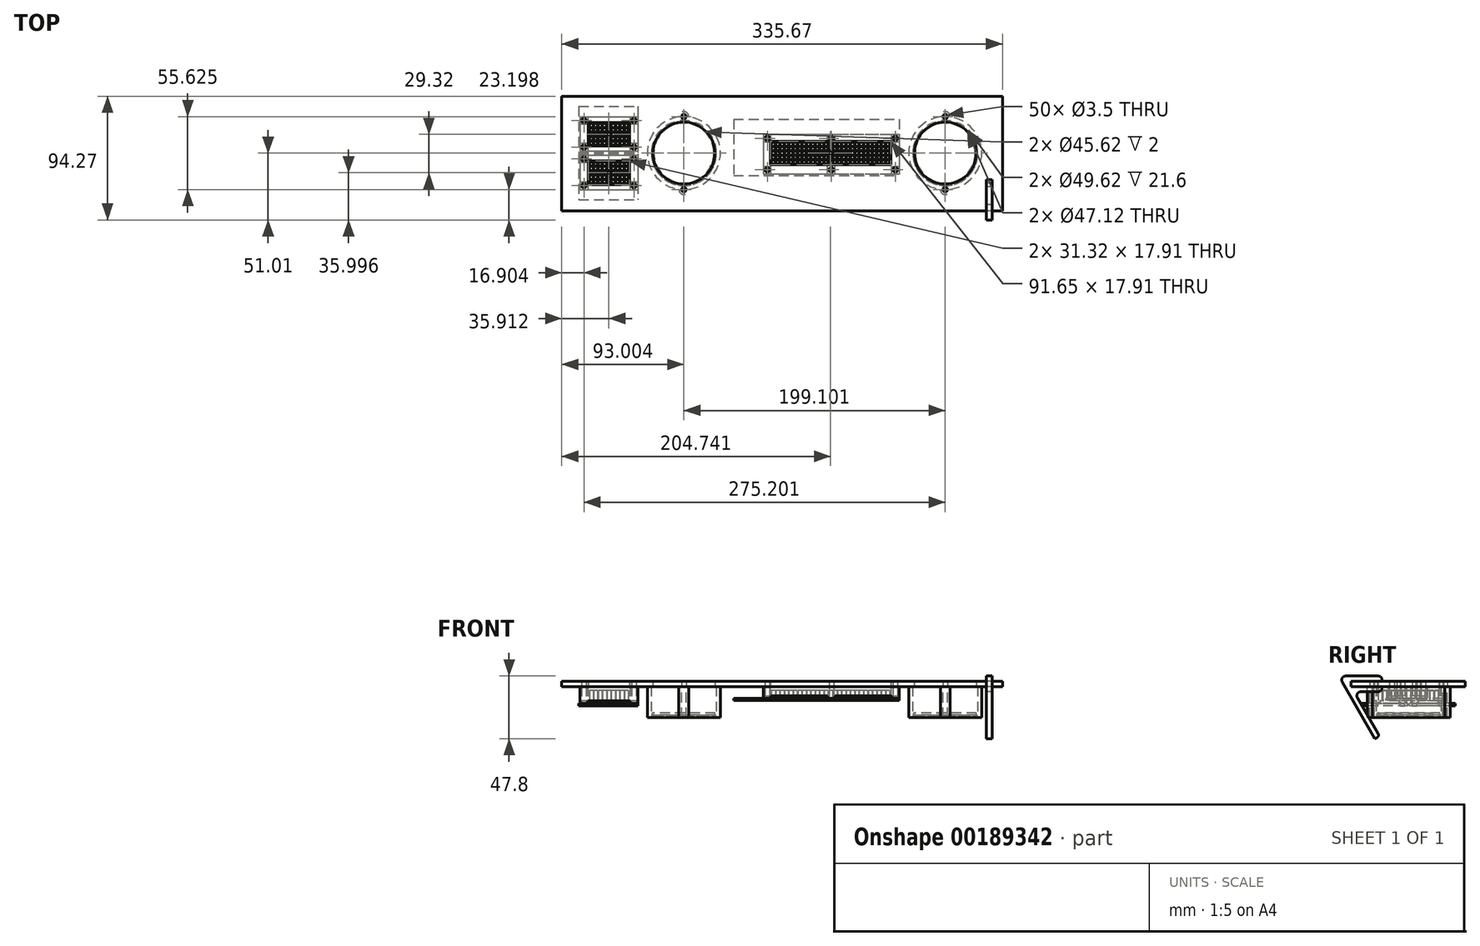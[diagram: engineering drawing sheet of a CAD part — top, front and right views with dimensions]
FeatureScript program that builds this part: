
annotation { "Feature Type Name" : "Feature", "Feature Type Description" : "" }
export const myFeature = defineFeature(function(context is Context, id is Id, definition is map)
    precondition{}
    {
        {
            var Q0;
            Q0=qCreatedBy(makeId("Top.planeOp"),FACE);
            var sketch = newSketch(context, id + "F0", { "sketchPlane" : qUnion([Q0])});
            skLineSegment(sketch, "E0.bottom", {"start": v(-19.95, 23.98) * mm, "end": v(106.25, 23.98) * mm});
            skLineSegment(sketch, "E0.top", {"start": v(-19.95, -19.02) * mm, "end": v(106.25, -19.02) * mm});
            skLineSegment(sketch, "E0.left", {"start": v(-19.95, 23.98) * mm, "end": v(-19.95, -19.02) * mm});
            skLineSegment(sketch, "E0.right", {"start": v(106.25, 23.98) * mm, "end": v(106.25, -19.02) * mm});
            skLineSegment(sketch, "E1.bottom", {"start": v(-137.86, 33.71) * mm, "end": v(-92.86, 33.71) * mm});
            skLineSegment(sketch, "E1.top", {"start": v(-137.86, -1.29) * mm, "end": v(-92.86, -1.29) * mm});
            skLineSegment(sketch, "E1.left", {"start": v(-137.86, 33.71) * mm, "end": v(-137.86, -1.29) * mm});
            skLineSegment(sketch, "E1.right", {"start": v(-92.86, 33.71) * mm, "end": v(-92.86, -1.29) * mm});
            skLineSegment(sketch, "E2.bottom", {"start": v(-137.86, -2.29) * mm, "end": v(-92.86, -2.29) * mm});
            skLineSegment(sketch, "E2.top", {"start": v(-137.86, -37.29) * mm, "end": v(-92.86, -37.29) * mm});
            skLineSegment(sketch, "E2.left", {"start": v(-137.86, -2.29) * mm, "end": v(-137.86, -37.29) * mm});
            skLineSegment(sketch, "E2.right", {"start": v(-92.86, -2.29) * mm, "end": v(-92.86, -37.29) * mm});
            skCircle(sketch, "E3", {"center": v(141.25, -1.79) * mm, "radius": 23.81 * mm});
            skCircle(sketch, "E4", {"center": v(-57.86, -1.79) * mm, "radius": 23.81 * mm});
            skLineSegment(sketch, "E5", {"start": v(-115.36, -1.29) * mm, "end": v(-115.36, -2.29) * mm, "construction": true});
            skLineSegment(sketch, "E6", {"start": v(-115.36, -1.79) * mm, "end": v(-90.24, -1.79) * mm, "construction": true});
            skLineSegment(sketch, "E7", {"start": v(43.15, -19.02) * mm, "end": v(43.15, -1.79) * mm});
            skSolve(sketch);
        }
        {
            var Q0;
            Q0=qCreatedBy(makeId("Top.planeOp"),FACE);
            cPlane(context, id + "F1", {"entities" : qUnion([Q0]), "cplaneType" : CPlaneType.OFFSET, "offset" : 9 * mm, "oppositeDirection" : true, "width" : 150 * mm, "height" : 150 * mm});
        }
        {
            var Q0;
            Q0=qCreatedBy(id+"F1.planeOp",FACE);
            var sketch = newSketch(context, id + "F2", { "sketchPlane" : qUnion([Q0])});
            skLineSegment(sketch, "E8.0", {"start": v(-19.95, 23.98) * mm, "end": v(-19.95, -19.02) * mm});
            skLineSegment(sketch, "E8.1", {"start": v(-19.95, 23.98) * mm, "end": v(106.25, 23.98) * mm});
            skLineSegment(sketch, "E8.2", {"start": v(-19.95, -19.02) * mm, "end": v(106.25, -19.02) * mm});
            skLineSegment(sketch, "E8.3", {"start": v(106.25, 23.98) * mm, "end": v(106.25, -19.02) * mm});
            skCircle(sketch, "E9", {"center": v(5.75, -14.52) * mm, "radius": 1.75 * mm});
            skCircle(sketch, "E10", {"center": v(54.5, -14.52) * mm, "radius": 1.75 * mm});
            skCircle(sketch, "E11", {"center": v(103.25, -14.52) * mm, "radius": 1.75 * mm});
            skCircle(sketch, "E12", {"center": v(5.75, 9.48) * mm, "radius": 1.75 * mm});
            skCircle(sketch, "E13", {"center": v(54.5, 9.48) * mm, "radius": 1.75 * mm});
            skCircle(sketch, "E14", {"center": v(103.25, 9.48) * mm, "radius": 1.75 * mm});
            skCircle(sketch, "E15", {"center": v(10.3, 4.91) * mm, "radius": 1.5 * mm});
            skCircle(sketch, "E16.0.1.0", {"center": v(10.3, 1.56) * mm, "radius": 1.5 * mm});
            skCircle(sketch, "E16.0.2.0", {"center": v(10.3, -1.79) * mm, "radius": 1.5 * mm});
            skCircle(sketch, "E16.0.3.0", {"center": v(10.3, -5.14) * mm, "radius": 1.5 * mm});
            skCircle(sketch, "E16.0.4.0", {"center": v(10.3, -8.5) * mm, "radius": 1.5 * mm});
            skCircle(sketch, "E16.1.0.0", {"center": v(13.66, 4.91) * mm, "radius": 1.5 * mm});
            skCircle(sketch, "E16.1.1.0", {"center": v(13.66, 1.56) * mm, "radius": 1.5 * mm});
            skCircle(sketch, "E16.1.2.0", {"center": v(13.66, -1.79) * mm, "radius": 1.5 * mm});
            skCircle(sketch, "E16.1.3.0", {"center": v(13.66, -5.14) * mm, "radius": 1.5 * mm});
            skCircle(sketch, "E16.1.4.0", {"center": v(13.66, -8.5) * mm, "radius": 1.5 * mm});
            skCircle(sketch, "E16.2.0.0", {"center": v(17, 4.91) * mm, "radius": 1.5 * mm});
            skCircle(sketch, "E16.2.1.0", {"center": v(17, 1.56) * mm, "radius": 1.5 * mm});
            skCircle(sketch, "E16.2.2.0", {"center": v(17, -1.79) * mm, "radius": 1.5 * mm});
            skCircle(sketch, "E16.2.3.0", {"center": v(17, -5.14) * mm, "radius": 1.5 * mm});
            skCircle(sketch, "E16.2.4.0", {"center": v(17, -8.5) * mm, "radius": 1.5 * mm});
            skCircle(sketch, "E16.3.0.0", {"center": v(20.36, 4.91) * mm, "radius": 1.5 * mm});
            skCircle(sketch, "E16.3.1.0", {"center": v(20.36, 1.56) * mm, "radius": 1.5 * mm});
            skCircle(sketch, "E16.3.2.0", {"center": v(20.36, -1.79) * mm, "radius": 1.5 * mm});
            skCircle(sketch, "E16.3.3.0", {"center": v(20.36, -5.14) * mm, "radius": 1.5 * mm});
            skCircle(sketch, "E16.3.4.0", {"center": v(20.36, -8.5) * mm, "radius": 1.5 * mm});
            skCircle(sketch, "E16.4.0.0", {"center": v(23.71, 4.91) * mm, "radius": 1.5 * mm});
            skCircle(sketch, "E16.4.1.0", {"center": v(23.71, 1.56) * mm, "radius": 1.5 * mm});
            skCircle(sketch, "E16.4.2.0", {"center": v(23.71, -1.79) * mm, "radius": 1.5 * mm});
            skCircle(sketch, "E16.4.3.0", {"center": v(23.71, -5.14) * mm, "radius": 1.5 * mm});
            skCircle(sketch, "E16.4.4.0", {"center": v(23.71, -8.5) * mm, "radius": 1.5 * mm});
            skCircle(sketch, "E16.5.0.0", {"center": v(27.07, 4.91) * mm, "radius": 1.5 * mm});
            skCircle(sketch, "E16.5.1.0", {"center": v(27.07, 1.56) * mm, "radius": 1.5 * mm});
            skCircle(sketch, "E16.5.2.0", {"center": v(27.07, -1.79) * mm, "radius": 1.5 * mm});
            skCircle(sketch, "E16.5.3.0", {"center": v(27.07, -5.14) * mm, "radius": 1.5 * mm});
            skCircle(sketch, "E16.5.4.0", {"center": v(27.07, -8.5) * mm, "radius": 1.5 * mm});
            skCircle(sketch, "E16.6.0.0", {"center": v(30.42, 4.91) * mm, "radius": 1.5 * mm});
            skCircle(sketch, "E16.6.1.0", {"center": v(30.42, 1.56) * mm, "radius": 1.5 * mm});
            skCircle(sketch, "E16.6.2.0", {"center": v(30.42, -1.79) * mm, "radius": 1.5 * mm});
            skCircle(sketch, "E16.6.3.0", {"center": v(30.42, -5.14) * mm, "radius": 1.5 * mm});
            skCircle(sketch, "E16.6.4.0", {"center": v(30.42, -8.5) * mm, "radius": 1.5 * mm});
            skCircle(sketch, "E16.7.0.0", {"center": v(33.77, 4.91) * mm, "radius": 1.5 * mm});
            skCircle(sketch, "E16.7.1.0", {"center": v(33.77, 1.56) * mm, "radius": 1.5 * mm});
            skCircle(sketch, "E16.7.2.0", {"center": v(33.77, -1.79) * mm, "radius": 1.5 * mm});
            skCircle(sketch, "E16.7.3.0", {"center": v(33.77, -5.14) * mm, "radius": 1.5 * mm});
            skCircle(sketch, "E16.7.4.0", {"center": v(33.77, -8.5) * mm, "radius": 1.5 * mm});
            skCircle(sketch, "E16.8.0.0", {"center": v(37.12, 4.91) * mm, "radius": 1.5 * mm});
            skCircle(sketch, "E16.8.1.0", {"center": v(37.12, 1.56) * mm, "radius": 1.5 * mm});
            skCircle(sketch, "E16.8.2.0", {"center": v(37.12, -1.79) * mm, "radius": 1.5 * mm});
            skCircle(sketch, "E16.8.3.0", {"center": v(37.12, -5.14) * mm, "radius": 1.5 * mm});
            skCircle(sketch, "E16.8.4.0", {"center": v(37.12, -8.5) * mm, "radius": 1.5 * mm});
            skCircle(sketch, "E16.9.0.0", {"center": v(40.47, 4.91) * mm, "radius": 1.5 * mm});
            skCircle(sketch, "E16.9.1.0", {"center": v(40.47, 1.56) * mm, "radius": 1.5 * mm});
            skCircle(sketch, "E16.9.2.0", {"center": v(40.47, -1.79) * mm, "radius": 1.5 * mm});
            skCircle(sketch, "E16.9.3.0", {"center": v(40.47, -5.14) * mm, "radius": 1.5 * mm});
            skCircle(sketch, "E16.9.4.0", {"center": v(40.47, -8.5) * mm, "radius": 1.5 * mm});
            skCircle(sketch, "E16.10.0.0", {"center": v(43.83, 4.91) * mm, "radius": 1.5 * mm});
            skCircle(sketch, "E16.10.1.0", {"center": v(43.83, 1.56) * mm, "radius": 1.5 * mm});
            skCircle(sketch, "E16.10.2.0", {"center": v(43.83, -1.79) * mm, "radius": 1.5 * mm});
            skCircle(sketch, "E16.10.3.0", {"center": v(43.83, -5.14) * mm, "radius": 1.5 * mm});
            skCircle(sketch, "E16.10.4.0", {"center": v(43.83, -8.5) * mm, "radius": 1.5 * mm});
            skCircle(sketch, "E16.11.0.0", {"center": v(47.18, 4.91) * mm, "radius": 1.5 * mm});
            skCircle(sketch, "E16.11.1.0", {"center": v(47.18, 1.56) * mm, "radius": 1.5 * mm});
            skCircle(sketch, "E16.11.2.0", {"center": v(47.18, -1.79) * mm, "radius": 1.5 * mm});
            skCircle(sketch, "E16.11.3.0", {"center": v(47.18, -5.14) * mm, "radius": 1.5 * mm});
            skCircle(sketch, "E16.11.4.0", {"center": v(47.18, -8.5) * mm, "radius": 1.5 * mm});
            skCircle(sketch, "E16.12.0.0", {"center": v(50.53, 4.91) * mm, "radius": 1.5 * mm});
            skCircle(sketch, "E16.12.1.0", {"center": v(50.53, 1.56) * mm, "radius": 1.5 * mm});
            skCircle(sketch, "E16.12.2.0", {"center": v(50.53, -1.79) * mm, "radius": 1.5 * mm});
            skCircle(sketch, "E16.12.3.0", {"center": v(50.53, -5.14) * mm, "radius": 1.5 * mm});
            skCircle(sketch, "E16.12.4.0", {"center": v(50.53, -8.5) * mm, "radius": 1.5 * mm});
            skCircle(sketch, "E16.13.0.0", {"center": v(53.88, 4.91) * mm, "radius": 1.5 * mm});
            skCircle(sketch, "E16.13.1.0", {"center": v(53.88, 1.56) * mm, "radius": 1.5 * mm});
            skCircle(sketch, "E16.13.2.0", {"center": v(53.88, -1.79) * mm, "radius": 1.5 * mm});
            skCircle(sketch, "E16.13.3.0", {"center": v(53.88, -5.14) * mm, "radius": 1.5 * mm});
            skCircle(sketch, "E16.13.4.0", {"center": v(53.88, -8.5) * mm, "radius": 1.5 * mm});
            skCircle(sketch, "E16.14.0.0", {"center": v(57.23, 4.91) * mm, "radius": 1.5 * mm});
            skCircle(sketch, "E16.14.1.0", {"center": v(57.23, 1.56) * mm, "radius": 1.5 * mm});
            skCircle(sketch, "E16.14.2.0", {"center": v(57.23, -1.79) * mm, "radius": 1.5 * mm});
            skCircle(sketch, "E16.14.3.0", {"center": v(57.23, -5.14) * mm, "radius": 1.5 * mm});
            skCircle(sketch, "E16.14.4.0", {"center": v(57.23, -8.5) * mm, "radius": 1.5 * mm});
            skCircle(sketch, "E16.15.0.0", {"center": v(60.59, 4.91) * mm, "radius": 1.5 * mm});
            skCircle(sketch, "E16.15.1.0", {"center": v(60.59, 1.56) * mm, "radius": 1.5 * mm});
            skCircle(sketch, "E16.15.2.0", {"center": v(60.59, -1.79) * mm, "radius": 1.5 * mm});
            skCircle(sketch, "E16.15.3.0", {"center": v(60.59, -5.14) * mm, "radius": 1.5 * mm});
            skCircle(sketch, "E16.15.4.0", {"center": v(60.59, -8.5) * mm, "radius": 1.5 * mm});
            skCircle(sketch, "E16.16.0.0", {"center": v(63.94, 4.91) * mm, "radius": 1.5 * mm});
            skCircle(sketch, "E16.16.1.0", {"center": v(63.94, 1.56) * mm, "radius": 1.5 * mm});
            skCircle(sketch, "E16.16.2.0", {"center": v(63.94, -1.79) * mm, "radius": 1.5 * mm});
            skCircle(sketch, "E16.16.3.0", {"center": v(63.94, -5.14) * mm, "radius": 1.5 * mm});
            skCircle(sketch, "E16.16.4.0", {"center": v(63.94, -8.5) * mm, "radius": 1.5 * mm});
            skCircle(sketch, "E16.17.0.0", {"center": v(67.29, 4.91) * mm, "radius": 1.5 * mm});
            skCircle(sketch, "E16.17.1.0", {"center": v(67.29, 1.56) * mm, "radius": 1.5 * mm});
            skCircle(sketch, "E16.17.2.0", {"center": v(67.29, -1.79) * mm, "radius": 1.5 * mm});
            skCircle(sketch, "E16.17.3.0", {"center": v(67.29, -5.14) * mm, "radius": 1.5 * mm});
            skCircle(sketch, "E16.17.4.0", {"center": v(67.29, -8.5) * mm, "radius": 1.5 * mm});
            skCircle(sketch, "E16.18.0.0", {"center": v(70.64, 4.91) * mm, "radius": 1.5 * mm});
            skCircle(sketch, "E16.18.1.0", {"center": v(70.64, 1.56) * mm, "radius": 1.5 * mm});
            skCircle(sketch, "E16.18.2.0", {"center": v(70.64, -1.79) * mm, "radius": 1.5 * mm});
            skCircle(sketch, "E16.18.3.0", {"center": v(70.64, -5.14) * mm, "radius": 1.5 * mm});
            skCircle(sketch, "E16.18.4.0", {"center": v(70.64, -8.5) * mm, "radius": 1.5 * mm});
            skCircle(sketch, "E16.19.0.0", {"center": v(74, 4.91) * mm, "radius": 1.5 * mm});
            skCircle(sketch, "E16.19.1.0", {"center": v(74, 1.56) * mm, "radius": 1.5 * mm});
            skCircle(sketch, "E16.19.2.0", {"center": v(74, -1.79) * mm, "radius": 1.5 * mm});
            skCircle(sketch, "E16.19.3.0", {"center": v(74, -5.14) * mm, "radius": 1.5 * mm});
            skCircle(sketch, "E16.19.4.0", {"center": v(74, -8.5) * mm, "radius": 1.5 * mm});
            skCircle(sketch, "E16.20.0.0", {"center": v(77.35, 4.91) * mm, "radius": 1.5 * mm});
            skCircle(sketch, "E16.20.1.0", {"center": v(77.35, 1.56) * mm, "radius": 1.5 * mm});
            skCircle(sketch, "E16.20.2.0", {"center": v(77.35, -1.79) * mm, "radius": 1.5 * mm});
            skCircle(sketch, "E16.20.3.0", {"center": v(77.35, -5.14) * mm, "radius": 1.5 * mm});
            skCircle(sketch, "E16.20.4.0", {"center": v(77.35, -8.5) * mm, "radius": 1.5 * mm});
            skCircle(sketch, "E16.21.0.0", {"center": v(80.7, 4.91) * mm, "radius": 1.5 * mm});
            skCircle(sketch, "E16.21.1.0", {"center": v(80.7, 1.56) * mm, "radius": 1.5 * mm});
            skCircle(sketch, "E16.21.2.0", {"center": v(80.7, -1.79) * mm, "radius": 1.5 * mm});
            skCircle(sketch, "E16.21.3.0", {"center": v(80.7, -5.14) * mm, "radius": 1.5 * mm});
            skCircle(sketch, "E16.21.4.0", {"center": v(80.7, -8.5) * mm, "radius": 1.5 * mm});
            skCircle(sketch, "E16.22.0.0", {"center": v(84.05, 4.91) * mm, "radius": 1.5 * mm});
            skCircle(sketch, "E16.22.1.0", {"center": v(84.05, 1.56) * mm, "radius": 1.5 * mm});
            skCircle(sketch, "E16.22.2.0", {"center": v(84.05, -1.79) * mm, "radius": 1.5 * mm});
            skCircle(sketch, "E16.22.3.0", {"center": v(84.05, -5.14) * mm, "radius": 1.5 * mm});
            skCircle(sketch, "E16.22.4.0", {"center": v(84.05, -8.5) * mm, "radius": 1.5 * mm});
            skCircle(sketch, "E16.23.0.0", {"center": v(87.4, 4.91) * mm, "radius": 1.5 * mm});
            skCircle(sketch, "E16.23.1.0", {"center": v(87.4, 1.56) * mm, "radius": 1.5 * mm});
            skCircle(sketch, "E16.23.2.0", {"center": v(87.4, -1.79) * mm, "radius": 1.5 * mm});
            skCircle(sketch, "E16.23.3.0", {"center": v(87.4, -5.14) * mm, "radius": 1.5 * mm});
            skCircle(sketch, "E16.23.4.0", {"center": v(87.4, -8.5) * mm, "radius": 1.5 * mm});
            skCircle(sketch, "E16.24.0.0", {"center": v(90.75, 4.91) * mm, "radius": 1.5 * mm});
            skCircle(sketch, "E16.24.1.0", {"center": v(90.75, 1.56) * mm, "radius": 1.5 * mm});
            skCircle(sketch, "E16.24.2.0", {"center": v(90.75, -1.79) * mm, "radius": 1.5 * mm});
            skCircle(sketch, "E16.24.3.0", {"center": v(90.75, -5.14) * mm, "radius": 1.5 * mm});
            skCircle(sketch, "E16.24.4.0", {"center": v(90.75, -8.5) * mm, "radius": 1.5 * mm});
            skCircle(sketch, "E16.25.0.0", {"center": v(94.1, 4.91) * mm, "radius": 1.5 * mm});
            skCircle(sketch, "E16.25.1.0", {"center": v(94.1, 1.56) * mm, "radius": 1.5 * mm});
            skCircle(sketch, "E16.25.2.0", {"center": v(94.1, -1.79) * mm, "radius": 1.5 * mm});
            skCircle(sketch, "E16.25.3.0", {"center": v(94.1, -5.14) * mm, "radius": 1.5 * mm});
            skCircle(sketch, "E16.25.4.0", {"center": v(94.1, -8.5) * mm, "radius": 1.5 * mm});
            skCircle(sketch, "E16.26.0.0", {"center": v(97.46, 4.91) * mm, "radius": 1.5 * mm});
            skCircle(sketch, "E16.26.1.0", {"center": v(97.46, 1.56) * mm, "radius": 1.5 * mm});
            skCircle(sketch, "E16.26.2.0", {"center": v(97.46, -1.79) * mm, "radius": 1.5 * mm});
            skCircle(sketch, "E16.26.3.0", {"center": v(97.46, -5.14) * mm, "radius": 1.5 * mm});
            skCircle(sketch, "E16.26.4.0", {"center": v(97.46, -8.5) * mm, "radius": 1.5 * mm});
            skLineSegment(sketch, "E16.direction1", {"start": v(10.3, 4.91) * mm, "end": v(13.66, 4.91) * mm, "construction": true});
            skLineSegment(sketch, "E16.direction2", {"start": v(10.3, 4.91) * mm, "end": v(10.3, 1.56) * mm, "construction": true});
            skSolve(sketch);
        }
        {
            var Q0;
            Q0=makeQuery(id+"F2.imprint","IMPRINT",FACE,{"disambiguationData":[TD([[makeQuery(id+"F2.imprint","IMPRINT",EDGE,{"derivedFrom":sQuery(id+"F2.wireOp",EDGE,"E8.0")}),1.0]])]});
            extrude(context, id + "F3", {"entities" : qUnion([Q0]), "oppositeDirection" : true, "depth" : 1.6 * mm});
        }
        {
            var Q0;
            Q0=makeQuery(id+"F2.imprint","IMPRINT",FACE,{"disambiguationData":[TD([[makeQuery(id+"F2.imprint","IMPRINT",EDGE,{"derivedFrom":sQuery(id+"F2.wireOp",EDGE,"E16.9.2.0")}),1.0]])]});
            var Q1;
            Q1=makeQuery(id+"F2.imprint","IMPRINT",FACE,{"disambiguationData":[TD([[makeQuery(id+"F2.imprint","IMPRINT",EDGE,{"derivedFrom":sQuery(id+"F2.wireOp",EDGE,"E16.12.3.0")}),1.0]])]});
            var Q2;
            Q2=makeQuery(id+"F2.imprint","IMPRINT",FACE,{"disambiguationData":[TD([[makeQuery(id+"F2.imprint","IMPRINT",EDGE,{"derivedFrom":sQuery(id+"F2.wireOp",EDGE,"E16.6.1.0")}),1.0]])]});
            var Q3;
            Q3=makeQuery(id+"F2.imprint","IMPRINT",FACE,{"disambiguationData":[TD([[makeQuery(id+"F2.imprint","IMPRINT",EDGE,{"derivedFrom":sQuery(id+"F2.wireOp",EDGE,"E16.25.2.0")}),1.0]])]});
            var Q4;
            Q4=makeQuery(id+"F2.imprint","IMPRINT",FACE,{"disambiguationData":[TD([[makeQuery(id+"F2.imprint","IMPRINT",EDGE,{"derivedFrom":sQuery(id+"F2.wireOp",EDGE,"E16.22.1.0")}),1.0]])]});
            var Q5;
            Q5=makeQuery(id+"F2.imprint","IMPRINT",FACE,{"disambiguationData":[TD([[makeQuery(id+"F2.imprint","IMPRINT",EDGE,{"derivedFrom":sQuery(id+"F2.wireOp",EDGE,"E16.9.3.0")}),1.0]])]});
            var Q6;
            Q6=makeQuery(id+"F2.imprint","IMPRINT",FACE,{"disambiguationData":[TD([[makeQuery(id+"F2.imprint","IMPRINT",EDGE,{"derivedFrom":sQuery(id+"F2.wireOp",EDGE,"E16.6.2.0")}),1.0]])]});
            var Q7;
            Q7=makeQuery(id+"F2.imprint","IMPRINT",FACE,{"disambiguationData":[TD([[makeQuery(id+"F2.imprint","IMPRINT",EDGE,{"derivedFrom":sQuery(id+"F2.wireOp",EDGE,"E16.3.1.0")}),1.0]])]});
            var Q8;
            Q8=makeQuery(id+"F2.imprint","IMPRINT",FACE,{"disambiguationData":[TD([[makeQuery(id+"F2.imprint","IMPRINT",EDGE,{"derivedFrom":sQuery(id+"F2.wireOp",EDGE,"E16.25.3.0")}),1.0]])]});
            var Q9;
            Q9=makeQuery(id+"F2.imprint","IMPRINT",FACE,{"disambiguationData":[TD([[makeQuery(id+"F2.imprint","IMPRINT",EDGE,{"derivedFrom":sQuery(id+"F2.wireOp",EDGE,"E16.19.1.0")}),1.0]])]});
            var Q10;
            Q10=makeQuery(id+"F2.imprint","IMPRINT",FACE,{"disambiguationData":[TD([[makeQuery(id+"F2.imprint","IMPRINT",EDGE,{"derivedFrom":sQuery(id+"F2.wireOp",EDGE,"E16.16.0.0")}),1.0]])]});
            var Q11;
            Q11=makeQuery(id+"F2.imprint","IMPRINT",FACE,{"disambiguationData":[TD([[makeQuery(id+"F2.imprint","IMPRINT",EDGE,{"derivedFrom":sQuery(id+"F2.wireOp",EDGE,"E16.25.4.0")}),1.0]])]});
            var Q12;
            Q12=makeQuery(id+"F2.imprint","IMPRINT",FACE,{"disambiguationData":[TD([[makeQuery(id+"F2.imprint","IMPRINT",EDGE,{"derivedFrom":sQuery(id+"F2.wireOp",EDGE,"E16.22.3.0")}),1.0]])]});
            var Q13;
            Q13=makeQuery(id+"F2.imprint","IMPRINT",FACE,{"disambiguationData":[TD([[makeQuery(id+"F2.imprint","IMPRINT",EDGE,{"derivedFrom":sQuery(id+"F2.wireOp",EDGE,"E16.16.1.0")}),1.0]])]});
            var Q14;
            Q14=makeQuery(id+"F2.imprint","IMPRINT",FACE,{"disambiguationData":[TD([[makeQuery(id+"F2.imprint","IMPRINT",EDGE,{"derivedFrom":sQuery(id+"F2.wireOp",EDGE,"E16.13.0.0")}),1.0]])]});
            var Q15;
            Q15=makeQuery(id+"F2.imprint","IMPRINT",FACE,{"disambiguationData":[TD([[makeQuery(id+"F2.imprint","IMPRINT",EDGE,{"derivedFrom":sQuery(id+"F2.wireOp",EDGE,"E16.9.4.0")}),1.0]])]});
            var Q16;
            Q16=makeQuery(id+"F2.imprint","IMPRINT",FACE,{"disambiguationData":[TD([[makeQuery(id+"F2.imprint","IMPRINT",EDGE,{"derivedFrom":sQuery(id+"F2.wireOp",EDGE,"E16.6.3.0")}),1.0]])]});
            var Q17;
            Q17=makeQuery(id+"F2.imprint","IMPRINT",FACE,{"disambiguationData":[TD([[makeQuery(id+"F2.imprint","IMPRINT",EDGE,{"derivedFrom":sQuery(id+"F2.wireOp",EDGE,"E16.13.1.0")}),1.0]])]});
            var Q18;
            Q18=makeQuery(id+"F2.imprint","IMPRINT",FACE,{"disambiguationData":[TD([[makeQuery(id+"F2.imprint","IMPRINT",EDGE,{"derivedFrom":sQuery(id+"F2.wireOp",EDGE,"E16.6.4.0")}),1.0]])]});
            var Q19;
            Q19=makeQuery(id+"F2.imprint","IMPRINT",FACE,{"disambiguationData":[TD([[makeQuery(id+"F2.imprint","IMPRINT",EDGE,{"derivedFrom":sQuery(id+"F2.wireOp",EDGE,"E16.3.3.0")}),1.0]])]});
            var Q20;
            Q20=makeQuery(id+"F2.imprint","IMPRINT",FACE,{"disambiguationData":[TD([[makeQuery(id+"F2.imprint","IMPRINT",EDGE,{"derivedFrom":sQuery(id+"F2.wireOp",EDGE,"E16.19.3.0")}),1.0]])]});
            var Q21;
            Q21=makeQuery(id+"F2.imprint","IMPRINT",FACE,{"disambiguationData":[TD([[makeQuery(id+"F2.imprint","IMPRINT",EDGE,{"derivedFrom":sQuery(id+"F2.wireOp",EDGE,"E16.16.2.0")}),1.0]])]});
            var Q22;
            Q22=makeQuery(id+"F2.imprint","IMPRINT",FACE,{"disambiguationData":[TD([[makeQuery(id+"F2.imprint","IMPRINT",EDGE,{"derivedFrom":sQuery(id+"F2.wireOp",EDGE,"E16.8.1.0")}),1.0]])]});
            var Q23;
            Q23=makeQuery(id+"F2.imprint","IMPRINT",FACE,{"disambiguationData":[TD([[makeQuery(id+"F2.imprint","IMPRINT",EDGE,{"derivedFrom":sQuery(id+"F2.wireOp",EDGE,"E16.13.2.0")}),1.0]])]});
            var Q24;
            Q24=makeQuery(id+"F2.imprint","IMPRINT",FACE,{"disambiguationData":[TD([[makeQuery(id+"F2.imprint","IMPRINT",EDGE,{"derivedFrom":sQuery(id+"F2.wireOp",EDGE,"E16.10.1.0")}),1.0]])]});
            var Q25;
            Q25=makeQuery(id+"F2.imprint","IMPRINT",FACE,{"disambiguationData":[TD([[makeQuery(id+"F2.imprint","IMPRINT",EDGE,{"derivedFrom":sQuery(id+"F2.wireOp",EDGE,"E16.7.0.0")}),1.0]])]});
            var Q26;
            Q26=makeQuery(id+"F2.imprint","IMPRINT",FACE,{"disambiguationData":[TD([[makeQuery(id+"F2.imprint","IMPRINT",EDGE,{"derivedFrom":sQuery(id+"F2.wireOp",EDGE,"E16.26.1.0")}),1.0]])]});
            var Q27;
            Q27=makeQuery(id+"F2.imprint","IMPRINT",FACE,{"disambiguationData":[TD([[makeQuery(id+"F2.imprint","IMPRINT",EDGE,{"derivedFrom":sQuery(id+"F2.wireOp",EDGE,"E16.21.0.0")}),1.0]])]});
            var Q28;
            Q28=makeQuery(id+"F2.imprint","IMPRINT",FACE,{"disambiguationData":[TD([[makeQuery(id+"F2.imprint","IMPRINT",EDGE,{"derivedFrom":sQuery(id+"F2.wireOp",EDGE,"E16.23.0.0")}),1.0]])]});
            var Q29;
            Q29=makeQuery(id+"F2.imprint","IMPRINT",FACE,{"disambiguationData":[TD([[makeQuery(id+"F2.imprint","IMPRINT",EDGE,{"derivedFrom":sQuery(id+"F2.wireOp",EDGE,"E16.14.3.0")}),1.0]])]});
            var Q30;
            Q30=makeQuery(id+"F2.imprint","IMPRINT",FACE,{"disambiguationData":[TD([[makeQuery(id+"F2.imprint","IMPRINT",EDGE,{"derivedFrom":sQuery(id+"F2.wireOp",EDGE,"E16.16.3.0")}),1.0]])]});
            var Q31;
            Q31=makeQuery(id+"F2.imprint","IMPRINT",FACE,{"disambiguationData":[TD([[makeQuery(id+"F2.imprint","IMPRINT",EDGE,{"derivedFrom":sQuery(id+"F2.wireOp",EDGE,"E16.11.2.0")}),1.0]])]});
            var Q32;
            Q32=makeQuery(id+"F2.imprint","IMPRINT",FACE,{"disambiguationData":[TD([[makeQuery(id+"F2.imprint","IMPRINT",EDGE,{"derivedFrom":sQuery(id+"F2.wireOp",EDGE,"E16.24.1.0")}),1.0]])]});
            var Q33;
            Q33=makeQuery(id+"F2.imprint","IMPRINT",FACE,{"disambiguationData":[TD([[makeQuery(id+"F2.imprint","IMPRINT",EDGE,{"derivedFrom":sQuery(id+"F2.wireOp",EDGE,"E16.13.3.0")}),1.0]])]});
            var Q34;
            Q34=makeQuery(id+"F2.imprint","IMPRINT",FACE,{"disambiguationData":[TD([[makeQuery(id+"F2.imprint","IMPRINT",EDGE,{"derivedFrom":sQuery(id+"F2.wireOp",EDGE,"E16.7.1.0")}),1.0]])]});
            var Q35;
            Q35=makeQuery(id+"F2.imprint","IMPRINT",FACE,{"disambiguationData":[TD([[makeQuery(id+"F2.imprint","IMPRINT",EDGE,{"derivedFrom":sQuery(id+"F2.wireOp",EDGE,"E16.4.0.0")}),1.0]])]});
            var Q36;
            Q36=makeQuery(id+"F2.imprint","IMPRINT",FACE,{"disambiguationData":[TD([[makeQuery(id+"F2.imprint","IMPRINT",EDGE,{"derivedFrom":sQuery(id+"F2.wireOp",EDGE,"E16.23.1.0")}),1.0]])]});
            var Q37;
            Q37=makeQuery(id+"F2.imprint","IMPRINT",FACE,{"disambiguationData":[TD([[makeQuery(id+"F2.imprint","IMPRINT",EDGE,{"derivedFrom":sQuery(id+"F2.wireOp",EDGE,"E16.20.0.0")}),1.0]])]});
            var Q38;
            Q38=makeQuery(id+"F2.imprint","IMPRINT",FACE,{"disambiguationData":[TD([[makeQuery(id+"F2.imprint","IMPRINT",EDGE,{"derivedFrom":sQuery(id+"F2.wireOp",EDGE,"E16.16.4.0")}),1.0]])]});
            var Q39;
            Q39=makeQuery(id+"F2.imprint","IMPRINT",FACE,{"disambiguationData":[TD([[makeQuery(id+"F2.imprint","IMPRINT",EDGE,{"derivedFrom":sQuery(id+"F2.wireOp",EDGE,"E16.4.3.0")}),1.0]])]});
            var Q40;
            Q40=makeQuery(id+"F2.imprint","IMPRINT",FACE,{"disambiguationData":[TD([[makeQuery(id+"F2.imprint","IMPRINT",EDGE,{"derivedFrom":sQuery(id+"F2.wireOp",EDGE,"E16.14.1.0")}),1.0]])]});
            var Q41;
            Q41=makeQuery(id+"F2.imprint","IMPRINT",FACE,{"disambiguationData":[TD([[makeQuery(id+"F2.imprint","IMPRINT",EDGE,{"derivedFrom":sQuery(id+"F2.wireOp",EDGE,"E16.11.0.0")}),1.0]])]});
            var Q42;
            Q42=makeQuery(id+"F2.imprint","IMPRINT",FACE,{"disambiguationData":[TD([[makeQuery(id+"F2.imprint","IMPRINT",EDGE,{"derivedFrom":sQuery(id+"F2.wireOp",EDGE,"E16.7.4.0")}),1.0]])]});
            var Q43;
            Q43=makeQuery(id+"F2.imprint","IMPRINT",FACE,{"disambiguationData":[TD([[makeQuery(id+"F2.imprint","IMPRINT",EDGE,{"derivedFrom":sQuery(id+"F2.wireOp",EDGE,"E16.23.4.0")}),1.0]])]});
            var Q44;
            Q44=makeQuery(id+"F2.imprint","IMPRINT",FACE,{"disambiguationData":[TD([[makeQuery(id+"F2.imprint","IMPRINT",EDGE,{"derivedFrom":sQuery(id+"F2.wireOp",EDGE,"E16.20.3.0")}),1.0]])]});
            var Q45;
            Q45=makeQuery(id+"F2.imprint","IMPRINT",FACE,{"disambiguationData":[TD([[makeQuery(id+"F2.imprint","IMPRINT",EDGE,{"derivedFrom":sQuery(id+"F2.wireOp",EDGE,"E16.13.4.0")}),1.0]])]});
            var Q46;
            Q46=makeQuery(id+"F2.imprint","IMPRINT",FACE,{"disambiguationData":[TD([[makeQuery(id+"F2.imprint","IMPRINT",EDGE,{"derivedFrom":sQuery(id+"F2.wireOp",EDGE,"E16.10.3.0")}),1.0]])]});
            var Q47;
            Q47=makeQuery(id+"F2.imprint","IMPRINT",FACE,{"disambiguationData":[TD([[makeQuery(id+"F2.imprint","IMPRINT",EDGE,{"derivedFrom":sQuery(id+"F2.wireOp",EDGE,"E16.7.2.0")}),1.0]])]});
            var Q48;
            Q48=makeQuery(id+"F2.imprint","IMPRINT",FACE,{"disambiguationData":[TD([[makeQuery(id+"F2.imprint","IMPRINT",EDGE,{"derivedFrom":sQuery(id+"F2.wireOp",EDGE,"E16.4.1.0")}),1.0]])]});
            var Q49;
            Q49=makeQuery(id+"F2.imprint","IMPRINT",FACE,{"disambiguationData":[TD([[makeQuery(id+"F2.imprint","IMPRINT",EDGE,{"derivedFrom":sQuery(id+"F2.wireOp",EDGE,"E16.26.3.0")}),1.0]])]});
            var Q50;
            Q50=makeQuery(id+"F2.imprint","IMPRINT",FACE,{"disambiguationData":[TD([[makeQuery(id+"F2.imprint","IMPRINT",EDGE,{"derivedFrom":sQuery(id+"F2.wireOp",EDGE,"E16.23.2.0")}),1.0]])]});
            var Q51;
            Q51=makeQuery(id+"F2.imprint","IMPRINT",FACE,{"disambiguationData":[TD([[makeQuery(id+"F2.imprint","IMPRINT",EDGE,{"derivedFrom":sQuery(id+"F2.wireOp",EDGE,"E16.20.1.0")}),1.0]])]});
            var Q52;
            Q52=makeQuery(id+"F2.imprint","IMPRINT",FACE,{"disambiguationData":[TD([[makeQuery(id+"F2.imprint","IMPRINT",EDGE,{"derivedFrom":sQuery(id+"F2.wireOp",EDGE,"E16.4.4.0")}),1.0]])]});
            var Q53;
            Q53=makeQuery(id+"F2.imprint","IMPRINT",FACE,{"disambiguationData":[TD([[makeQuery(id+"F2.imprint","IMPRINT",EDGE,{"derivedFrom":sQuery(id+"F2.wireOp",EDGE,"E16.17.3.0")}),1.0]])]});
            var Q54;
            Q54=makeQuery(id+"F2.imprint","IMPRINT",FACE,{"disambiguationData":[TD([[makeQuery(id+"F2.imprint","IMPRINT",EDGE,{"derivedFrom":sQuery(id+"F2.wireOp",EDGE,"E16.14.2.0")}),1.0]])]});
            var Q55;
            Q55=makeQuery(id+"F2.imprint","IMPRINT",FACE,{"disambiguationData":[TD([[makeQuery(id+"F2.imprint","IMPRINT",EDGE,{"derivedFrom":sQuery(id+"F2.wireOp",EDGE,"E16.11.1.0")}),1.0]])]});
            var Q56;
            Q56=makeQuery(id+"F2.imprint","IMPRINT",FACE,{"disambiguationData":[TD([[makeQuery(id+"F2.imprint","IMPRINT",EDGE,{"derivedFrom":sQuery(id+"F2.wireOp",EDGE,"E16.20.4.0")}),1.0]])]});
            var Q57;
            Q57=makeQuery(id+"F2.imprint","IMPRINT",FACE,{"disambiguationData":[TD([[makeQuery(id+"F2.imprint","IMPRINT",EDGE,{"derivedFrom":sQuery(id+"F2.wireOp",EDGE,"E16.14.0.0")}),1.0]])]});
            var Q58;
            Q58=makeQuery(id+"F2.imprint","IMPRINT",FACE,{"disambiguationData":[TD([[makeQuery(id+"F2.imprint","IMPRINT",EDGE,{"derivedFrom":sQuery(id+"F2.wireOp",EDGE,"E16.7.3.0")}),1.0]])]});
            var Q59;
            Q59=makeQuery(id+"F2.imprint","IMPRINT",FACE,{"disambiguationData":[TD([[makeQuery(id+"F2.imprint","IMPRINT",EDGE,{"derivedFrom":sQuery(id+"F2.wireOp",EDGE,"E16.4.2.0")}),1.0]])]});
            var Q60;
            Q60=makeQuery(id+"F2.imprint","IMPRINT",FACE,{"disambiguationData":[TD([[makeQuery(id+"F2.imprint","IMPRINT",EDGE,{"derivedFrom":sQuery(id+"F2.wireOp",EDGE,"E16.23.3.0")}),1.0]])]});
            var Q61;
            Q61=makeQuery(id+"F2.imprint","IMPRINT",FACE,{"disambiguationData":[TD([[makeQuery(id+"F2.imprint","IMPRINT",EDGE,{"derivedFrom":sQuery(id+"F2.wireOp",EDGE,"E16.20.2.0")}),1.0]])]});
            var Q62;
            Q62=makeQuery(id+"F2.imprint","IMPRINT",FACE,{"disambiguationData":[TD([[makeQuery(id+"F2.imprint","IMPRINT",EDGE,{"derivedFrom":sQuery(id+"F2.wireOp",EDGE,"E16.17.1.0")}),1.0]])]});
            var Q63;
            Q63=makeQuery(id+"F2.imprint","IMPRINT",FACE,{"disambiguationData":[TD([[makeQuery(id+"F2.imprint","IMPRINT",EDGE,{"derivedFrom":sQuery(id+"F2.wireOp",EDGE,"E16.5.1.0")}),1.0]])]});
            var Q64;
            Q64=makeQuery(id+"F2.imprint","IMPRINT",FACE,{"disambiguationData":[TD([[makeQuery(id+"F2.imprint","IMPRINT",EDGE,{"derivedFrom":sQuery(id+"F2.wireOp",EDGE,"E16.2.0.0")}),1.0]])]});
            var Q65;
            Q65=makeQuery(id+"F2.imprint","IMPRINT",FACE,{"disambiguationData":[TD([[makeQuery(id+"F2.imprint","IMPRINT",EDGE,{"derivedFrom":sQuery(id+"F2.wireOp",EDGE,"E16.18.0.0")}),1.0]])]});
            var Q66;
            Q66=makeQuery(id+"F2.imprint","IMPRINT",FACE,{"disambiguationData":[TD([[makeQuery(id+"F2.imprint","IMPRINT",EDGE,{"derivedFrom":sQuery(id+"F2.wireOp",EDGE,"E16.14.4.0")}),1.0]])]});
            var Q67;
            Q67=makeQuery(id+"F2.imprint","IMPRINT",FACE,{"disambiguationData":[TD([[makeQuery(id+"F2.imprint","IMPRINT",EDGE,{"derivedFrom":sQuery(id+"F2.wireOp",EDGE,"E16.11.3.0")}),1.0]])]});
            var Q68;
            Q68=makeQuery(id+"F2.imprint","IMPRINT",FACE,{"disambiguationData":[TD([[makeQuery(id+"F2.imprint","IMPRINT",EDGE,{"derivedFrom":sQuery(id+"F2.wireOp",EDGE,"E16.21.1.0")}),1.0]])]});
            var Q69;
            Q69=makeQuery(id+"F2.imprint","IMPRINT",FACE,{"disambiguationData":[TD([[makeQuery(id+"F2.imprint","IMPRINT",EDGE,{"derivedFrom":sQuery(id+"F2.wireOp",EDGE,"E16.2.1.0")}),1.0]])]});
            var Q70;
            Q70=makeQuery(id+"F2.imprint","IMPRINT",FACE,{"disambiguationData":[TD([[makeQuery(id+"F2.imprint","IMPRINT",EDGE,{"derivedFrom":sQuery(id+"F2.wireOp",EDGE,"E16.18.1.0")}),1.0]])]});
            var Q71;
            Q71=makeQuery(id+"F2.imprint","IMPRINT",FACE,{"disambiguationData":[TD([[makeQuery(id+"F2.imprint","IMPRINT",EDGE,{"derivedFrom":sQuery(id+"F2.wireOp",EDGE,"E16.11.4.0")}),1.0]])]});
            var Q72;
            Q72=makeQuery(id+"F2.imprint","IMPRINT",FACE,{"disambiguationData":[TD([[makeQuery(id+"F2.imprint","IMPRINT",EDGE,{"derivedFrom":sQuery(id+"F2.wireOp",EDGE,"E16.8.3.0")}),1.0]])]});
            var Q73;
            Q73=makeQuery(id+"F2.imprint","IMPRINT",FACE,{"disambiguationData":[TD([[makeQuery(id+"F2.imprint","IMPRINT",EDGE,{"derivedFrom":sQuery(id+"F2.wireOp",EDGE,"E16.24.3.0")}),1.0]])]});
            var Q74;
            Q74=makeQuery(id+"F2.imprint","IMPRINT",FACE,{"disambiguationData":[TD([[makeQuery(id+"F2.imprint","IMPRINT",EDGE,{"derivedFrom":sQuery(id+"F2.wireOp",EDGE,"E16.21.2.0")}),1.0]])]});
            var Q75;
            Q75=makeQuery(id+"F2.imprint","IMPRINT",FACE,{"disambiguationData":[TD([[makeQuery(id+"F2.imprint","IMPRINT",EDGE,{"derivedFrom":sQuery(id+"F2.wireOp",EDGE,"E16.5.3.0")}),1.0]])]});
            var Q76;
            Q76=makeQuery(id+"F2.imprint","IMPRINT",FACE,{"disambiguationData":[TD([[makeQuery(id+"F2.imprint","IMPRINT",EDGE,{"derivedFrom":sQuery(id+"F2.wireOp",EDGE,"E16.2.2.0")}),1.0]])]});
            var Q77;
            Q77=makeQuery(id+"F2.imprint","IMPRINT",FACE,{"disambiguationData":[TD([[makeQuery(id+"F2.imprint","IMPRINT",EDGE,{"derivedFrom":sQuery(id+"F2.wireOp",EDGE,"E16.18.2.0")}),1.0]])]});
            var Q78;
            Q78=makeQuery(id+"F2.imprint","IMPRINT",FACE,{"disambiguationData":[TD([[makeQuery(id+"F2.imprint","IMPRINT",EDGE,{"derivedFrom":sQuery(id+"F2.wireOp",EDGE,"E16.15.1.0")}),1.0]])]});
            var Q79;
            Q79=makeQuery(id+"F2.imprint","IMPRINT",FACE,{"disambiguationData":[TD([[makeQuery(id+"F2.imprint","IMPRINT",EDGE,{"derivedFrom":sQuery(id+"F2.wireOp",EDGE,"E16.21.3.0")}),1.0]])]});
            var Q80;
            Q80=makeQuery(id+"F2.imprint","IMPRINT",FACE,{"disambiguationData":[TD([[makeQuery(id+"F2.imprint","IMPRINT",EDGE,{"derivedFrom":sQuery(id+"F2.wireOp",EDGE,"E16.1.3.0")}),1.0]])]});
            var Q81;
            Q81=makeQuery(id+"F2.imprint","IMPRINT",FACE,{"disambiguationData":[TD([[makeQuery(id+"F2.imprint","IMPRINT",EDGE,{"derivedFrom":sQuery(id+"F2.wireOp",EDGE,"E15")}),1.0]])]});
            var Q82;
            Q82=makeQuery(id+"F2.imprint","IMPRINT",FACE,{"disambiguationData":[TD([[makeQuery(id+"F2.imprint","IMPRINT",EDGE,{"derivedFrom":sQuery(id+"F2.wireOp",EDGE,"E16.0.1.0")}),1.0]])]});
            var Q83;
            Q83=makeQuery(id+"F2.imprint","IMPRINT",FACE,{"disambiguationData":[TD([[makeQuery(id+"F2.imprint","IMPRINT",EDGE,{"derivedFrom":sQuery(id+"F2.wireOp",EDGE,"E16.0.2.0")}),1.0]])]});
            var Q84;
            Q84=makeQuery(id+"F2.imprint","IMPRINT",FACE,{"disambiguationData":[TD([[makeQuery(id+"F2.imprint","IMPRINT",EDGE,{"derivedFrom":sQuery(id+"F2.wireOp",EDGE,"E16.0.3.0")}),1.0]])]});
            var Q85;
            Q85=makeQuery(id+"F2.imprint","IMPRINT",FACE,{"disambiguationData":[TD([[makeQuery(id+"F2.imprint","IMPRINT",EDGE,{"derivedFrom":sQuery(id+"F2.wireOp",EDGE,"E16.0.4.0")}),1.0]])]});
            var Q86;
            Q86=makeQuery(id+"F2.imprint","IMPRINT",FACE,{"disambiguationData":[TD([[makeQuery(id+"F2.imprint","IMPRINT",EDGE,{"derivedFrom":sQuery(id+"F2.wireOp",EDGE,"E16.1.1.0")}),1.0]])]});
            var Q87;
            Q87=makeQuery(id+"F2.imprint","IMPRINT",FACE,{"disambiguationData":[TD([[makeQuery(id+"F2.imprint","IMPRINT",EDGE,{"derivedFrom":sQuery(id+"F2.wireOp",EDGE,"E16.2.3.0")}),1.0]])]});
            var Q88;
            Q88=makeQuery(id+"F2.imprint","IMPRINT",FACE,{"disambiguationData":[TD([[makeQuery(id+"F2.imprint","IMPRINT",EDGE,{"derivedFrom":sQuery(id+"F2.wireOp",EDGE,"E16.18.3.0")}),1.0]])]});
            var Q89;
            Q89=makeQuery(id+"F2.imprint","IMPRINT",FACE,{"disambiguationData":[TD([[makeQuery(id+"F2.imprint","IMPRINT",EDGE,{"derivedFrom":sQuery(id+"F2.wireOp",EDGE,"E16.12.1.0")}),1.0]])]});
            var Q90;
            Q90=makeQuery(id+"F2.imprint","IMPRINT",FACE,{"disambiguationData":[TD([[makeQuery(id+"F2.imprint","IMPRINT",EDGE,{"derivedFrom":sQuery(id+"F2.wireOp",EDGE,"E16.9.0.0")}),1.0]])]});
            var Q91;
            Q91=makeQuery(id+"F2.imprint","IMPRINT",FACE,{"disambiguationData":[TD([[makeQuery(id+"F2.imprint","IMPRINT",EDGE,{"derivedFrom":sQuery(id+"F2.wireOp",EDGE,"E16.25.0.0")}),1.0]])]});
            var Q92;
            Q92=makeQuery(id+"F2.imprint","IMPRINT",FACE,{"disambiguationData":[TD([[makeQuery(id+"F2.imprint","IMPRINT",EDGE,{"derivedFrom":sQuery(id+"F2.wireOp",EDGE,"E16.21.4.0")}),1.0]])]});
            var Q93;
            Q93=makeQuery(id+"F2.imprint","IMPRINT",FACE,{"disambiguationData":[TD([[makeQuery(id+"F2.imprint","IMPRINT",EDGE,{"derivedFrom":sQuery(id+"F2.wireOp",EDGE,"E16.6.0.0")}),1.0]])]});
            var Q94;
            Q94=makeQuery(id+"F2.imprint","IMPRINT",FACE,{"disambiguationData":[TD([[makeQuery(id+"F2.imprint","IMPRINT",EDGE,{"derivedFrom":sQuery(id+"F2.wireOp",EDGE,"E16.2.4.0")}),1.0]])]});
            var Q95;
            Q95=makeQuery(id+"F2.imprint","IMPRINT",FACE,{"disambiguationData":[TD([[makeQuery(id+"F2.imprint","IMPRINT",EDGE,{"derivedFrom":sQuery(id+"F2.wireOp",EDGE,"E16.18.4.0")}),1.0]])]});
            var Q96;
            Q96=makeQuery(id+"F2.imprint","IMPRINT",FACE,{"disambiguationData":[TD([[makeQuery(id+"F2.imprint","IMPRINT",EDGE,{"derivedFrom":sQuery(id+"F2.wireOp",EDGE,"E16.15.3.0")}),1.0]])]});
            var Q97;
            Q97=makeQuery(id+"F2.imprint","IMPRINT",FACE,{"disambiguationData":[TD([[makeQuery(id+"F2.imprint","IMPRINT",EDGE,{"derivedFrom":sQuery(id+"F2.wireOp",EDGE,"E16.9.1.0")}),1.0]])]});
            var Q98;
            Q98=makeQuery(id+"F2.imprint","IMPRINT",FACE,{"disambiguationData":[TD([[makeQuery(id+"F2.imprint","IMPRINT",EDGE,{"derivedFrom":sQuery(id+"F2.wireOp",EDGE,"E16.25.1.0")}),1.0]])]});
            var Q99;
            Q99=makeQuery(id+"F2.imprint","IMPRINT",FACE,{"disambiguationData":[TD([[makeQuery(id+"F2.imprint","IMPRINT",EDGE,{"derivedFrom":sQuery(id+"F2.wireOp",EDGE,"E16.15.4.0")}),1.0]])]});
            var Q100;
            Q100=makeQuery(id+"F2.imprint","IMPRINT",FACE,{"disambiguationData":[TD([[makeQuery(id+"F2.imprint","IMPRINT",EDGE,{"derivedFrom":sQuery(id+"F2.wireOp",EDGE,"E16.19.0.0")}),1.0]])]});
            var Q101;
            Q101=makeQuery(id+"F2.imprint","IMPRINT",FACE,{"disambiguationData":[TD([[makeQuery(id+"F2.imprint","IMPRINT",EDGE,{"derivedFrom":sQuery(id+"F2.wireOp",EDGE,"E16.3.0.0")}),1.0]])]});
            var Q102;
            Q102=makeQuery(id+"F2.imprint","IMPRINT",FACE,{"disambiguationData":[TD([[makeQuery(id+"F2.imprint","IMPRINT",EDGE,{"derivedFrom":sQuery(id+"F2.wireOp",EDGE,"E16.12.4.0")}),1.0]])]});
            var Q103;
            Q103=makeQuery(id+"F2.imprint","IMPRINT",FACE,{"disambiguationData":[TD([[makeQuery(id+"F2.imprint","IMPRINT",EDGE,{"derivedFrom":sQuery(id+"F2.wireOp",EDGE,"E16.22.2.0")}),1.0]])]});
            var Q104;
            Q104=makeQuery(id+"F2.imprint","IMPRINT",FACE,{"disambiguationData":[TD([[makeQuery(id+"F2.imprint","IMPRINT",EDGE,{"derivedFrom":sQuery(id+"F2.wireOp",EDGE,"E16.19.2.0")}),1.0]])]});
            var Q105;
            Q105=makeQuery(id+"F2.imprint","IMPRINT",FACE,{"disambiguationData":[TD([[makeQuery(id+"F2.imprint","IMPRINT",EDGE,{"derivedFrom":sQuery(id+"F2.wireOp",EDGE,"E16.3.2.0")}),1.0]])]});
            var Q106;
            Q106=makeQuery(id+"F2.imprint","IMPRINT",FACE,{"disambiguationData":[TD([[makeQuery(id+"F2.imprint","IMPRINT",EDGE,{"derivedFrom":sQuery(id+"F2.wireOp",EDGE,"E16.10.0.0")}),1.0]])]});
            var Q107;
            Q107=makeQuery(id+"F2.imprint","IMPRINT",FACE,{"disambiguationData":[TD([[makeQuery(id+"F2.imprint","IMPRINT",EDGE,{"derivedFrom":sQuery(id+"F2.wireOp",EDGE,"E16.26.0.0")}),1.0]])]});
            var Q108;
            Q108=makeQuery(id+"F2.imprint","IMPRINT",FACE,{"disambiguationData":[TD([[makeQuery(id+"F2.imprint","IMPRINT",EDGE,{"derivedFrom":sQuery(id+"F2.wireOp",EDGE,"E16.22.4.0")}),1.0]])]});
            var Q109;
            Q109=makeQuery(id+"F2.imprint","IMPRINT",FACE,{"disambiguationData":[TD([[makeQuery(id+"F2.imprint","IMPRINT",EDGE,{"derivedFrom":sQuery(id+"F2.wireOp",EDGE,"E16.5.0.0")}),1.0]])]});
            var Q110;
            Q110=makeQuery(id+"F2.imprint","IMPRINT",FACE,{"disambiguationData":[TD([[makeQuery(id+"F2.imprint","IMPRINT",EDGE,{"derivedFrom":sQuery(id+"F2.wireOp",EDGE,"E16.3.4.0")}),1.0]])]});
            var Q111;
            Q111=makeQuery(id+"F2.imprint","IMPRINT",FACE,{"disambiguationData":[TD([[makeQuery(id+"F2.imprint","IMPRINT",EDGE,{"derivedFrom":sQuery(id+"F2.wireOp",EDGE,"E16.17.4.0")}),1.0]])]});
            var Q112;
            Q112=makeQuery(id+"F2.imprint","IMPRINT",FACE,{"disambiguationData":[TD([[makeQuery(id+"F2.imprint","IMPRINT",EDGE,{"derivedFrom":sQuery(id+"F2.wireOp",EDGE,"E16.19.4.0")}),1.0]])]});
            var Q113;
            Q113=makeQuery(id+"F2.imprint","IMPRINT",FACE,{"disambiguationData":[TD([[makeQuery(id+"F2.imprint","IMPRINT",EDGE,{"derivedFrom":sQuery(id+"F2.wireOp",EDGE,"E16.10.2.0")}),1.0]])]});
            var Q114;
            Q114=makeQuery(id+"F2.imprint","IMPRINT",FACE,{"disambiguationData":[TD([[makeQuery(id+"F2.imprint","IMPRINT",EDGE,{"derivedFrom":sQuery(id+"F2.wireOp",EDGE,"E16.26.2.0")}),1.0]])]});
            var Q115;
            Q115=makeQuery(id+"F2.imprint","IMPRINT",FACE,{"disambiguationData":[TD([[makeQuery(id+"F2.imprint","IMPRINT",EDGE,{"derivedFrom":sQuery(id+"F2.wireOp",EDGE,"E16.17.2.0")}),1.0]])]});
            var Q116;
            Q116=makeQuery(id+"F2.imprint","IMPRINT",FACE,{"disambiguationData":[TD([[makeQuery(id+"F2.imprint","IMPRINT",EDGE,{"derivedFrom":sQuery(id+"F2.wireOp",EDGE,"E16.17.0.0")}),1.0]])]});
            var Q117;
            Q117=makeQuery(id+"F2.imprint","IMPRINT",FACE,{"disambiguationData":[TD([[makeQuery(id+"F2.imprint","IMPRINT",EDGE,{"derivedFrom":sQuery(id+"F2.wireOp",EDGE,"E16.8.0.0")}),1.0]])]});
            var Q118;
            Q118=makeQuery(id+"F2.imprint","IMPRINT",FACE,{"disambiguationData":[TD([[makeQuery(id+"F2.imprint","IMPRINT",EDGE,{"derivedFrom":sQuery(id+"F2.wireOp",EDGE,"E16.24.0.0")}),1.0]])]});
            var Q119;
            Q119=makeQuery(id+"F2.imprint","IMPRINT",FACE,{"disambiguationData":[TD([[makeQuery(id+"F2.imprint","IMPRINT",EDGE,{"derivedFrom":sQuery(id+"F2.wireOp",EDGE,"E16.10.4.0")}),1.0]])]});
            var Q120;
            Q120=makeQuery(id+"F2.imprint","IMPRINT",FACE,{"disambiguationData":[TD([[makeQuery(id+"F2.imprint","IMPRINT",EDGE,{"derivedFrom":sQuery(id+"F2.wireOp",EDGE,"E16.26.4.0")}),1.0]])]});
            var Q121;
            Q121=makeQuery(id+"F2.imprint","IMPRINT",FACE,{"disambiguationData":[TD([[makeQuery(id+"F2.imprint","IMPRINT",EDGE,{"derivedFrom":sQuery(id+"F2.wireOp",EDGE,"E16.8.2.0")}),1.0]])]});
            var Q122;
            Q122=makeQuery(id+"F2.imprint","IMPRINT",FACE,{"disambiguationData":[TD([[makeQuery(id+"F2.imprint","IMPRINT",EDGE,{"derivedFrom":sQuery(id+"F2.wireOp",EDGE,"E16.24.2.0")}),1.0]])]});
            var Q123;
            Q123=makeQuery(id+"F2.imprint","IMPRINT",FACE,{"disambiguationData":[TD([[makeQuery(id+"F2.imprint","IMPRINT",EDGE,{"derivedFrom":sQuery(id+"F2.wireOp",EDGE,"E16.5.2.0")}),1.0]])]});
            var Q124;
            Q124=makeQuery(id+"F2.imprint","IMPRINT",FACE,{"disambiguationData":[TD([[makeQuery(id+"F2.imprint","IMPRINT",EDGE,{"derivedFrom":sQuery(id+"F2.wireOp",EDGE,"E16.15.0.0")}),1.0]])]});
            var Q125;
            Q125=makeQuery(id+"F2.imprint","IMPRINT",FACE,{"disambiguationData":[TD([[makeQuery(id+"F2.imprint","IMPRINT",EDGE,{"derivedFrom":sQuery(id+"F2.wireOp",EDGE,"E16.12.0.0")}),1.0]])]});
            var Q126;
            Q126=makeQuery(id+"F2.imprint","IMPRINT",FACE,{"disambiguationData":[TD([[makeQuery(id+"F2.imprint","IMPRINT",EDGE,{"derivedFrom":sQuery(id+"F2.wireOp",EDGE,"E16.8.4.0")}),1.0]])]});
            var Q127;
            Q127=makeQuery(id+"F2.imprint","IMPRINT",FACE,{"disambiguationData":[TD([[makeQuery(id+"F2.imprint","IMPRINT",EDGE,{"derivedFrom":sQuery(id+"F2.wireOp",EDGE,"E16.24.4.0")}),1.0]])]});
            var Q128;
            Q128=makeQuery(id+"F2.imprint","IMPRINT",FACE,{"disambiguationData":[TD([[makeQuery(id+"F2.imprint","IMPRINT",EDGE,{"derivedFrom":sQuery(id+"F2.wireOp",EDGE,"E16.1.4.0")}),1.0]])]});
            var Q129;
            Q129=makeQuery(id+"F2.imprint","IMPRINT",FACE,{"disambiguationData":[TD([[makeQuery(id+"F2.imprint","IMPRINT",EDGE,{"derivedFrom":sQuery(id+"F2.wireOp",EDGE,"E16.1.2.0")}),1.0]])]});
            var Q130;
            Q130=makeQuery(id+"F2.imprint","IMPRINT",FACE,{"disambiguationData":[TD([[makeQuery(id+"F2.imprint","IMPRINT",EDGE,{"derivedFrom":sQuery(id+"F2.wireOp",EDGE,"E16.5.4.0")}),1.0]])]});
            var Q131;
            Q131=makeQuery(id+"F2.imprint","IMPRINT",FACE,{"disambiguationData":[TD([[makeQuery(id+"F2.imprint","IMPRINT",EDGE,{"derivedFrom":sQuery(id+"F2.wireOp",EDGE,"E16.15.2.0")}),1.0]])]});
            var Q132;
            Q132=makeQuery(id+"F2.imprint","IMPRINT",FACE,{"disambiguationData":[TD([[makeQuery(id+"F2.imprint","IMPRINT",EDGE,{"derivedFrom":sQuery(id+"F2.wireOp",EDGE,"E16.12.2.0")}),1.0]])]});
            var Q133;
            Q133=makeQuery(id+"F2.imprint","IMPRINT",FACE,{"disambiguationData":[TD([[makeQuery(id+"F2.imprint","IMPRINT",EDGE,{"derivedFrom":sQuery(id+"F2.wireOp",EDGE,"E16.22.0.0")}),1.0]])]});
            var Q134;
            Q134=makeQuery(id+"F2.imprint","IMPRINT",FACE,{"disambiguationData":[TD([[makeQuery(id+"F2.imprint","IMPRINT",EDGE,{"derivedFrom":sQuery(id+"F2.wireOp",EDGE,"E16.1.0.0")}),1.0]])]});
            var Q135;
            Q135=makeQuery(id+"F2.imprint","IMPRINT",FACE,{"disambiguationData":[TD([[makeQuery(id+"F2.imprint","IMPRINT",EDGE,{"derivedFrom":sQuery(id+"F2.wireOp",EDGE,"E8.0")}),1.0]])]});
            extrude(context, id + "F4", {"entities" : qUnion([Q0, Q1, Q2, Q3, Q4, Q5, Q6, Q7, Q8, Q9, Q10, Q11, Q12, Q13, Q14, Q15, Q16, Q17, Q18, Q19, Q20, Q21, Q22, Q23, Q24, Q25, Q26, Q27, Q28, Q29, Q30, Q31, Q32, Q33, Q34, Q35, Q36, Q37, Q38, Q39, Q40, Q41, Q42, Q43, Q44, Q45, Q46, Q47, Q48, Q49, Q50, Q51, Q52, Q53, Q54, Q55, Q56, Q57, Q58, Q59, Q60, Q61, Q62, Q63, Q64, Q65, Q66, Q67, Q68, Q69, Q70, Q71, Q72, Q73, Q74, Q75, Q76, Q77, Q78, Q79, Q80, Q81, Q82, Q83, Q84, Q85, Q86, Q87, Q88, Q89, Q90, Q91, Q92, Q93, Q94, Q95, Q96, Q97, Q98, Q99, Q100, Q101, Q102, Q103, Q104, Q105, Q106, Q107, Q108, Q109, Q110, Q111, Q112, Q113, Q114, Q115, Q116, Q117, Q118, Q119, Q120, Q121, Q122, Q123, Q124, Q125, Q126, Q127, Q128, Q129, Q130, Q131, Q132, Q133, Q134, Q135]), "operationType" : NewBodyOperationType.ADD, "oppositeDirection" : true, "depth" : 1.6 * mm});
        }
        {
            var Q0;
            Q0=makeQuery(id+"F2.imprint","IMPRINT",FACE,{"disambiguationData":[TD([[makeQuery(id+"F2.imprint","IMPRINT",EDGE,{"derivedFrom":sQuery(id+"F2.wireOp",EDGE,"E16.9.2.0")}),1.0]])]});
            var Q1;
            Q1=makeQuery(id+"F2.imprint","IMPRINT",FACE,{"disambiguationData":[TD([[makeQuery(id+"F2.imprint","IMPRINT",EDGE,{"derivedFrom":sQuery(id+"F2.wireOp",EDGE,"E16.12.3.0")}),1.0]])]});
            var Q2;
            Q2=makeQuery(id+"F2.imprint","IMPRINT",FACE,{"disambiguationData":[TD([[makeQuery(id+"F2.imprint","IMPRINT",EDGE,{"derivedFrom":sQuery(id+"F2.wireOp",EDGE,"E16.19.0.0")}),1.0]])]});
            var Q3;
            Q3=makeQuery(id+"F2.imprint","IMPRINT",FACE,{"disambiguationData":[TD([[makeQuery(id+"F2.imprint","IMPRINT",EDGE,{"derivedFrom":sQuery(id+"F2.wireOp",EDGE,"E16.3.0.0")}),1.0]])]});
            var Q4;
            Q4=makeQuery(id+"F2.imprint","IMPRINT",FACE,{"disambiguationData":[TD([[makeQuery(id+"F2.imprint","IMPRINT",EDGE,{"derivedFrom":sQuery(id+"F2.wireOp",EDGE,"E16.6.1.0")}),1.0]])]});
            var Q5;
            Q5=makeQuery(id+"F2.imprint","IMPRINT",FACE,{"disambiguationData":[TD([[makeQuery(id+"F2.imprint","IMPRINT",EDGE,{"derivedFrom":sQuery(id+"F2.wireOp",EDGE,"E16.25.2.0")}),1.0]])]});
            var Q6;
            Q6=makeQuery(id+"F2.imprint","IMPRINT",FACE,{"disambiguationData":[TD([[makeQuery(id+"F2.imprint","IMPRINT",EDGE,{"derivedFrom":sQuery(id+"F2.wireOp",EDGE,"E16.22.1.0")}),1.0]])]});
            var Q7;
            Q7=makeQuery(id+"F2.imprint","IMPRINT",FACE,{"disambiguationData":[TD([[makeQuery(id+"F2.imprint","IMPRINT",EDGE,{"derivedFrom":sQuery(id+"F2.wireOp",EDGE,"E16.3.2.0")}),1.0]])]});
            var Q8;
            Q8=makeQuery(id+"F2.imprint","IMPRINT",FACE,{"disambiguationData":[TD([[makeQuery(id+"F2.imprint","IMPRINT",EDGE,{"derivedFrom":sQuery(id+"F2.wireOp",EDGE,"E16.6.4.0")}),1.0]])]});
            var Q9;
            Q9=makeQuery(id+"F2.imprint","IMPRINT",FACE,{"disambiguationData":[TD([[makeQuery(id+"F2.imprint","IMPRINT",EDGE,{"derivedFrom":sQuery(id+"F2.wireOp",EDGE,"E16.3.3.0")}),1.0]])]});
            var Q10;
            Q10=makeQuery(id+"F2.imprint","IMPRINT",FACE,{"disambiguationData":[TD([[makeQuery(id+"F2.imprint","IMPRINT",EDGE,{"derivedFrom":sQuery(id+"F2.wireOp",EDGE,"E16.26.0.0")}),1.0]])]});
            var Q11;
            Q11=makeQuery(id+"F2.imprint","IMPRINT",FACE,{"disambiguationData":[TD([[makeQuery(id+"F2.imprint","IMPRINT",EDGE,{"derivedFrom":sQuery(id+"F2.wireOp",EDGE,"E16.22.4.0")}),1.0]])]});
            var Q12;
            Q12=makeQuery(id+"F2.imprint","IMPRINT",FACE,{"disambiguationData":[TD([[makeQuery(id+"F2.imprint","IMPRINT",EDGE,{"derivedFrom":sQuery(id+"F2.wireOp",EDGE,"E16.8.1.0")}),1.0]])]});
            var Q13;
            Q13=makeQuery(id+"F2.imprint","IMPRINT",FACE,{"disambiguationData":[TD([[makeQuery(id+"F2.imprint","IMPRINT",EDGE,{"derivedFrom":sQuery(id+"F2.wireOp",EDGE,"E16.13.2.0")}),1.0]])]});
            var Q14;
            Q14=makeQuery(id+"F2.imprint","IMPRINT",FACE,{"disambiguationData":[TD([[makeQuery(id+"F2.imprint","IMPRINT",EDGE,{"derivedFrom":sQuery(id+"F2.wireOp",EDGE,"E16.5.0.0")}),1.0]])]});
            var Q15;
            Q15=makeQuery(id+"F2.imprint","IMPRINT",FACE,{"disambiguationData":[TD([[makeQuery(id+"F2.imprint","IMPRINT",EDGE,{"derivedFrom":sQuery(id+"F2.wireOp",EDGE,"E16.10.1.0")}),1.0]])]});
            var Q16;
            Q16=makeQuery(id+"F2.imprint","IMPRINT",FACE,{"disambiguationData":[TD([[makeQuery(id+"F2.imprint","IMPRINT",EDGE,{"derivedFrom":sQuery(id+"F2.wireOp",EDGE,"E16.7.0.0")}),1.0]])]});
            var Q17;
            Q17=makeQuery(id+"F2.imprint","IMPRINT",FACE,{"disambiguationData":[TD([[makeQuery(id+"F2.imprint","IMPRINT",EDGE,{"derivedFrom":sQuery(id+"F2.wireOp",EDGE,"E16.3.4.0")}),1.0]])]});
            var Q18;
            Q18=makeQuery(id+"F2.imprint","IMPRINT",FACE,{"disambiguationData":[TD([[makeQuery(id+"F2.imprint","IMPRINT",EDGE,{"derivedFrom":sQuery(id+"F2.wireOp",EDGE,"E16.26.1.0")}),1.0]])]});
            var Q19;
            Q19=makeQuery(id+"F2.imprint","IMPRINT",FACE,{"disambiguationData":[TD([[makeQuery(id+"F2.imprint","IMPRINT",EDGE,{"derivedFrom":sQuery(id+"F2.wireOp",EDGE,"E16.21.0.0")}),1.0]])]});
            var Q20;
            Q20=makeQuery(id+"F2.imprint","IMPRINT",FACE,{"disambiguationData":[TD([[makeQuery(id+"F2.imprint","IMPRINT",EDGE,{"derivedFrom":sQuery(id+"F2.wireOp",EDGE,"E16.23.0.0")}),1.0]])]});
            var Q21;
            Q21=makeQuery(id+"F2.imprint","IMPRINT",FACE,{"disambiguationData":[TD([[makeQuery(id+"F2.imprint","IMPRINT",EDGE,{"derivedFrom":sQuery(id+"F2.wireOp",EDGE,"E16.17.4.0")}),1.0]])]});
            var Q22;
            Q22=makeQuery(id+"F2.imprint","IMPRINT",FACE,{"disambiguationData":[TD([[makeQuery(id+"F2.imprint","IMPRINT",EDGE,{"derivedFrom":sQuery(id+"F2.wireOp",EDGE,"E16.19.4.0")}),1.0]])]});
            var Q23;
            Q23=makeQuery(id+"F2.imprint","IMPRINT",FACE,{"disambiguationData":[TD([[makeQuery(id+"F2.imprint","IMPRINT",EDGE,{"derivedFrom":sQuery(id+"F2.wireOp",EDGE,"E16.14.3.0")}),1.0]])]});
            var Q24;
            Q24=makeQuery(id+"F2.imprint","IMPRINT",FACE,{"disambiguationData":[TD([[makeQuery(id+"F2.imprint","IMPRINT",EDGE,{"derivedFrom":sQuery(id+"F2.wireOp",EDGE,"E16.16.3.0")}),1.0]])]});
            var Q25;
            Q25=makeQuery(id+"F2.imprint","IMPRINT",FACE,{"disambiguationData":[TD([[makeQuery(id+"F2.imprint","IMPRINT",EDGE,{"derivedFrom":sQuery(id+"F2.wireOp",EDGE,"E16.11.2.0")}),1.0]])]});
            var Q26;
            Q26=makeQuery(id+"F2.imprint","IMPRINT",FACE,{"disambiguationData":[TD([[makeQuery(id+"F2.imprint","IMPRINT",EDGE,{"derivedFrom":sQuery(id+"F2.wireOp",EDGE,"E16.24.1.0")}),1.0]])]});
            var Q27;
            Q27=makeQuery(id+"F2.imprint","IMPRINT",FACE,{"disambiguationData":[TD([[makeQuery(id+"F2.imprint","IMPRINT",EDGE,{"derivedFrom":sQuery(id+"F2.wireOp",EDGE,"E16.13.3.0")}),1.0]])]});
            var Q28;
            Q28=makeQuery(id+"F2.imprint","IMPRINT",FACE,{"disambiguationData":[TD([[makeQuery(id+"F2.imprint","IMPRINT",EDGE,{"derivedFrom":sQuery(id+"F2.wireOp",EDGE,"E16.10.2.0")}),1.0]])]});
            var Q29;
            Q29=makeQuery(id+"F2.imprint","IMPRINT",FACE,{"disambiguationData":[TD([[makeQuery(id+"F2.imprint","IMPRINT",EDGE,{"derivedFrom":sQuery(id+"F2.wireOp",EDGE,"E16.7.1.0")}),1.0]])]});
            var Q30;
            Q30=makeQuery(id+"F2.imprint","IMPRINT",FACE,{"disambiguationData":[TD([[makeQuery(id+"F2.imprint","IMPRINT",EDGE,{"derivedFrom":sQuery(id+"F2.wireOp",EDGE,"E16.4.0.0")}),1.0]])]});
            var Q31;
            Q31=makeQuery(id+"F2.imprint","IMPRINT",FACE,{"disambiguationData":[TD([[makeQuery(id+"F2.imprint","IMPRINT",EDGE,{"derivedFrom":sQuery(id+"F2.wireOp",EDGE,"E16.20.0.0")}),1.0]])]});
            var Q32;
            Q32=makeQuery(id+"F2.imprint","IMPRINT",FACE,{"disambiguationData":[TD([[makeQuery(id+"F2.imprint","IMPRINT",EDGE,{"derivedFrom":sQuery(id+"F2.wireOp",EDGE,"E16.16.4.0")}),1.0]])]});
            var Q33;
            Q33=makeQuery(id+"F2.imprint","IMPRINT",FACE,{"disambiguationData":[TD([[makeQuery(id+"F2.imprint","IMPRINT",EDGE,{"derivedFrom":sQuery(id+"F2.wireOp",EDGE,"E16.23.4.0")}),1.0]])]});
            var Q34;
            Q34=makeQuery(id+"F2.imprint","IMPRINT",FACE,{"disambiguationData":[TD([[makeQuery(id+"F2.imprint","IMPRINT",EDGE,{"derivedFrom":sQuery(id+"F2.wireOp",EDGE,"E16.20.3.0")}),1.0]])]});
            var Q35;
            Q35=makeQuery(id+"F2.imprint","IMPRINT",FACE,{"disambiguationData":[TD([[makeQuery(id+"F2.imprint","IMPRINT",EDGE,{"derivedFrom":sQuery(id+"F2.wireOp",EDGE,"E16.13.4.0")}),1.0]])]});
            var Q36;
            Q36=makeQuery(id+"F2.imprint","IMPRINT",FACE,{"disambiguationData":[TD([[makeQuery(id+"F2.imprint","IMPRINT",EDGE,{"derivedFrom":sQuery(id+"F2.wireOp",EDGE,"E16.10.3.0")}),1.0]])]});
            var Q37;
            Q37=makeQuery(id+"F2.imprint","IMPRINT",FACE,{"disambiguationData":[TD([[makeQuery(id+"F2.imprint","IMPRINT",EDGE,{"derivedFrom":sQuery(id+"F2.wireOp",EDGE,"E16.7.2.0")}),1.0]])]});
            var Q38;
            Q38=makeQuery(id+"F2.imprint","IMPRINT",FACE,{"disambiguationData":[TD([[makeQuery(id+"F2.imprint","IMPRINT",EDGE,{"derivedFrom":sQuery(id+"F2.wireOp",EDGE,"E16.4.1.0")}),1.0]])]});
            var Q39;
            Q39=makeQuery(id+"F2.imprint","IMPRINT",FACE,{"disambiguationData":[TD([[makeQuery(id+"F2.imprint","IMPRINT",EDGE,{"derivedFrom":sQuery(id+"F2.wireOp",EDGE,"E16.26.3.0")}),1.0]])]});
            var Q40;
            Q40=makeQuery(id+"F2.imprint","IMPRINT",FACE,{"disambiguationData":[TD([[makeQuery(id+"F2.imprint","IMPRINT",EDGE,{"derivedFrom":sQuery(id+"F2.wireOp",EDGE,"E16.23.2.0")}),1.0]])]});
            var Q41;
            Q41=makeQuery(id+"F2.imprint","IMPRINT",FACE,{"disambiguationData":[TD([[makeQuery(id+"F2.imprint","IMPRINT",EDGE,{"derivedFrom":sQuery(id+"F2.wireOp",EDGE,"E16.20.1.0")}),1.0]])]});
            var Q42;
            Q42=makeQuery(id+"F2.imprint","IMPRINT",FACE,{"disambiguationData":[TD([[makeQuery(id+"F2.imprint","IMPRINT",EDGE,{"derivedFrom":sQuery(id+"F2.wireOp",EDGE,"E16.17.0.0")}),1.0]])]});
            var Q43;
            Q43=makeQuery(id+"F2.imprint","IMPRINT",FACE,{"disambiguationData":[TD([[makeQuery(id+"F2.imprint","IMPRINT",EDGE,{"derivedFrom":sQuery(id+"F2.wireOp",EDGE,"E16.17.3.0")}),1.0]])]});
            var Q44;
            Q44=makeQuery(id+"F2.imprint","IMPRINT",FACE,{"disambiguationData":[TD([[makeQuery(id+"F2.imprint","IMPRINT",EDGE,{"derivedFrom":sQuery(id+"F2.wireOp",EDGE,"E16.24.0.0")}),1.0]])]});
            var Q45;
            Q45=makeQuery(id+"F2.imprint","IMPRINT",FACE,{"disambiguationData":[TD([[makeQuery(id+"F2.imprint","IMPRINT",EDGE,{"derivedFrom":sQuery(id+"F2.wireOp",EDGE,"E16.20.4.0")}),1.0]])]});
            var Q46;
            Q46=makeQuery(id+"F2.imprint","IMPRINT",FACE,{"disambiguationData":[TD([[makeQuery(id+"F2.imprint","IMPRINT",EDGE,{"derivedFrom":sQuery(id+"F2.wireOp",EDGE,"E16.14.0.0")}),1.0]])]});
            var Q47;
            Q47=makeQuery(id+"F2.imprint","IMPRINT",FACE,{"disambiguationData":[TD([[makeQuery(id+"F2.imprint","IMPRINT",EDGE,{"derivedFrom":sQuery(id+"F2.wireOp",EDGE,"E16.26.4.0")}),1.0]])]});
            var Q48;
            Q48=makeQuery(id+"F2.imprint","IMPRINT",FACE,{"disambiguationData":[TD([[makeQuery(id+"F2.imprint","IMPRINT",EDGE,{"derivedFrom":sQuery(id+"F2.wireOp",EDGE,"E16.23.3.0")}),1.0]])]});
            var Q49;
            Q49=makeQuery(id+"F2.imprint","IMPRINT",FACE,{"disambiguationData":[TD([[makeQuery(id+"F2.imprint","IMPRINT",EDGE,{"derivedFrom":sQuery(id+"F2.wireOp",EDGE,"E16.20.2.0")}),1.0]])]});
            var Q50;
            Q50=makeQuery(id+"F2.imprint","IMPRINT",FACE,{"disambiguationData":[TD([[makeQuery(id+"F2.imprint","IMPRINT",EDGE,{"derivedFrom":sQuery(id+"F2.wireOp",EDGE,"E16.17.1.0")}),1.0]])]});
            var Q51;
            Q51=makeQuery(id+"F2.imprint","IMPRINT",FACE,{"disambiguationData":[TD([[makeQuery(id+"F2.imprint","IMPRINT",EDGE,{"derivedFrom":sQuery(id+"F2.wireOp",EDGE,"E16.5.1.0")}),1.0]])]});
            var Q52;
            Q52=makeQuery(id+"F2.imprint","IMPRINT",FACE,{"disambiguationData":[TD([[makeQuery(id+"F2.imprint","IMPRINT",EDGE,{"derivedFrom":sQuery(id+"F2.wireOp",EDGE,"E16.2.0.0")}),1.0]])]});
            var Q53;
            Q53=makeQuery(id+"F2.imprint","IMPRINT",FACE,{"disambiguationData":[TD([[makeQuery(id+"F2.imprint","IMPRINT",EDGE,{"derivedFrom":sQuery(id+"F2.wireOp",EDGE,"E16.14.4.0")}),1.0]])]});
            var Q54;
            Q54=makeQuery(id+"F2.imprint","IMPRINT",FACE,{"disambiguationData":[TD([[makeQuery(id+"F2.imprint","IMPRINT",EDGE,{"derivedFrom":sQuery(id+"F2.wireOp",EDGE,"E16.11.3.0")}),1.0]])]});
            var Q55;
            Q55=makeQuery(id+"F2.imprint","IMPRINT",FACE,{"disambiguationData":[TD([[makeQuery(id+"F2.imprint","IMPRINT",EDGE,{"derivedFrom":sQuery(id+"F2.wireOp",EDGE,"E16.8.2.0")}),1.0]])]});
            var Q56;
            Q56=makeQuery(id+"F2.imprint","IMPRINT",FACE,{"disambiguationData":[TD([[makeQuery(id+"F2.imprint","IMPRINT",EDGE,{"derivedFrom":sQuery(id+"F2.wireOp",EDGE,"E16.5.2.0")}),1.0]])]});
            var Q57;
            Q57=makeQuery(id+"F2.imprint","IMPRINT",FACE,{"disambiguationData":[TD([[makeQuery(id+"F2.imprint","IMPRINT",EDGE,{"derivedFrom":sQuery(id+"F2.wireOp",EDGE,"E16.2.1.0")}),1.0]])]});
            var Q58;
            Q58=makeQuery(id+"F2.imprint","IMPRINT",FACE,{"disambiguationData":[TD([[makeQuery(id+"F2.imprint","IMPRINT",EDGE,{"derivedFrom":sQuery(id+"F2.wireOp",EDGE,"E16.11.4.0")}),1.0]])]});
            var Q59;
            Q59=makeQuery(id+"F2.imprint","IMPRINT",FACE,{"disambiguationData":[TD([[makeQuery(id+"F2.imprint","IMPRINT",EDGE,{"derivedFrom":sQuery(id+"F2.wireOp",EDGE,"E16.8.3.0")}),1.0]])]});
            var Q60;
            Q60=makeQuery(id+"F2.imprint","IMPRINT",FACE,{"disambiguationData":[TD([[makeQuery(id+"F2.imprint","IMPRINT",EDGE,{"derivedFrom":sQuery(id+"F2.wireOp",EDGE,"E16.5.3.0")}),1.0]])]});
            var Q61;
            Q61=makeQuery(id+"F2.imprint","IMPRINT",FACE,{"disambiguationData":[TD([[makeQuery(id+"F2.imprint","IMPRINT",EDGE,{"derivedFrom":sQuery(id+"F2.wireOp",EDGE,"E16.2.2.0")}),1.0]])]});
            var Q62;
            Q62=makeQuery(id+"F2.imprint","IMPRINT",FACE,{"disambiguationData":[TD([[makeQuery(id+"F2.imprint","IMPRINT",EDGE,{"derivedFrom":sQuery(id+"F2.wireOp",EDGE,"E16.18.2.0")}),1.0]])]});
            var Q63;
            Q63=makeQuery(id+"F2.imprint","IMPRINT",FACE,{"disambiguationData":[TD([[makeQuery(id+"F2.imprint","IMPRINT",EDGE,{"derivedFrom":sQuery(id+"F2.wireOp",EDGE,"E16.15.1.0")}),1.0]])]});
            var Q64;
            Q64=makeQuery(id+"F2.imprint","IMPRINT",FACE,{"disambiguationData":[TD([[makeQuery(id+"F2.imprint","IMPRINT",EDGE,{"derivedFrom":sQuery(id+"F2.wireOp",EDGE,"E16.12.0.0")}),1.0]])]});
            var Q65;
            Q65=makeQuery(id+"F2.imprint","IMPRINT",FACE,{"disambiguationData":[TD([[makeQuery(id+"F2.imprint","IMPRINT",EDGE,{"derivedFrom":sQuery(id+"F2.wireOp",EDGE,"E16.8.4.0")}),1.0]])]});
            var Q66;
            Q66=makeQuery(id+"F2.imprint","IMPRINT",FACE,{"disambiguationData":[TD([[makeQuery(id+"F2.imprint","IMPRINT",EDGE,{"derivedFrom":sQuery(id+"F2.wireOp",EDGE,"E16.24.4.0")}),1.0]])]});
            var Q67;
            Q67=makeQuery(id+"F2.imprint","IMPRINT",FACE,{"disambiguationData":[TD([[makeQuery(id+"F2.imprint","IMPRINT",EDGE,{"derivedFrom":sQuery(id+"F2.wireOp",EDGE,"E16.21.3.0")}),1.0]])]});
            var Q68;
            Q68=makeQuery(id+"F2.imprint","IMPRINT",FACE,{"disambiguationData":[TD([[makeQuery(id+"F2.imprint","IMPRINT",EDGE,{"derivedFrom":sQuery(id+"F2.wireOp",EDGE,"E16.1.4.0")}),1.0]])]});
            var Q69;
            Q69=makeQuery(id+"F2.imprint","IMPRINT",FACE,{"disambiguationData":[TD([[makeQuery(id+"F2.imprint","IMPRINT",EDGE,{"derivedFrom":sQuery(id+"F2.wireOp",EDGE,"E15")}),1.0]])]});
            var Q70;
            Q70=makeQuery(id+"F2.imprint","IMPRINT",FACE,{"disambiguationData":[TD([[makeQuery(id+"F2.imprint","IMPRINT",EDGE,{"derivedFrom":sQuery(id+"F2.wireOp",EDGE,"E16.0.1.0")}),1.0]])]});
            var Q71;
            Q71=makeQuery(id+"F2.imprint","IMPRINT",FACE,{"disambiguationData":[TD([[makeQuery(id+"F2.imprint","IMPRINT",EDGE,{"derivedFrom":sQuery(id+"F2.wireOp",EDGE,"E16.0.2.0")}),1.0]])]});
            var Q72;
            Q72=makeQuery(id+"F2.imprint","IMPRINT",FACE,{"disambiguationData":[TD([[makeQuery(id+"F2.imprint","IMPRINT",EDGE,{"derivedFrom":sQuery(id+"F2.wireOp",EDGE,"E16.0.3.0")}),1.0]])]});
            var Q73;
            Q73=makeQuery(id+"F2.imprint","IMPRINT",FACE,{"disambiguationData":[TD([[makeQuery(id+"F2.imprint","IMPRINT",EDGE,{"derivedFrom":sQuery(id+"F2.wireOp",EDGE,"E16.0.4.0")}),1.0]])]});
            var Q74;
            Q74=makeQuery(id+"F2.imprint","IMPRINT",FACE,{"disambiguationData":[TD([[makeQuery(id+"F2.imprint","IMPRINT",EDGE,{"derivedFrom":sQuery(id+"F2.wireOp",EDGE,"E16.1.0.0")}),1.0]])]});
            var Q75;
            Q75=makeQuery(id+"F2.imprint","IMPRINT",FACE,{"disambiguationData":[TD([[makeQuery(id+"F2.imprint","IMPRINT",EDGE,{"derivedFrom":sQuery(id+"F2.wireOp",EDGE,"E16.18.3.0")}),1.0]])]});
            var Q76;
            Q76=makeQuery(id+"F2.imprint","IMPRINT",FACE,{"disambiguationData":[TD([[makeQuery(id+"F2.imprint","IMPRINT",EDGE,{"derivedFrom":sQuery(id+"F2.wireOp",EDGE,"E16.15.2.0")}),1.0]])]});
            var Q77;
            Q77=makeQuery(id+"F2.imprint","IMPRINT",FACE,{"disambiguationData":[TD([[makeQuery(id+"F2.imprint","IMPRINT",EDGE,{"derivedFrom":sQuery(id+"F2.wireOp",EDGE,"E16.12.1.0")}),1.0]])]});
            var Q78;
            Q78=makeQuery(id+"F2.imprint","IMPRINT",FACE,{"disambiguationData":[TD([[makeQuery(id+"F2.imprint","IMPRINT",EDGE,{"derivedFrom":sQuery(id+"F2.wireOp",EDGE,"E16.9.0.0")}),1.0]])]});
            var Q79;
            Q79=makeQuery(id+"F2.imprint","IMPRINT",FACE,{"disambiguationData":[TD([[makeQuery(id+"F2.imprint","IMPRINT",EDGE,{"derivedFrom":sQuery(id+"F2.wireOp",EDGE,"E16.25.0.0")}),1.0]])]});
            var Q80;
            Q80=makeQuery(id+"F2.imprint","IMPRINT",FACE,{"disambiguationData":[TD([[makeQuery(id+"F2.imprint","IMPRINT",EDGE,{"derivedFrom":sQuery(id+"F2.wireOp",EDGE,"E16.21.4.0")}),1.0]])]});
            var Q81;
            Q81=makeQuery(id+"F2.imprint","IMPRINT",FACE,{"disambiguationData":[TD([[makeQuery(id+"F2.imprint","IMPRINT",EDGE,{"derivedFrom":sQuery(id+"F2.wireOp",EDGE,"E16.6.0.0")}),1.0]])]});
            var Q82;
            Q82=makeQuery(id+"F2.imprint","IMPRINT",FACE,{"disambiguationData":[TD([[makeQuery(id+"F2.imprint","IMPRINT",EDGE,{"derivedFrom":sQuery(id+"F2.wireOp",EDGE,"E16.2.4.0")}),1.0]])]});
            var Q83;
            Q83=makeQuery(id+"F2.imprint","IMPRINT",FACE,{"disambiguationData":[TD([[makeQuery(id+"F2.imprint","IMPRINT",EDGE,{"derivedFrom":sQuery(id+"F2.wireOp",EDGE,"E16.18.4.0")}),1.0]])]});
            var Q84;
            Q84=makeQuery(id+"F2.imprint","IMPRINT",FACE,{"disambiguationData":[TD([[makeQuery(id+"F2.imprint","IMPRINT",EDGE,{"derivedFrom":sQuery(id+"F2.wireOp",EDGE,"E16.15.3.0")}),1.0]])]});
            var Q85;
            Q85=makeQuery(id+"F2.imprint","IMPRINT",FACE,{"disambiguationData":[TD([[makeQuery(id+"F2.imprint","IMPRINT",EDGE,{"derivedFrom":sQuery(id+"F2.wireOp",EDGE,"E16.12.2.0")}),1.0]])]});
            var Q86;
            Q86=makeQuery(id+"F2.imprint","IMPRINT",FACE,{"disambiguationData":[TD([[makeQuery(id+"F2.imprint","IMPRINT",EDGE,{"derivedFrom":sQuery(id+"F2.wireOp",EDGE,"E16.9.1.0")}),1.0]])]});
            var Q87;
            Q87=makeQuery(id+"F2.imprint","IMPRINT",FACE,{"disambiguationData":[TD([[makeQuery(id+"F2.imprint","IMPRINT",EDGE,{"derivedFrom":sQuery(id+"F2.wireOp",EDGE,"E16.25.1.0")}),1.0]])]});
            var Q88;
            Q88=makeQuery(id+"F2.imprint","IMPRINT",FACE,{"disambiguationData":[TD([[makeQuery(id+"F2.imprint","IMPRINT",EDGE,{"derivedFrom":sQuery(id+"F2.wireOp",EDGE,"E16.22.0.0")}),1.0]])]});
            var Q89;
            Q89=makeQuery(id+"F2.imprint","IMPRINT",FACE,{"disambiguationData":[TD([[makeQuery(id+"F2.imprint","IMPRINT",EDGE,{"derivedFrom":sQuery(id+"F2.wireOp",EDGE,"E16.15.4.0")}),1.0]])]});
            var Q90;
            Q90=makeQuery(id+"F2.imprint","IMPRINT",FACE,{"disambiguationData":[TD([[makeQuery(id+"F2.imprint","IMPRINT",EDGE,{"derivedFrom":sQuery(id+"F2.wireOp",EDGE,"E16.12.4.0")}),1.0]])]});
            var Q91;
            Q91=makeQuery(id+"F2.imprint","IMPRINT",FACE,{"disambiguationData":[TD([[makeQuery(id+"F2.imprint","IMPRINT",EDGE,{"derivedFrom":sQuery(id+"F2.wireOp",EDGE,"E16.9.3.0")}),1.0]])]});
            var Q92;
            Q92=makeQuery(id+"F2.imprint","IMPRINT",FACE,{"disambiguationData":[TD([[makeQuery(id+"F2.imprint","IMPRINT",EDGE,{"derivedFrom":sQuery(id+"F2.wireOp",EDGE,"E16.6.2.0")}),1.0]])]});
            var Q93;
            Q93=makeQuery(id+"F2.imprint","IMPRINT",FACE,{"disambiguationData":[TD([[makeQuery(id+"F2.imprint","IMPRINT",EDGE,{"derivedFrom":sQuery(id+"F2.wireOp",EDGE,"E16.3.1.0")}),1.0]])]});
            var Q94;
            Q94=makeQuery(id+"F2.imprint","IMPRINT",FACE,{"disambiguationData":[TD([[makeQuery(id+"F2.imprint","IMPRINT",EDGE,{"derivedFrom":sQuery(id+"F2.wireOp",EDGE,"E16.25.3.0")}),1.0]])]});
            var Q95;
            Q95=makeQuery(id+"F2.imprint","IMPRINT",FACE,{"disambiguationData":[TD([[makeQuery(id+"F2.imprint","IMPRINT",EDGE,{"derivedFrom":sQuery(id+"F2.wireOp",EDGE,"E16.22.2.0")}),1.0]])]});
            var Q96;
            Q96=makeQuery(id+"F2.imprint","IMPRINT",FACE,{"disambiguationData":[TD([[makeQuery(id+"F2.imprint","IMPRINT",EDGE,{"derivedFrom":sQuery(id+"F2.wireOp",EDGE,"E16.19.1.0")}),1.0]])]});
            var Q97;
            Q97=makeQuery(id+"F2.imprint","IMPRINT",FACE,{"disambiguationData":[TD([[makeQuery(id+"F2.imprint","IMPRINT",EDGE,{"derivedFrom":sQuery(id+"F2.wireOp",EDGE,"E16.16.0.0")}),1.0]])]});
            var Q98;
            Q98=makeQuery(id+"F2.imprint","IMPRINT",FACE,{"disambiguationData":[TD([[makeQuery(id+"F2.imprint","IMPRINT",EDGE,{"derivedFrom":sQuery(id+"F2.wireOp",EDGE,"E16.25.4.0")}),1.0]])]});
            var Q99;
            Q99=makeQuery(id+"F2.imprint","IMPRINT",FACE,{"disambiguationData":[TD([[makeQuery(id+"F2.imprint","IMPRINT",EDGE,{"derivedFrom":sQuery(id+"F2.wireOp",EDGE,"E16.22.3.0")}),1.0]])]});
            var Q100;
            Q100=makeQuery(id+"F2.imprint","IMPRINT",FACE,{"disambiguationData":[TD([[makeQuery(id+"F2.imprint","IMPRINT",EDGE,{"derivedFrom":sQuery(id+"F2.wireOp",EDGE,"E16.19.2.0")}),1.0]])]});
            var Q101;
            Q101=makeQuery(id+"F2.imprint","IMPRINT",FACE,{"disambiguationData":[TD([[makeQuery(id+"F2.imprint","IMPRINT",EDGE,{"derivedFrom":sQuery(id+"F2.wireOp",EDGE,"E16.16.1.0")}),1.0]])]});
            var Q102;
            Q102=makeQuery(id+"F2.imprint","IMPRINT",FACE,{"disambiguationData":[TD([[makeQuery(id+"F2.imprint","IMPRINT",EDGE,{"derivedFrom":sQuery(id+"F2.wireOp",EDGE,"E16.13.0.0")}),1.0]])]});
            var Q103;
            Q103=makeQuery(id+"F2.imprint","IMPRINT",FACE,{"disambiguationData":[TD([[makeQuery(id+"F2.imprint","IMPRINT",EDGE,{"derivedFrom":sQuery(id+"F2.wireOp",EDGE,"E16.9.4.0")}),1.0]])]});
            var Q104;
            Q104=makeQuery(id+"F2.imprint","IMPRINT",FACE,{"disambiguationData":[TD([[makeQuery(id+"F2.imprint","IMPRINT",EDGE,{"derivedFrom":sQuery(id+"F2.wireOp",EDGE,"E16.6.3.0")}),1.0]])]});
            var Q105;
            Q105=makeQuery(id+"F2.imprint","IMPRINT",FACE,{"disambiguationData":[TD([[makeQuery(id+"F2.imprint","IMPRINT",EDGE,{"derivedFrom":sQuery(id+"F2.wireOp",EDGE,"E16.13.1.0")}),1.0]])]});
            var Q106;
            Q106=makeQuery(id+"F2.imprint","IMPRINT",FACE,{"disambiguationData":[TD([[makeQuery(id+"F2.imprint","IMPRINT",EDGE,{"derivedFrom":sQuery(id+"F2.wireOp",EDGE,"E16.10.0.0")}),1.0]])]});
            var Q107;
            Q107=makeQuery(id+"F2.imprint","IMPRINT",FACE,{"disambiguationData":[TD([[makeQuery(id+"F2.imprint","IMPRINT",EDGE,{"derivedFrom":sQuery(id+"F2.wireOp",EDGE,"E16.19.3.0")}),1.0]])]});
            var Q108;
            Q108=makeQuery(id+"F2.imprint","IMPRINT",FACE,{"disambiguationData":[TD([[makeQuery(id+"F2.imprint","IMPRINT",EDGE,{"derivedFrom":sQuery(id+"F2.wireOp",EDGE,"E16.16.2.0")}),1.0]])]});
            var Q109;
            Q109=makeQuery(id+"F2.imprint","IMPRINT",FACE,{"disambiguationData":[TD([[makeQuery(id+"F2.imprint","IMPRINT",EDGE,{"derivedFrom":sQuery(id+"F2.wireOp",EDGE,"E16.26.2.0")}),1.0]])]});
            var Q110;
            Q110=makeQuery(id+"F2.imprint","IMPRINT",FACE,{"disambiguationData":[TD([[makeQuery(id+"F2.imprint","IMPRINT",EDGE,{"derivedFrom":sQuery(id+"F2.wireOp",EDGE,"E16.23.1.0")}),1.0]])]});
            var Q111;
            Q111=makeQuery(id+"F2.imprint","IMPRINT",FACE,{"disambiguationData":[TD([[makeQuery(id+"F2.imprint","IMPRINT",EDGE,{"derivedFrom":sQuery(id+"F2.wireOp",EDGE,"E16.4.3.0")}),1.0]])]});
            var Q112;
            Q112=makeQuery(id+"F2.imprint","IMPRINT",FACE,{"disambiguationData":[TD([[makeQuery(id+"F2.imprint","IMPRINT",EDGE,{"derivedFrom":sQuery(id+"F2.wireOp",EDGE,"E16.17.2.0")}),1.0]])]});
            var Q113;
            Q113=makeQuery(id+"F2.imprint","IMPRINT",FACE,{"disambiguationData":[TD([[makeQuery(id+"F2.imprint","IMPRINT",EDGE,{"derivedFrom":sQuery(id+"F2.wireOp",EDGE,"E16.14.1.0")}),1.0]])]});
            var Q114;
            Q114=makeQuery(id+"F2.imprint","IMPRINT",FACE,{"disambiguationData":[TD([[makeQuery(id+"F2.imprint","IMPRINT",EDGE,{"derivedFrom":sQuery(id+"F2.wireOp",EDGE,"E16.11.0.0")}),1.0]])]});
            var Q115;
            Q115=makeQuery(id+"F2.imprint","IMPRINT",FACE,{"disambiguationData":[TD([[makeQuery(id+"F2.imprint","IMPRINT",EDGE,{"derivedFrom":sQuery(id+"F2.wireOp",EDGE,"E16.7.4.0")}),1.0]])]});
            var Q116;
            Q116=makeQuery(id+"F2.imprint","IMPRINT",FACE,{"disambiguationData":[TD([[makeQuery(id+"F2.imprint","IMPRINT",EDGE,{"derivedFrom":sQuery(id+"F2.wireOp",EDGE,"E16.4.4.0")}),1.0]])]});
            var Q117;
            Q117=makeQuery(id+"F2.imprint","IMPRINT",FACE,{"disambiguationData":[TD([[makeQuery(id+"F2.imprint","IMPRINT",EDGE,{"derivedFrom":sQuery(id+"F2.wireOp",EDGE,"E16.14.2.0")}),1.0]])]});
            var Q118;
            Q118=makeQuery(id+"F2.imprint","IMPRINT",FACE,{"disambiguationData":[TD([[makeQuery(id+"F2.imprint","IMPRINT",EDGE,{"derivedFrom":sQuery(id+"F2.wireOp",EDGE,"E16.11.1.0")}),1.0]])]});
            var Q119;
            Q119=makeQuery(id+"F2.imprint","IMPRINT",FACE,{"disambiguationData":[TD([[makeQuery(id+"F2.imprint","IMPRINT",EDGE,{"derivedFrom":sQuery(id+"F2.wireOp",EDGE,"E16.8.0.0")}),1.0]])]});
            var Q120;
            Q120=makeQuery(id+"F2.imprint","IMPRINT",FACE,{"disambiguationData":[TD([[makeQuery(id+"F2.imprint","IMPRINT",EDGE,{"derivedFrom":sQuery(id+"F2.wireOp",EDGE,"E16.10.4.0")}),1.0]])]});
            var Q121;
            Q121=makeQuery(id+"F2.imprint","IMPRINT",FACE,{"disambiguationData":[TD([[makeQuery(id+"F2.imprint","IMPRINT",EDGE,{"derivedFrom":sQuery(id+"F2.wireOp",EDGE,"E16.7.3.0")}),1.0]])]});
            var Q122;
            Q122=makeQuery(id+"F2.imprint","IMPRINT",FACE,{"disambiguationData":[TD([[makeQuery(id+"F2.imprint","IMPRINT",EDGE,{"derivedFrom":sQuery(id+"F2.wireOp",EDGE,"E16.4.2.0")}),1.0]])]});
            var Q123;
            Q123=makeQuery(id+"F2.imprint","IMPRINT",FACE,{"disambiguationData":[TD([[makeQuery(id+"F2.imprint","IMPRINT",EDGE,{"derivedFrom":sQuery(id+"F2.wireOp",EDGE,"E16.18.0.0")}),1.0]])]});
            var Q124;
            Q124=makeQuery(id+"F2.imprint","IMPRINT",FACE,{"disambiguationData":[TD([[makeQuery(id+"F2.imprint","IMPRINT",EDGE,{"derivedFrom":sQuery(id+"F2.wireOp",EDGE,"E16.24.2.0")}),1.0]])]});
            var Q125;
            Q125=makeQuery(id+"F2.imprint","IMPRINT",FACE,{"disambiguationData":[TD([[makeQuery(id+"F2.imprint","IMPRINT",EDGE,{"derivedFrom":sQuery(id+"F2.wireOp",EDGE,"E16.21.1.0")}),1.0]])]});
            var Q126;
            Q126=makeQuery(id+"F2.imprint","IMPRINT",FACE,{"disambiguationData":[TD([[makeQuery(id+"F2.imprint","IMPRINT",EDGE,{"derivedFrom":sQuery(id+"F2.wireOp",EDGE,"E16.18.1.0")}),1.0]])]});
            var Q127;
            Q127=makeQuery(id+"F2.imprint","IMPRINT",FACE,{"disambiguationData":[TD([[makeQuery(id+"F2.imprint","IMPRINT",EDGE,{"derivedFrom":sQuery(id+"F2.wireOp",EDGE,"E16.15.0.0")}),1.0]])]});
            var Q128;
            Q128=makeQuery(id+"F2.imprint","IMPRINT",FACE,{"disambiguationData":[TD([[makeQuery(id+"F2.imprint","IMPRINT",EDGE,{"derivedFrom":sQuery(id+"F2.wireOp",EDGE,"E16.24.3.0")}),1.0]])]});
            var Q129;
            Q129=makeQuery(id+"F2.imprint","IMPRINT",FACE,{"disambiguationData":[TD([[makeQuery(id+"F2.imprint","IMPRINT",EDGE,{"derivedFrom":sQuery(id+"F2.wireOp",EDGE,"E16.21.2.0")}),1.0]])]});
            var Q130;
            Q130=makeQuery(id+"F2.imprint","IMPRINT",FACE,{"disambiguationData":[TD([[makeQuery(id+"F2.imprint","IMPRINT",EDGE,{"derivedFrom":sQuery(id+"F2.wireOp",EDGE,"E16.1.2.0")}),1.0]])]});
            var Q131;
            Q131=makeQuery(id+"F2.imprint","IMPRINT",FACE,{"disambiguationData":[TD([[makeQuery(id+"F2.imprint","IMPRINT",EDGE,{"derivedFrom":sQuery(id+"F2.wireOp",EDGE,"E16.1.3.0")}),1.0]])]});
            var Q132;
            Q132=makeQuery(id+"F2.imprint","IMPRINT",FACE,{"disambiguationData":[TD([[makeQuery(id+"F2.imprint","IMPRINT",EDGE,{"derivedFrom":sQuery(id+"F2.wireOp",EDGE,"E16.1.1.0")}),1.0]])]});
            var Q133;
            Q133=makeQuery(id+"F2.imprint","IMPRINT",FACE,{"disambiguationData":[TD([[makeQuery(id+"F2.imprint","IMPRINT",EDGE,{"derivedFrom":sQuery(id+"F2.wireOp",EDGE,"E16.5.4.0")}),1.0]])]});
            var Q134;
            Q134=makeQuery(id+"F2.imprint","IMPRINT",FACE,{"disambiguationData":[TD([[makeQuery(id+"F2.imprint","IMPRINT",EDGE,{"derivedFrom":sQuery(id+"F2.wireOp",EDGE,"E16.2.3.0")}),1.0]])]});
            extrude(context, id + "F5", {"entities" : qUnion([Q0, Q1, Q2, Q3, Q4, Q5, Q6, Q7, Q8, Q9, Q10, Q11, Q12, Q13, Q14, Q15, Q16, Q17, Q18, Q19, Q20, Q21, Q22, Q23, Q24, Q25, Q26, Q27, Q28, Q29, Q30, Q31, Q32, Q33, Q34, Q35, Q36, Q37, Q38, Q39, Q40, Q41, Q42, Q43, Q44, Q45, Q46, Q47, Q48, Q49, Q50, Q51, Q52, Q53, Q54, Q55, Q56, Q57, Q58, Q59, Q60, Q61, Q62, Q63, Q64, Q65, Q66, Q67, Q68, Q69, Q70, Q71, Q72, Q73, Q74, Q75, Q76, Q77, Q78, Q79, Q80, Q81, Q82, Q83, Q84, Q85, Q86, Q87, Q88, Q89, Q90, Q91, Q92, Q93, Q94, Q95, Q96, Q97, Q98, Q99, Q100, Q101, Q102, Q103, Q104, Q105, Q106, Q107, Q108, Q109, Q110, Q111, Q112, Q113, Q114, Q115, Q116, Q117, Q118, Q119, Q120, Q121, Q122, Q123, Q124, Q125, Q126, Q127, Q128, Q129, Q130, Q131, Q132, Q133, Q134]), "operationType" : NewBodyOperationType.ADD, "depth" : 6 * mm});
        }
        {
            var Q0;
            Q0=qCreatedBy(makeId("Top.planeOp"),FACE);
            cPlane(context, id + "F6", {"entities" : qUnion([Q0]), "cplaneType" : CPlaneType.OFFSET, "offset" : 13 * mm, "oppositeDirection" : true, "width" : 150 * mm, "height" : 150 * mm});
        }
        {
            var Q0;
            Q0=qCreatedBy(id+"F6.planeOp",FACE);
            var sketch = newSketch(context, id + "F7", { "sketchPlane" : qUnion([Q0])});
            skLineSegment(sketch, "E17.0", {"start": v(-137.86, -2.29) * mm, "end": v(-92.86, -2.29) * mm});
            skLineSegment(sketch, "E18.0", {"start": v(-137.86, -2.29) * mm, "end": v(-137.86, -37.29) * mm});
            skLineSegment(sketch, "E19.0", {"start": v(-137.86, -37.29) * mm, "end": v(-92.86, -37.29) * mm});
            skLineSegment(sketch, "E20.0", {"start": v(-92.86, -2.29) * mm, "end": v(-92.86, -37.29) * mm});
            skLineSegment(sketch, "E21.0", {"start": v(-137.86, 33.71) * mm, "end": v(-137.86, -1.29) * mm});
            skLineSegment(sketch, "E22.0", {"start": v(-92.86, 33.71) * mm, "end": v(-92.86, -1.29) * mm});
            skLineSegment(sketch, "E23.0", {"start": v(-137.86, -1.29) * mm, "end": v(-92.86, -1.29) * mm});
            skLineSegment(sketch, "E24.0", {"start": v(-137.86, 33.71) * mm, "end": v(-92.86, 33.71) * mm});
            skCircle(sketch, "E25", {"center": v(-133.96, -6.29) * mm, "radius": 1.75 * mm});
            skCircle(sketch, "E26", {"center": v(-95.86, -6.29) * mm, "radius": 1.75 * mm});
            skCircle(sketch, "E27", {"center": v(-133.96, -26.6) * mm, "radius": 1.75 * mm});
            skCircle(sketch, "E28", {"center": v(-95.86, -26.6) * mm, "radius": 1.75 * mm});
            skCircle(sketch, "E29", {"center": v(-133.96, 2.71) * mm, "radius": 1.75 * mm});
            skCircle(sketch, "E30", {"center": v(-133.96, 23.03) * mm, "radius": 1.75 * mm});
            skCircle(sketch, "E31", {"center": v(-95.86, 2.71) * mm, "radius": 1.75 * mm});
            skCircle(sketch, "E32", {"center": v(-95.86, 23.03) * mm, "radius": 1.75 * mm});
            skCircle(sketch, "E33", {"center": v(-128.36, -10.1) * mm, "radius": 1.5 * mm});
            skCircle(sketch, "E34", {"center": v(-128.36, 19.22) * mm, "radius": 1.5 * mm});
            skCircle(sketch, "E35.0.1.0", {"center": v(-128.36, 15.87) * mm, "radius": 1.5 * mm});
            skCircle(sketch, "E35.0.2.0", {"center": v(-128.36, 12.52) * mm, "radius": 1.5 * mm});
            skCircle(sketch, "E35.0.3.0", {"center": v(-128.36, 9.16) * mm, "radius": 1.5 * mm});
            skCircle(sketch, "E35.0.4.0", {"center": v(-128.36, 5.81) * mm, "radius": 1.5 * mm});
            skCircle(sketch, "E35.1.0.0", {"center": v(-125, 19.22) * mm, "radius": 1.5 * mm});
            skCircle(sketch, "E35.1.1.0", {"center": v(-125, 15.87) * mm, "radius": 1.5 * mm});
            skCircle(sketch, "E35.1.2.0", {"center": v(-125, 12.52) * mm, "radius": 1.5 * mm});
            skCircle(sketch, "E35.1.3.0", {"center": v(-125, 9.16) * mm, "radius": 1.5 * mm});
            skCircle(sketch, "E35.1.4.0", {"center": v(-125, 5.81) * mm, "radius": 1.5 * mm});
            skCircle(sketch, "E35.2.0.0", {"center": v(-121.65, 19.22) * mm, "radius": 1.5 * mm});
            skCircle(sketch, "E35.2.1.0", {"center": v(-121.65, 15.87) * mm, "radius": 1.5 * mm});
            skCircle(sketch, "E35.2.2.0", {"center": v(-121.65, 12.52) * mm, "radius": 1.5 * mm});
            skCircle(sketch, "E35.2.3.0", {"center": v(-121.65, 9.16) * mm, "radius": 1.5 * mm});
            skCircle(sketch, "E35.2.4.0", {"center": v(-121.65, 5.81) * mm, "radius": 1.5 * mm});
            skCircle(sketch, "E35.3.0.0", {"center": v(-118.3, 19.22) * mm, "radius": 1.5 * mm});
            skCircle(sketch, "E35.3.1.0", {"center": v(-118.3, 15.87) * mm, "radius": 1.5 * mm});
            skCircle(sketch, "E35.3.2.0", {"center": v(-118.3, 12.52) * mm, "radius": 1.5 * mm});
            skCircle(sketch, "E35.3.3.0", {"center": v(-118.3, 9.16) * mm, "radius": 1.5 * mm});
            skCircle(sketch, "E35.3.4.0", {"center": v(-118.3, 5.81) * mm, "radius": 1.5 * mm});
            skCircle(sketch, "E35.4.0.0", {"center": v(-114.95, 19.22) * mm, "radius": 1.5 * mm});
            skCircle(sketch, "E35.4.1.0", {"center": v(-114.95, 15.87) * mm, "radius": 1.5 * mm});
            skCircle(sketch, "E35.4.2.0", {"center": v(-114.95, 12.52) * mm, "radius": 1.5 * mm});
            skCircle(sketch, "E35.4.3.0", {"center": v(-114.95, 9.16) * mm, "radius": 1.5 * mm});
            skCircle(sketch, "E35.4.4.0", {"center": v(-114.95, 5.81) * mm, "radius": 1.5 * mm});
            skCircle(sketch, "E35.5.0.0", {"center": v(-111.6, 19.22) * mm, "radius": 1.5 * mm});
            skCircle(sketch, "E35.5.1.0", {"center": v(-111.6, 15.87) * mm, "radius": 1.5 * mm});
            skCircle(sketch, "E35.5.2.0", {"center": v(-111.6, 12.52) * mm, "radius": 1.5 * mm});
            skCircle(sketch, "E35.5.3.0", {"center": v(-111.6, 9.16) * mm, "radius": 1.5 * mm});
            skCircle(sketch, "E35.5.4.0", {"center": v(-111.6, 5.81) * mm, "radius": 1.5 * mm});
            skCircle(sketch, "E35.6.0.0", {"center": v(-108.24, 19.22) * mm, "radius": 1.5 * mm});
            skCircle(sketch, "E35.6.1.0", {"center": v(-108.24, 15.87) * mm, "radius": 1.5 * mm});
            skCircle(sketch, "E35.6.2.0", {"center": v(-108.24, 12.52) * mm, "radius": 1.5 * mm});
            skCircle(sketch, "E35.6.3.0", {"center": v(-108.24, 9.16) * mm, "radius": 1.5 * mm});
            skCircle(sketch, "E35.6.4.0", {"center": v(-108.24, 5.81) * mm, "radius": 1.5 * mm});
            skCircle(sketch, "E35.7.0.0", {"center": v(-104.9, 19.22) * mm, "radius": 1.5 * mm});
            skCircle(sketch, "E35.7.1.0", {"center": v(-104.9, 15.87) * mm, "radius": 1.5 * mm});
            skCircle(sketch, "E35.7.2.0", {"center": v(-104.9, 12.52) * mm, "radius": 1.5 * mm});
            skCircle(sketch, "E35.7.3.0", {"center": v(-104.9, 9.16) * mm, "radius": 1.5 * mm});
            skCircle(sketch, "E35.7.4.0", {"center": v(-104.9, 5.81) * mm, "radius": 1.5 * mm});
            skCircle(sketch, "E35.8.0.0", {"center": v(-101.54, 19.22) * mm, "radius": 1.5 * mm});
            skCircle(sketch, "E35.8.1.0", {"center": v(-101.54, 15.87) * mm, "radius": 1.5 * mm});
            skCircle(sketch, "E35.8.2.0", {"center": v(-101.54, 12.52) * mm, "radius": 1.5 * mm});
            skCircle(sketch, "E35.8.3.0", {"center": v(-101.54, 9.16) * mm, "radius": 1.5 * mm});
            skCircle(sketch, "E35.8.4.0", {"center": v(-101.54, 5.81) * mm, "radius": 1.5 * mm});
            skLineSegment(sketch, "E35.direction1", {"start": v(-128.36, 19.22) * mm, "end": v(-125, 19.22) * mm, "construction": true});
            skLineSegment(sketch, "E35.direction2", {"start": v(-128.36, 19.22) * mm, "end": v(-128.36, 15.87) * mm, "construction": true});
            skCircle(sketch, "E36.0.1.0", {"center": v(-128.36, -13.45) * mm, "radius": 1.5 * mm});
            skCircle(sketch, "E36.0.2.0", {"center": v(-128.36, -16.8) * mm, "radius": 1.5 * mm});
            skCircle(sketch, "E36.0.3.0", {"center": v(-128.36, -20.16) * mm, "radius": 1.5 * mm});
            skCircle(sketch, "E36.0.4.0", {"center": v(-128.36, -23.5) * mm, "radius": 1.5 * mm});
            skCircle(sketch, "E36.1.0.0", {"center": v(-125, -10.1) * mm, "radius": 1.5 * mm});
            skCircle(sketch, "E36.1.1.0", {"center": v(-125, -13.45) * mm, "radius": 1.5 * mm});
            skCircle(sketch, "E36.1.2.0", {"center": v(-125, -16.8) * mm, "radius": 1.5 * mm});
            skCircle(sketch, "E36.1.3.0", {"center": v(-125, -20.16) * mm, "radius": 1.5 * mm});
            skCircle(sketch, "E36.1.4.0", {"center": v(-125, -23.5) * mm, "radius": 1.5 * mm});
            skCircle(sketch, "E36.2.0.0", {"center": v(-121.65, -10.1) * mm, "radius": 1.5 * mm});
            skCircle(sketch, "E36.2.1.0", {"center": v(-121.65, -13.45) * mm, "radius": 1.5 * mm});
            skCircle(sketch, "E36.2.2.0", {"center": v(-121.65, -16.8) * mm, "radius": 1.5 * mm});
            skCircle(sketch, "E36.2.3.0", {"center": v(-121.65, -20.16) * mm, "radius": 1.5 * mm});
            skCircle(sketch, "E36.2.4.0", {"center": v(-121.65, -23.5) * mm, "radius": 1.5 * mm});
            skCircle(sketch, "E36.3.0.0", {"center": v(-118.3, -10.1) * mm, "radius": 1.5 * mm});
            skCircle(sketch, "E36.3.1.0", {"center": v(-118.3, -13.45) * mm, "radius": 1.5 * mm});
            skCircle(sketch, "E36.3.2.0", {"center": v(-118.3, -16.8) * mm, "radius": 1.5 * mm});
            skCircle(sketch, "E36.3.3.0", {"center": v(-118.3, -20.16) * mm, "radius": 1.5 * mm});
            skCircle(sketch, "E36.3.4.0", {"center": v(-118.3, -23.5) * mm, "radius": 1.5 * mm});
            skCircle(sketch, "E36.4.0.0", {"center": v(-114.95, -10.1) * mm, "radius": 1.5 * mm});
            skCircle(sketch, "E36.4.1.0", {"center": v(-114.95, -13.45) * mm, "radius": 1.5 * mm});
            skCircle(sketch, "E36.4.2.0", {"center": v(-114.95, -16.8) * mm, "radius": 1.5 * mm});
            skCircle(sketch, "E36.4.3.0", {"center": v(-114.95, -20.16) * mm, "radius": 1.5 * mm});
            skCircle(sketch, "E36.4.4.0", {"center": v(-114.95, -23.5) * mm, "radius": 1.5 * mm});
            skCircle(sketch, "E36.5.0.0", {"center": v(-111.6, -10.1) * mm, "radius": 1.5 * mm});
            skCircle(sketch, "E36.5.1.0", {"center": v(-111.6, -13.45) * mm, "radius": 1.5 * mm});
            skCircle(sketch, "E36.5.2.0", {"center": v(-111.6, -16.8) * mm, "radius": 1.5 * mm});
            skCircle(sketch, "E36.5.3.0", {"center": v(-111.6, -20.16) * mm, "radius": 1.5 * mm});
            skCircle(sketch, "E36.5.4.0", {"center": v(-111.6, -23.5) * mm, "radius": 1.5 * mm});
            skCircle(sketch, "E36.6.0.0", {"center": v(-108.24, -10.1) * mm, "radius": 1.5 * mm});
            skCircle(sketch, "E36.6.1.0", {"center": v(-108.24, -13.45) * mm, "radius": 1.5 * mm});
            skCircle(sketch, "E36.6.2.0", {"center": v(-108.24, -16.8) * mm, "radius": 1.5 * mm});
            skCircle(sketch, "E36.6.3.0", {"center": v(-108.24, -20.16) * mm, "radius": 1.5 * mm});
            skCircle(sketch, "E36.6.4.0", {"center": v(-108.24, -23.5) * mm, "radius": 1.5 * mm});
            skCircle(sketch, "E36.7.0.0", {"center": v(-104.9, -10.1) * mm, "radius": 1.5 * mm});
            skCircle(sketch, "E36.7.1.0", {"center": v(-104.9, -13.45) * mm, "radius": 1.5 * mm});
            skCircle(sketch, "E36.7.2.0", {"center": v(-104.9, -16.8) * mm, "radius": 1.5 * mm});
            skCircle(sketch, "E36.7.3.0", {"center": v(-104.9, -20.16) * mm, "radius": 1.5 * mm});
            skCircle(sketch, "E36.7.4.0", {"center": v(-104.9, -23.5) * mm, "radius": 1.5 * mm});
            skCircle(sketch, "E36.8.0.0", {"center": v(-101.54, -10.1) * mm, "radius": 1.5 * mm});
            skCircle(sketch, "E36.8.1.0", {"center": v(-101.54, -13.45) * mm, "radius": 1.5 * mm});
            skCircle(sketch, "E36.8.2.0", {"center": v(-101.54, -16.8) * mm, "radius": 1.5 * mm});
            skCircle(sketch, "E36.8.3.0", {"center": v(-101.54, -20.16) * mm, "radius": 1.5 * mm});
            skCircle(sketch, "E36.8.4.0", {"center": v(-101.54, -23.5) * mm, "radius": 1.5 * mm});
            skLineSegment(sketch, "E36.direction1", {"start": v(-128.36, -10.1) * mm, "end": v(-125, -10.1) * mm, "construction": true});
            skLineSegment(sketch, "E36.direction2", {"start": v(-128.36, -10.1) * mm, "end": v(-128.36, -13.45) * mm, "construction": true});
            skSolve(sketch);
        }
        {
            var Q0;
            Q0=makeQuery(id+"F7.imprint","IMPRINT",FACE,{"disambiguationData":[TD([[makeQuery(id+"F7.imprint","IMPRINT",EDGE,{"derivedFrom":sQuery(id+"F7.wireOp",EDGE,"E36.6.4.0")}),1.0]])]});
            var Q1;
            Q1=makeQuery(id+"F7.imprint","IMPRINT",FACE,{"disambiguationData":[TD([[makeQuery(id+"F7.imprint","IMPRINT",EDGE,{"derivedFrom":sQuery(id+"F7.wireOp",EDGE,"E36.2.2.0")}),1.0]])]});
            var Q2;
            Q2=makeQuery(id+"F7.imprint","IMPRINT",FACE,{"disambiguationData":[TD([[makeQuery(id+"F7.imprint","IMPRINT",EDGE,{"derivedFrom":sQuery(id+"F7.wireOp",EDGE,"E35.8.0.0")}),1.0]])]});
            var Q3;
            Q3=makeQuery(id+"F7.imprint","IMPRINT",FACE,{"disambiguationData":[TD([[makeQuery(id+"F7.imprint","IMPRINT",EDGE,{"derivedFrom":sQuery(id+"F7.wireOp",EDGE,"E36.5.3.0")}),1.0]])]});
            var Q4;
            Q4=makeQuery(id+"F7.imprint","IMPRINT",FACE,{"disambiguationData":[TD([[makeQuery(id+"F7.imprint","IMPRINT",EDGE,{"derivedFrom":sQuery(id+"F7.wireOp",EDGE,"E36.8.2.0")}),1.0]])]});
            var Q5;
            Q5=makeQuery(id+"F7.imprint","IMPRINT",FACE,{"disambiguationData":[TD([[makeQuery(id+"F7.imprint","IMPRINT",EDGE,{"derivedFrom":sQuery(id+"F7.wireOp",EDGE,"E35.1.4.0")}),1.0]])]});
            var Q6;
            Q6=makeQuery(id+"F7.imprint","IMPRINT",FACE,{"disambiguationData":[TD([[makeQuery(id+"F7.imprint","IMPRINT",EDGE,{"derivedFrom":sQuery(id+"F7.wireOp",EDGE,"E35.5.0.0")}),1.0]])]});
            var Q7;
            Q7=makeQuery(id+"F7.imprint","IMPRINT",FACE,{"disambiguationData":[TD([[makeQuery(id+"F7.imprint","IMPRINT",EDGE,{"derivedFrom":sQuery(id+"F7.wireOp",EDGE,"E35.2.4.0")}),1.0]])]});
            var Q8;
            Q8=makeQuery(id+"F7.imprint","IMPRINT",FACE,{"disambiguationData":[TD([[makeQuery(id+"F7.imprint","IMPRINT",EDGE,{"derivedFrom":sQuery(id+"F7.wireOp",EDGE,"E35.6.0.0")}),1.0]])]});
            var Q9;
            Q9=makeQuery(id+"F7.imprint","IMPRINT",FACE,{"disambiguationData":[TD([[makeQuery(id+"F7.imprint","IMPRINT",EDGE,{"derivedFrom":sQuery(id+"F7.wireOp",EDGE,"E36.0.2.0")}),1.0]])]});
            var Q10;
            Q10=makeQuery(id+"F7.imprint","IMPRINT",FACE,{"disambiguationData":[TD([[makeQuery(id+"F7.imprint","IMPRINT",EDGE,{"derivedFrom":sQuery(id+"F7.wireOp",EDGE,"E36.3.3.0")}),1.0]])]});
            var Q11;
            Q11=makeQuery(id+"F7.imprint","IMPRINT",FACE,{"disambiguationData":[TD([[makeQuery(id+"F7.imprint","IMPRINT",EDGE,{"derivedFrom":sQuery(id+"F7.wireOp",EDGE,"E36.5.1.0")}),1.0]])]});
            var Q12;
            Q12=makeQuery(id+"F7.imprint","IMPRINT",FACE,{"disambiguationData":[TD([[makeQuery(id+"F7.imprint","IMPRINT",EDGE,{"derivedFrom":sQuery(id+"F7.wireOp",EDGE,"E36.7.1.0")}),1.0]])]});
            var Q13;
            Q13=makeQuery(id+"F7.imprint","IMPRINT",FACE,{"disambiguationData":[TD([[makeQuery(id+"F7.imprint","IMPRINT",EDGE,{"derivedFrom":sQuery(id+"F7.wireOp",EDGE,"E36.2.0.0")}),1.0]])]});
            var Q14;
            Q14=makeQuery(id+"F7.imprint","IMPRINT",FACE,{"disambiguationData":[TD([[makeQuery(id+"F7.imprint","IMPRINT",EDGE,{"derivedFrom":sQuery(id+"F7.wireOp",EDGE,"E17.0")}),-1.0]])]});
            var Q15;
            Q15=makeQuery(id+"F7.imprint","IMPRINT",FACE,{"disambiguationData":[TD([[makeQuery(id+"F7.imprint","IMPRINT",EDGE,{"derivedFrom":sQuery(id+"F7.wireOp",EDGE,"E36.5.4.0")}),1.0]])]});
            var Q16;
            Q16=makeQuery(id+"F7.imprint","IMPRINT",FACE,{"disambiguationData":[TD([[makeQuery(id+"F7.imprint","IMPRINT",EDGE,{"derivedFrom":sQuery(id+"F7.wireOp",EDGE,"E36.2.3.0")}),1.0]])]});
            var Q17;
            Q17=makeQuery(id+"F7.imprint","IMPRINT",FACE,{"disambiguationData":[TD([[makeQuery(id+"F7.imprint","IMPRINT",EDGE,{"derivedFrom":sQuery(id+"F7.wireOp",EDGE,"E35.8.1.0")}),1.0]])]});
            var Q18;
            Q18=makeQuery(id+"F7.imprint","IMPRINT",FACE,{"disambiguationData":[TD([[makeQuery(id+"F7.imprint","IMPRINT",EDGE,{"derivedFrom":sQuery(id+"F7.wireOp",EDGE,"E33")}),1.0]])]});
            var Q19;
            Q19=makeQuery(id+"F7.imprint","IMPRINT",FACE,{"disambiguationData":[TD([[makeQuery(id+"F7.imprint","IMPRINT",EDGE,{"derivedFrom":sQuery(id+"F7.wireOp",EDGE,"E35.7.3.0")}),1.0]])]});
            var Q20;
            Q20=makeQuery(id+"F7.imprint","IMPRINT",FACE,{"disambiguationData":[TD([[makeQuery(id+"F7.imprint","IMPRINT",EDGE,{"derivedFrom":sQuery(id+"F7.wireOp",EDGE,"E36.4.0.0")}),1.0]])]});
            var Q21;
            Q21=makeQuery(id+"F7.imprint","IMPRINT",FACE,{"disambiguationData":[TD([[makeQuery(id+"F7.imprint","IMPRINT",EDGE,{"derivedFrom":sQuery(id+"F7.wireOp",EDGE,"E36.0.4.0")}),1.0]])]});
            var Q22;
            Q22=makeQuery(id+"F7.imprint","IMPRINT",FACE,{"disambiguationData":[TD([[makeQuery(id+"F7.imprint","IMPRINT",EDGE,{"derivedFrom":sQuery(id+"F7.wireOp",EDGE,"E35.4.2.0")}),1.0]])]});
            var Q23;
            Q23=makeQuery(id+"F7.imprint","IMPRINT",FACE,{"disambiguationData":[TD([[makeQuery(id+"F7.imprint","IMPRINT",EDGE,{"derivedFrom":sQuery(id+"F7.wireOp",EDGE,"E35.6.2.0")}),1.0]])]});
            var Q24;
            Q24=makeQuery(id+"F7.imprint","IMPRINT",FACE,{"disambiguationData":[TD([[makeQuery(id+"F7.imprint","IMPRINT",EDGE,{"derivedFrom":sQuery(id+"F7.wireOp",EDGE,"E35.3.1.0")}),1.0]])]});
            var Q25;
            Q25=makeQuery(id+"F7.imprint","IMPRINT",FACE,{"disambiguationData":[TD([[makeQuery(id+"F7.imprint","IMPRINT",EDGE,{"derivedFrom":sQuery(id+"F7.wireOp",EDGE,"E34")}),1.0]])]});
            var Q26;
            Q26=makeQuery(id+"F7.imprint","IMPRINT",FACE,{"disambiguationData":[TD([[makeQuery(id+"F7.imprint","IMPRINT",EDGE,{"derivedFrom":sQuery(id+"F7.wireOp",EDGE,"E35.1.2.0")}),1.0]])]});
            var Q27;
            Q27=makeQuery(id+"F7.imprint","IMPRINT",FACE,{"disambiguationData":[TD([[makeQuery(id+"F7.imprint","IMPRINT",EDGE,{"derivedFrom":sQuery(id+"F7.wireOp",EDGE,"E35.4.3.0")}),1.0]])]});
            var Q28;
            Q28=makeQuery(id+"F7.imprint","IMPRINT",FACE,{"disambiguationData":[TD([[makeQuery(id+"F7.imprint","IMPRINT",EDGE,{"derivedFrom":sQuery(id+"F7.wireOp",EDGE,"E35.0.1.0")}),1.0]])]});
            var Q29;
            Q29=makeQuery(id+"F7.imprint","IMPRINT",FACE,{"disambiguationData":[TD([[makeQuery(id+"F7.imprint","IMPRINT",EDGE,{"derivedFrom":sQuery(id+"F7.wireOp",EDGE,"E36.8.3.0")}),1.0]])]});
            var Q30;
            Q30=makeQuery(id+"F7.imprint","IMPRINT",FACE,{"disambiguationData":[TD([[makeQuery(id+"F7.imprint","IMPRINT",EDGE,{"derivedFrom":sQuery(id+"F7.wireOp",EDGE,"E36.5.2.0")}),1.0]])]});
            var Q31;
            Q31=makeQuery(id+"F7.imprint","IMPRINT",FACE,{"disambiguationData":[TD([[makeQuery(id+"F7.imprint","IMPRINT",EDGE,{"derivedFrom":sQuery(id+"F7.wireOp",EDGE,"E36.2.1.0")}),1.0]])]});
            var Q32;
            Q32=makeQuery(id+"F7.imprint","IMPRINT",FACE,{"disambiguationData":[TD([[makeQuery(id+"F7.imprint","IMPRINT",EDGE,{"derivedFrom":sQuery(id+"F7.wireOp",EDGE,"E35.7.4.0")}),1.0]])]});
            var Q33;
            Q33=makeQuery(id+"F7.imprint","IMPRINT",FACE,{"disambiguationData":[TD([[makeQuery(id+"F7.imprint","IMPRINT",EDGE,{"derivedFrom":sQuery(id+"F7.wireOp",EDGE,"E35.0.2.0")}),1.0]])]});
            var Q34;
            Q34=makeQuery(id+"F7.imprint","IMPRINT",FACE,{"disambiguationData":[TD([[makeQuery(id+"F7.imprint","IMPRINT",EDGE,{"derivedFrom":sQuery(id+"F7.wireOp",EDGE,"E35.0.3.0")}),1.0]])]});
            var Q35;
            Q35=makeQuery(id+"F7.imprint","IMPRINT",FACE,{"disambiguationData":[TD([[makeQuery(id+"F7.imprint","IMPRINT",EDGE,{"derivedFrom":sQuery(id+"F7.wireOp",EDGE,"E35.5.1.0")}),1.0]])]});
            var Q36;
            Q36=makeQuery(id+"F7.imprint","IMPRINT",FACE,{"disambiguationData":[TD([[makeQuery(id+"F7.imprint","IMPRINT",EDGE,{"derivedFrom":sQuery(id+"F7.wireOp",EDGE,"E35.2.0.0")}),1.0]])]});
            var Q37;
            Q37=makeQuery(id+"F7.imprint","IMPRINT",FACE,{"disambiguationData":[TD([[makeQuery(id+"F7.imprint","IMPRINT",EDGE,{"derivedFrom":sQuery(id+"F7.wireOp",EDGE,"E21.0")}),1.0]])]});
            var Q38;
            Q38=makeQuery(id+"F7.imprint","IMPRINT",FACE,{"disambiguationData":[TD([[makeQuery(id+"F7.imprint","IMPRINT",EDGE,{"derivedFrom":sQuery(id+"F7.wireOp",EDGE,"E36.6.0.0")}),1.0]])]});
            var Q39;
            Q39=makeQuery(id+"F7.imprint","IMPRINT",FACE,{"disambiguationData":[TD([[makeQuery(id+"F7.imprint","IMPRINT",EDGE,{"derivedFrom":sQuery(id+"F7.wireOp",EDGE,"E36.2.4.0")}),1.0]])]});
            var Q40;
            Q40=makeQuery(id+"F7.imprint","IMPRINT",FACE,{"disambiguationData":[TD([[makeQuery(id+"F7.imprint","IMPRINT",EDGE,{"derivedFrom":sQuery(id+"F7.wireOp",EDGE,"E35.8.2.0")}),1.0]])]});
            var Q41;
            Q41=makeQuery(id+"F7.imprint","IMPRINT",FACE,{"disambiguationData":[TD([[makeQuery(id+"F7.imprint","IMPRINT",EDGE,{"derivedFrom":sQuery(id+"F7.wireOp",EDGE,"E36.3.4.0")}),1.0]])]});
            var Q42;
            Q42=makeQuery(id+"F7.imprint","IMPRINT",FACE,{"disambiguationData":[TD([[makeQuery(id+"F7.imprint","IMPRINT",EDGE,{"derivedFrom":sQuery(id+"F7.wireOp",EDGE,"E36.0.3.0")}),1.0]])]});
            var Q43;
            Q43=makeQuery(id+"F7.imprint","IMPRINT",FACE,{"disambiguationData":[TD([[makeQuery(id+"F7.imprint","IMPRINT",EDGE,{"derivedFrom":sQuery(id+"F7.wireOp",EDGE,"E35.6.1.0")}),1.0]])]});
            var Q44;
            Q44=makeQuery(id+"F7.imprint","IMPRINT",FACE,{"disambiguationData":[TD([[makeQuery(id+"F7.imprint","IMPRINT",EDGE,{"derivedFrom":sQuery(id+"F7.wireOp",EDGE,"E35.3.0.0")}),1.0]])]});
            var Q45;
            Q45=makeQuery(id+"F7.imprint","IMPRINT",FACE,{"disambiguationData":[TD([[makeQuery(id+"F7.imprint","IMPRINT",EDGE,{"derivedFrom":sQuery(id+"F7.wireOp",EDGE,"E36.7.0.0")}),1.0]])]});
            var Q46;
            Q46=makeQuery(id+"F7.imprint","IMPRINT",FACE,{"disambiguationData":[TD([[makeQuery(id+"F7.imprint","IMPRINT",EDGE,{"derivedFrom":sQuery(id+"F7.wireOp",EDGE,"E35.1.3.0")}),1.0]])]});
            var Q47;
            Q47=makeQuery(id+"F7.imprint","IMPRINT",FACE,{"disambiguationData":[TD([[makeQuery(id+"F7.imprint","IMPRINT",EDGE,{"derivedFrom":sQuery(id+"F7.wireOp",EDGE,"E35.4.4.0")}),1.0]])]});
            var Q48;
            Q48=makeQuery(id+"F7.imprint","IMPRINT",FACE,{"disambiguationData":[TD([[makeQuery(id+"F7.imprint","IMPRINT",EDGE,{"derivedFrom":sQuery(id+"F7.wireOp",EDGE,"E36.4.1.0")}),1.0]])]});
            var Q49;
            Q49=makeQuery(id+"F7.imprint","IMPRINT",FACE,{"disambiguationData":[TD([[makeQuery(id+"F7.imprint","IMPRINT",EDGE,{"derivedFrom":sQuery(id+"F7.wireOp",EDGE,"E36.1.0.0")}),1.0]])]});
            var Q50;
            Q50=makeQuery(id+"F7.imprint","IMPRINT",FACE,{"disambiguationData":[TD([[makeQuery(id+"F7.imprint","IMPRINT",EDGE,{"derivedFrom":sQuery(id+"F7.wireOp",EDGE,"E35.6.3.0")}),1.0]])]});
            var Q51;
            Q51=makeQuery(id+"F7.imprint","IMPRINT",FACE,{"disambiguationData":[TD([[makeQuery(id+"F7.imprint","IMPRINT",EDGE,{"derivedFrom":sQuery(id+"F7.wireOp",EDGE,"E35.3.2.0")}),1.0]])]});
            var Q52;
            Q52=makeQuery(id+"F7.imprint","IMPRINT",FACE,{"disambiguationData":[TD([[makeQuery(id+"F7.imprint","IMPRINT",EDGE,{"derivedFrom":sQuery(id+"F7.wireOp",EDGE,"E36.8.4.0")}),1.0]])]});
            var Q53;
            Q53=makeQuery(id+"F7.imprint","IMPRINT",FACE,{"disambiguationData":[TD([[makeQuery(id+"F7.imprint","IMPRINT",EDGE,{"derivedFrom":sQuery(id+"F7.wireOp",EDGE,"E36.7.2.0")}),1.0]])]});
            var Q54;
            Q54=makeQuery(id+"F7.imprint","IMPRINT",FACE,{"disambiguationData":[TD([[makeQuery(id+"F7.imprint","IMPRINT",EDGE,{"derivedFrom":sQuery(id+"F7.wireOp",EDGE,"E35.5.2.0")}),1.0]])]});
            var Q55;
            Q55=makeQuery(id+"F7.imprint","IMPRINT",FACE,{"disambiguationData":[TD([[makeQuery(id+"F7.imprint","IMPRINT",EDGE,{"derivedFrom":sQuery(id+"F7.wireOp",EDGE,"E35.4.0.0")}),1.0]])]});
            var Q56;
            Q56=makeQuery(id+"F7.imprint","IMPRINT",FACE,{"disambiguationData":[TD([[makeQuery(id+"F7.imprint","IMPRINT",EDGE,{"derivedFrom":sQuery(id+"F7.wireOp",EDGE,"E35.2.1.0")}),1.0]])]});
            var Q57;
            Q57=makeQuery(id+"F7.imprint","IMPRINT",FACE,{"disambiguationData":[TD([[makeQuery(id+"F7.imprint","IMPRINT",EDGE,{"derivedFrom":sQuery(id+"F7.wireOp",EDGE,"E36.8.0.0")}),1.0]])]});
            var Q58;
            Q58=makeQuery(id+"F7.imprint","IMPRINT",FACE,{"disambiguationData":[TD([[makeQuery(id+"F7.imprint","IMPRINT",EDGE,{"derivedFrom":sQuery(id+"F7.wireOp",EDGE,"E36.4.4.0")}),1.0]])]});
            var Q59;
            Q59=makeQuery(id+"F7.imprint","IMPRINT",FACE,{"disambiguationData":[TD([[makeQuery(id+"F7.imprint","IMPRINT",EDGE,{"derivedFrom":sQuery(id+"F7.wireOp",EDGE,"E36.6.1.0")}),1.0]])]});
            var Q60;
            Q60=makeQuery(id+"F7.imprint","IMPRINT",FACE,{"disambiguationData":[TD([[makeQuery(id+"F7.imprint","IMPRINT",EDGE,{"derivedFrom":sQuery(id+"F7.wireOp",EDGE,"E36.1.3.0")}),1.0]])]});
            var Q61;
            Q61=makeQuery(id+"F7.imprint","IMPRINT",FACE,{"disambiguationData":[TD([[makeQuery(id+"F7.imprint","IMPRINT",EDGE,{"derivedFrom":sQuery(id+"F7.wireOp",EDGE,"E36.3.0.0")}),1.0]])]});
            var Q62;
            Q62=makeQuery(id+"F7.imprint","IMPRINT",FACE,{"disambiguationData":[TD([[makeQuery(id+"F7.imprint","IMPRINT",EDGE,{"derivedFrom":sQuery(id+"F7.wireOp",EDGE,"E35.8.3.0")}),1.0]])]});
            var Q63;
            Q63=makeQuery(id+"F7.imprint","IMPRINT",FACE,{"disambiguationData":[TD([[makeQuery(id+"F7.imprint","IMPRINT",EDGE,{"derivedFrom":sQuery(id+"F7.wireOp",EDGE,"E35.7.1.0")}),1.0]])]});
            var Q64;
            Q64=makeQuery(id+"F7.imprint","IMPRINT",FACE,{"disambiguationData":[TD([[makeQuery(id+"F7.imprint","IMPRINT",EDGE,{"derivedFrom":sQuery(id+"F7.wireOp",EDGE,"E36.4.2.0")}),1.0]])]});
            var Q65;
            Q65=makeQuery(id+"F7.imprint","IMPRINT",FACE,{"disambiguationData":[TD([[makeQuery(id+"F7.imprint","IMPRINT",EDGE,{"derivedFrom":sQuery(id+"F7.wireOp",EDGE,"E36.1.1.0")}),1.0]])]});
            var Q66;
            Q66=makeQuery(id+"F7.imprint","IMPRINT",FACE,{"disambiguationData":[TD([[makeQuery(id+"F7.imprint","IMPRINT",EDGE,{"derivedFrom":sQuery(id+"F7.wireOp",EDGE,"E35.6.4.0")}),1.0]])]});
            var Q67;
            Q67=makeQuery(id+"F7.imprint","IMPRINT",FACE,{"disambiguationData":[TD([[makeQuery(id+"F7.imprint","IMPRINT",EDGE,{"derivedFrom":sQuery(id+"F7.wireOp",EDGE,"E35.3.3.0")}),1.0]])]});
            var Q68;
            Q68=makeQuery(id+"F7.imprint","IMPRINT",FACE,{"disambiguationData":[TD([[makeQuery(id+"F7.imprint","IMPRINT",EDGE,{"derivedFrom":sQuery(id+"F7.wireOp",EDGE,"E36.7.3.0")}),1.0]])]});
            var Q69;
            Q69=makeQuery(id+"F7.imprint","IMPRINT",FACE,{"disambiguationData":[TD([[makeQuery(id+"F7.imprint","IMPRINT",EDGE,{"derivedFrom":sQuery(id+"F7.wireOp",EDGE,"E35.5.3.0")}),1.0]])]});
            var Q70;
            Q70=makeQuery(id+"F7.imprint","IMPRINT",FACE,{"disambiguationData":[TD([[makeQuery(id+"F7.imprint","IMPRINT",EDGE,{"derivedFrom":sQuery(id+"F7.wireOp",EDGE,"E35.4.1.0")}),1.0]])]});
            var Q71;
            Q71=makeQuery(id+"F7.imprint","IMPRINT",FACE,{"disambiguationData":[TD([[makeQuery(id+"F7.imprint","IMPRINT",EDGE,{"derivedFrom":sQuery(id+"F7.wireOp",EDGE,"E35.2.2.0")}),1.0]])]});
            var Q72;
            Q72=makeQuery(id+"F7.imprint","IMPRINT",FACE,{"disambiguationData":[TD([[makeQuery(id+"F7.imprint","IMPRINT",EDGE,{"derivedFrom":sQuery(id+"F7.wireOp",EDGE,"E36.8.1.0")}),1.0]])]});
            var Q73;
            Q73=makeQuery(id+"F7.imprint","IMPRINT",FACE,{"disambiguationData":[TD([[makeQuery(id+"F7.imprint","IMPRINT",EDGE,{"derivedFrom":sQuery(id+"F7.wireOp",EDGE,"E36.6.2.0")}),1.0]])]});
            var Q74;
            Q74=makeQuery(id+"F7.imprint","IMPRINT",FACE,{"disambiguationData":[TD([[makeQuery(id+"F7.imprint","IMPRINT",EDGE,{"derivedFrom":sQuery(id+"F7.wireOp",EDGE,"E36.5.0.0")}),1.0]])]});
            var Q75;
            Q75=makeQuery(id+"F7.imprint","IMPRINT",FACE,{"disambiguationData":[TD([[makeQuery(id+"F7.imprint","IMPRINT",EDGE,{"derivedFrom":sQuery(id+"F7.wireOp",EDGE,"E36.1.4.0")}),1.0]])]});
            var Q76;
            Q76=makeQuery(id+"F7.imprint","IMPRINT",FACE,{"disambiguationData":[TD([[makeQuery(id+"F7.imprint","IMPRINT",EDGE,{"derivedFrom":sQuery(id+"F7.wireOp",EDGE,"E36.3.1.0")}),1.0]])]});
            var Q77;
            Q77=makeQuery(id+"F7.imprint","IMPRINT",FACE,{"disambiguationData":[TD([[makeQuery(id+"F7.imprint","IMPRINT",EDGE,{"derivedFrom":sQuery(id+"F7.wireOp",EDGE,"E35.7.2.0")}),1.0]])]});
            var Q78;
            Q78=makeQuery(id+"F7.imprint","IMPRINT",FACE,{"disambiguationData":[TD([[makeQuery(id+"F7.imprint","IMPRINT",EDGE,{"derivedFrom":sQuery(id+"F7.wireOp",EDGE,"E35.8.4.0")}),1.0]])]});
            var Q79;
            Q79=makeQuery(id+"F7.imprint","IMPRINT",FACE,{"disambiguationData":[TD([[makeQuery(id+"F7.imprint","IMPRINT",EDGE,{"derivedFrom":sQuery(id+"F7.wireOp",EDGE,"E36.4.3.0")}),1.0]])]});
            var Q80;
            Q80=makeQuery(id+"F7.imprint","IMPRINT",FACE,{"disambiguationData":[TD([[makeQuery(id+"F7.imprint","IMPRINT",EDGE,{"derivedFrom":sQuery(id+"F7.wireOp",EDGE,"E36.1.2.0")}),1.0]])]});
            var Q81;
            Q81=makeQuery(id+"F7.imprint","IMPRINT",FACE,{"disambiguationData":[TD([[makeQuery(id+"F7.imprint","IMPRINT",EDGE,{"derivedFrom":sQuery(id+"F7.wireOp",EDGE,"E35.7.0.0")}),1.0]])]});
            var Q82;
            Q82=makeQuery(id+"F7.imprint","IMPRINT",FACE,{"disambiguationData":[TD([[makeQuery(id+"F7.imprint","IMPRINT",EDGE,{"derivedFrom":sQuery(id+"F7.wireOp",EDGE,"E35.3.4.0")}),1.0]])]});
            var Q83;
            Q83=makeQuery(id+"F7.imprint","IMPRINT",FACE,{"disambiguationData":[TD([[makeQuery(id+"F7.imprint","IMPRINT",EDGE,{"derivedFrom":sQuery(id+"F7.wireOp",EDGE,"E36.7.4.0")}),1.0]])]});
            var Q84;
            Q84=makeQuery(id+"F7.imprint","IMPRINT",FACE,{"disambiguationData":[TD([[makeQuery(id+"F7.imprint","IMPRINT",EDGE,{"derivedFrom":sQuery(id+"F7.wireOp",EDGE,"E36.3.2.0")}),1.0]])]});
            var Q85;
            Q85=makeQuery(id+"F7.imprint","IMPRINT",FACE,{"disambiguationData":[TD([[makeQuery(id+"F7.imprint","IMPRINT",EDGE,{"derivedFrom":sQuery(id+"F7.wireOp",EDGE,"E36.0.1.0")}),1.0]])]});
            var Q86;
            Q86=makeQuery(id+"F7.imprint","IMPRINT",FACE,{"disambiguationData":[TD([[makeQuery(id+"F7.imprint","IMPRINT",EDGE,{"derivedFrom":sQuery(id+"F7.wireOp",EDGE,"E35.5.4.0")}),1.0]])]});
            var Q87;
            Q87=makeQuery(id+"F7.imprint","IMPRINT",FACE,{"disambiguationData":[TD([[makeQuery(id+"F7.imprint","IMPRINT",EDGE,{"derivedFrom":sQuery(id+"F7.wireOp",EDGE,"E35.2.3.0")}),1.0]])]});
            var Q88;
            Q88=makeQuery(id+"F7.imprint","IMPRINT",FACE,{"disambiguationData":[TD([[makeQuery(id+"F7.imprint","IMPRINT",EDGE,{"derivedFrom":sQuery(id+"F7.wireOp",EDGE,"E36.6.3.0")}),1.0]])]});
            var Q89;
            Q89=makeQuery(id+"F7.imprint","IMPRINT",FACE,{"disambiguationData":[TD([[makeQuery(id+"F7.imprint","IMPRINT",EDGE,{"derivedFrom":sQuery(id+"F7.wireOp",EDGE,"E35.1.1.0")}),1.0]])]});
            var Q90;
            Q90=makeQuery(id+"F7.imprint","IMPRINT",FACE,{"disambiguationData":[TD([[makeQuery(id+"F7.imprint","IMPRINT",EDGE,{"derivedFrom":sQuery(id+"F7.wireOp",EDGE,"E35.0.4.0")}),1.0]])]});
            var Q91;
            Q91=makeQuery(id+"F7.imprint","IMPRINT",FACE,{"disambiguationData":[TD([[makeQuery(id+"F7.imprint","IMPRINT",EDGE,{"derivedFrom":sQuery(id+"F7.wireOp",EDGE,"E35.1.0.0")}),1.0]])]});
            extrude(context, id + "F8", {"entities" : qUnion([Q0, Q1, Q2, Q3, Q4, Q5, Q6, Q7, Q8, Q9, Q10, Q11, Q12, Q13, Q14, Q15, Q16, Q17, Q18, Q19, Q20, Q21, Q22, Q23, Q24, Q25, Q26, Q27, Q28, Q29, Q30, Q31, Q32, Q33, Q34, Q35, Q36, Q37, Q38, Q39, Q40, Q41, Q42, Q43, Q44, Q45, Q46, Q47, Q48, Q49, Q50, Q51, Q52, Q53, Q54, Q55, Q56, Q57, Q58, Q59, Q60, Q61, Q62, Q63, Q64, Q65, Q66, Q67, Q68, Q69, Q70, Q71, Q72, Q73, Q74, Q75, Q76, Q77, Q78, Q79, Q80, Q81, Q82, Q83, Q84, Q85, Q86, Q87, Q88, Q89, Q90, Q91]), "oppositeDirection" : true, "depth" : 1.6 * mm});
        }
        {
            var Q0;
            Q0=makeQuery(id+"F7.imprint","IMPRINT",FACE,{"disambiguationData":[TD([[makeQuery(id+"F7.imprint","IMPRINT",EDGE,{"derivedFrom":sQuery(id+"F7.wireOp",EDGE,"E35.2.1.0")}),1.0]])]});
            var Q1;
            Q1=makeQuery(id+"F7.imprint","IMPRINT",FACE,{"disambiguationData":[TD([[makeQuery(id+"F7.imprint","IMPRINT",EDGE,{"derivedFrom":sQuery(id+"F7.wireOp",EDGE,"E35.8.2.0")}),1.0]])]});
            var Q2;
            Q2=makeQuery(id+"F7.imprint","IMPRINT",FACE,{"disambiguationData":[TD([[makeQuery(id+"F7.imprint","IMPRINT",EDGE,{"derivedFrom":sQuery(id+"F7.wireOp",EDGE,"E35.2.0.0")}),1.0]])]});
            var Q3;
            Q3=makeQuery(id+"F7.imprint","IMPRINT",FACE,{"disambiguationData":[TD([[makeQuery(id+"F7.imprint","IMPRINT",EDGE,{"derivedFrom":sQuery(id+"F7.wireOp",EDGE,"E35.5.1.0")}),1.0]])]});
            var Q4;
            Q4=makeQuery(id+"F7.imprint","IMPRINT",FACE,{"disambiguationData":[TD([[makeQuery(id+"F7.imprint","IMPRINT",EDGE,{"derivedFrom":sQuery(id+"F7.wireOp",EDGE,"E35.8.0.0")}),1.0]])]});
            var Q5;
            Q5=makeQuery(id+"F7.imprint","IMPRINT",FACE,{"disambiguationData":[TD([[makeQuery(id+"F7.imprint","IMPRINT",EDGE,{"derivedFrom":sQuery(id+"F7.wireOp",EDGE,"E35.1.3.0")}),1.0]])]});
            var Q6;
            Q6=makeQuery(id+"F7.imprint","IMPRINT",FACE,{"disambiguationData":[TD([[makeQuery(id+"F7.imprint","IMPRINT",EDGE,{"derivedFrom":sQuery(id+"F7.wireOp",EDGE,"E35.4.4.0")}),1.0]])]});
            var Q7;
            Q7=makeQuery(id+"F7.imprint","IMPRINT",FACE,{"disambiguationData":[TD([[makeQuery(id+"F7.imprint","IMPRINT",EDGE,{"derivedFrom":sQuery(id+"F7.wireOp",EDGE,"E35.7.4.0")}),1.0]])]});
            var Q8;
            Q8=makeQuery(id+"F7.imprint","IMPRINT",FACE,{"disambiguationData":[TD([[makeQuery(id+"F7.imprint","IMPRINT",EDGE,{"derivedFrom":sQuery(id+"F7.wireOp",EDGE,"E35.1.2.0")}),1.0]])]});
            var Q9;
            Q9=makeQuery(id+"F7.imprint","IMPRINT",FACE,{"disambiguationData":[TD([[makeQuery(id+"F7.imprint","IMPRINT",EDGE,{"derivedFrom":sQuery(id+"F7.wireOp",EDGE,"E35.4.3.0")}),1.0]])]});
            var Q10;
            Q10=makeQuery(id+"F7.imprint","IMPRINT",FACE,{"disambiguationData":[TD([[makeQuery(id+"F7.imprint","IMPRINT",EDGE,{"derivedFrom":sQuery(id+"F7.wireOp",EDGE,"E35.3.4.0")}),1.0]])]});
            var Q11;
            Q11=makeQuery(id+"F7.imprint","IMPRINT",FACE,{"disambiguationData":[TD([[makeQuery(id+"F7.imprint","IMPRINT",EDGE,{"derivedFrom":sQuery(id+"F7.wireOp",EDGE,"E35.7.0.0")}),1.0]])]});
            var Q12;
            Q12=makeQuery(id+"F7.imprint","IMPRINT",FACE,{"disambiguationData":[TD([[makeQuery(id+"F7.imprint","IMPRINT",EDGE,{"derivedFrom":sQuery(id+"F7.wireOp",EDGE,"E35.6.4.0")}),1.0]])]});
            var Q13;
            Q13=makeQuery(id+"F7.imprint","IMPRINT",FACE,{"disambiguationData":[TD([[makeQuery(id+"F7.imprint","IMPRINT",EDGE,{"derivedFrom":sQuery(id+"F7.wireOp",EDGE,"E35.4.0.0")}),1.0]])]});
            var Q14;
            Q14=makeQuery(id+"F7.imprint","IMPRINT",FACE,{"disambiguationData":[TD([[makeQuery(id+"F7.imprint","IMPRINT",EDGE,{"derivedFrom":sQuery(id+"F7.wireOp",EDGE,"E35.3.1.0")}),1.0]])]});
            var Q15;
            Q15=makeQuery(id+"F7.imprint","IMPRINT",FACE,{"disambiguationData":[TD([[makeQuery(id+"F7.imprint","IMPRINT",EDGE,{"derivedFrom":sQuery(id+"F7.wireOp",EDGE,"E35.6.2.0")}),1.0]])]});
            var Q16;
            Q16=makeQuery(id+"F7.imprint","IMPRINT",FACE,{"disambiguationData":[TD([[makeQuery(id+"F7.imprint","IMPRINT",EDGE,{"derivedFrom":sQuery(id+"F7.wireOp",EDGE,"E35.4.2.0")}),1.0]])]});
            var Q17;
            Q17=makeQuery(id+"F7.imprint","IMPRINT",FACE,{"disambiguationData":[TD([[makeQuery(id+"F7.imprint","IMPRINT",EDGE,{"derivedFrom":sQuery(id+"F7.wireOp",EDGE,"E35.3.0.0")}),1.0]])]});
            var Q18;
            Q18=makeQuery(id+"F7.imprint","IMPRINT",FACE,{"disambiguationData":[TD([[makeQuery(id+"F7.imprint","IMPRINT",EDGE,{"derivedFrom":sQuery(id+"F7.wireOp",EDGE,"E35.6.1.0")}),1.0]])]});
            var Q19;
            Q19=makeQuery(id+"F7.imprint","IMPRINT",FACE,{"disambiguationData":[TD([[makeQuery(id+"F7.imprint","IMPRINT",EDGE,{"derivedFrom":sQuery(id+"F7.wireOp",EDGE,"E35.0.3.0")}),1.0]])]});
            var Q20;
            Q20=makeQuery(id+"F7.imprint","IMPRINT",FACE,{"disambiguationData":[TD([[makeQuery(id+"F7.imprint","IMPRINT",EDGE,{"derivedFrom":sQuery(id+"F7.wireOp",EDGE,"E35.0.2.0")}),1.0]])]});
            var Q21;
            Q21=makeQuery(id+"F7.imprint","IMPRINT",FACE,{"disambiguationData":[TD([[makeQuery(id+"F7.imprint","IMPRINT",EDGE,{"derivedFrom":sQuery(id+"F7.wireOp",EDGE,"E35.0.1.0")}),1.0]])]});
            var Q22;
            Q22=makeQuery(id+"F7.imprint","IMPRINT",FACE,{"disambiguationData":[TD([[makeQuery(id+"F7.imprint","IMPRINT",EDGE,{"derivedFrom":sQuery(id+"F7.wireOp",EDGE,"E34")}),1.0]])]});
            var Q23;
            Q23=makeQuery(id+"F7.imprint","IMPRINT",FACE,{"disambiguationData":[TD([[makeQuery(id+"F7.imprint","IMPRINT",EDGE,{"derivedFrom":sQuery(id+"F7.wireOp",EDGE,"E35.2.4.0")}),1.0]])]});
            var Q24;
            Q24=makeQuery(id+"F7.imprint","IMPRINT",FACE,{"disambiguationData":[TD([[makeQuery(id+"F7.imprint","IMPRINT",EDGE,{"derivedFrom":sQuery(id+"F7.wireOp",EDGE,"E35.6.0.0")}),1.0]])]});
            var Q25;
            Q25=makeQuery(id+"F7.imprint","IMPRINT",FACE,{"disambiguationData":[TD([[makeQuery(id+"F7.imprint","IMPRINT",EDGE,{"derivedFrom":sQuery(id+"F7.wireOp",EDGE,"E35.5.4.0")}),1.0]])]});
            var Q26;
            Q26=makeQuery(id+"F7.imprint","IMPRINT",FACE,{"disambiguationData":[TD([[makeQuery(id+"F7.imprint","IMPRINT",EDGE,{"derivedFrom":sQuery(id+"F7.wireOp",EDGE,"E35.2.3.0")}),1.0]])]});
            var Q27;
            Q27=makeQuery(id+"F7.imprint","IMPRINT",FACE,{"disambiguationData":[TD([[makeQuery(id+"F7.imprint","IMPRINT",EDGE,{"derivedFrom":sQuery(id+"F7.wireOp",EDGE,"E35.7.2.0")}),1.0]])]});
            var Q28;
            Q28=makeQuery(id+"F7.imprint","IMPRINT",FACE,{"disambiguationData":[TD([[makeQuery(id+"F7.imprint","IMPRINT",EDGE,{"derivedFrom":sQuery(id+"F7.wireOp",EDGE,"E35.8.4.0")}),1.0]])]});
            var Q29;
            Q29=makeQuery(id+"F7.imprint","IMPRINT",FACE,{"disambiguationData":[TD([[makeQuery(id+"F7.imprint","IMPRINT",EDGE,{"derivedFrom":sQuery(id+"F7.wireOp",EDGE,"E35.4.1.0")}),1.0]])]});
            var Q30;
            Q30=makeQuery(id+"F7.imprint","IMPRINT",FACE,{"disambiguationData":[TD([[makeQuery(id+"F7.imprint","IMPRINT",EDGE,{"derivedFrom":sQuery(id+"F7.wireOp",EDGE,"E35.2.2.0")}),1.0]])]});
            var Q31;
            Q31=makeQuery(id+"F7.imprint","IMPRINT",FACE,{"disambiguationData":[TD([[makeQuery(id+"F7.imprint","IMPRINT",EDGE,{"derivedFrom":sQuery(id+"F7.wireOp",EDGE,"E35.5.3.0")}),1.0]])]});
            var Q32;
            Q32=makeQuery(id+"F7.imprint","IMPRINT",FACE,{"disambiguationData":[TD([[makeQuery(id+"F7.imprint","IMPRINT",EDGE,{"derivedFrom":sQuery(id+"F7.wireOp",EDGE,"E35.3.3.0")}),1.0]])]});
            var Q33;
            Q33=makeQuery(id+"F7.imprint","IMPRINT",FACE,{"disambiguationData":[TD([[makeQuery(id+"F7.imprint","IMPRINT",EDGE,{"derivedFrom":sQuery(id+"F7.wireOp",EDGE,"E35.7.1.0")}),1.0]])]});
            var Q34;
            Q34=makeQuery(id+"F7.imprint","IMPRINT",FACE,{"disambiguationData":[TD([[makeQuery(id+"F7.imprint","IMPRINT",EDGE,{"derivedFrom":sQuery(id+"F7.wireOp",EDGE,"E35.8.3.0")}),1.0]])]});
            var Q35;
            Q35=makeQuery(id+"F7.imprint","IMPRINT",FACE,{"disambiguationData":[TD([[makeQuery(id+"F7.imprint","IMPRINT",EDGE,{"derivedFrom":sQuery(id+"F7.wireOp",EDGE,"E35.5.2.0")}),1.0]])]});
            var Q36;
            Q36=makeQuery(id+"F7.imprint","IMPRINT",FACE,{"disambiguationData":[TD([[makeQuery(id+"F7.imprint","IMPRINT",EDGE,{"derivedFrom":sQuery(id+"F7.wireOp",EDGE,"E35.6.3.0")}),1.0]])]});
            var Q37;
            Q37=makeQuery(id+"F7.imprint","IMPRINT",FACE,{"disambiguationData":[TD([[makeQuery(id+"F7.imprint","IMPRINT",EDGE,{"derivedFrom":sQuery(id+"F7.wireOp",EDGE,"E35.3.2.0")}),1.0]])]});
            var Q38;
            Q38=makeQuery(id+"F7.imprint","IMPRINT",FACE,{"disambiguationData":[TD([[makeQuery(id+"F7.imprint","IMPRINT",EDGE,{"derivedFrom":sQuery(id+"F7.wireOp",EDGE,"E35.7.3.0")}),1.0]])]});
            var Q39;
            Q39=makeQuery(id+"F7.imprint","IMPRINT",FACE,{"disambiguationData":[TD([[makeQuery(id+"F7.imprint","IMPRINT",EDGE,{"derivedFrom":sQuery(id+"F7.wireOp",EDGE,"E35.8.1.0")}),1.0]])]});
            var Q40;
            Q40=makeQuery(id+"F7.imprint","IMPRINT",FACE,{"disambiguationData":[TD([[makeQuery(id+"F7.imprint","IMPRINT",EDGE,{"derivedFrom":sQuery(id+"F7.wireOp",EDGE,"E35.1.4.0")}),1.0]])]});
            var Q41;
            Q41=makeQuery(id+"F7.imprint","IMPRINT",FACE,{"disambiguationData":[TD([[makeQuery(id+"F7.imprint","IMPRINT",EDGE,{"derivedFrom":sQuery(id+"F7.wireOp",EDGE,"E35.5.0.0")}),1.0]])]});
            var Q42;
            Q42=makeQuery(id+"F7.imprint","IMPRINT",FACE,{"disambiguationData":[TD([[makeQuery(id+"F7.imprint","IMPRINT",EDGE,{"derivedFrom":sQuery(id+"F7.wireOp",EDGE,"E35.1.1.0")}),1.0]])]});
            var Q43;
            Q43=makeQuery(id+"F7.imprint","IMPRINT",FACE,{"disambiguationData":[TD([[makeQuery(id+"F7.imprint","IMPRINT",EDGE,{"derivedFrom":sQuery(id+"F7.wireOp",EDGE,"E35.0.4.0")}),1.0]])]});
            var Q44;
            Q44=makeQuery(id+"F7.imprint","IMPRINT",FACE,{"disambiguationData":[TD([[makeQuery(id+"F7.imprint","IMPRINT",EDGE,{"derivedFrom":sQuery(id+"F7.wireOp",EDGE,"E35.1.0.0")}),1.0]])]});
            extrude(context, id + "F9", {"entities" : qUnion([Q0, Q1, Q2, Q3, Q4, Q5, Q6, Q7, Q8, Q9, Q10, Q11, Q12, Q13, Q14, Q15, Q16, Q17, Q18, Q19, Q20, Q21, Q22, Q23, Q24, Q25, Q26, Q27, Q28, Q29, Q30, Q31, Q32, Q33, Q34, Q35, Q36, Q37, Q38, Q39, Q40, Q41, Q42, Q43, Q44]), "operationType" : NewBodyOperationType.ADD, "depth" : 10 * mm});
        }
        {
            var Q0;
            Q0=makeQuery(id+"F7.imprint","IMPRINT",FACE,{"disambiguationData":[TD([[makeQuery(id+"F7.imprint","IMPRINT",EDGE,{"derivedFrom":sQuery(id+"F7.wireOp",EDGE,"E36.3.0.0")}),1.0]])]});
            var Q1;
            Q1=makeQuery(id+"F7.imprint","IMPRINT",FACE,{"disambiguationData":[TD([[makeQuery(id+"F7.imprint","IMPRINT",EDGE,{"derivedFrom":sQuery(id+"F7.wireOp",EDGE,"E36.6.1.0")}),1.0]])]});
            var Q2;
            Q2=makeQuery(id+"F7.imprint","IMPRINT",FACE,{"disambiguationData":[TD([[makeQuery(id+"F7.imprint","IMPRINT",EDGE,{"derivedFrom":sQuery(id+"F7.wireOp",EDGE,"E36.2.4.0")}),1.0]])]});
            var Q3;
            Q3=makeQuery(id+"F7.imprint","IMPRINT",FACE,{"disambiguationData":[TD([[makeQuery(id+"F7.imprint","IMPRINT",EDGE,{"derivedFrom":sQuery(id+"F7.wireOp",EDGE,"E36.6.0.0")}),1.0]])]});
            var Q4;
            Q4=makeQuery(id+"F7.imprint","IMPRINT",FACE,{"disambiguationData":[TD([[makeQuery(id+"F7.imprint","IMPRINT",EDGE,{"derivedFrom":sQuery(id+"F7.wireOp",EDGE,"E36.2.2.0")}),1.0]])]});
            var Q5;
            Q5=makeQuery(id+"F7.imprint","IMPRINT",FACE,{"disambiguationData":[TD([[makeQuery(id+"F7.imprint","IMPRINT",EDGE,{"derivedFrom":sQuery(id+"F7.wireOp",EDGE,"E36.5.3.0")}),1.0]])]});
            var Q6;
            Q6=makeQuery(id+"F7.imprint","IMPRINT",FACE,{"disambiguationData":[TD([[makeQuery(id+"F7.imprint","IMPRINT",EDGE,{"derivedFrom":sQuery(id+"F7.wireOp",EDGE,"E36.8.4.0")}),1.0]])]});
            var Q7;
            Q7=makeQuery(id+"F7.imprint","IMPRINT",FACE,{"disambiguationData":[TD([[makeQuery(id+"F7.imprint","IMPRINT",EDGE,{"derivedFrom":sQuery(id+"F7.wireOp",EDGE,"E36.2.1.0")}),1.0]])]});
            var Q8;
            Q8=makeQuery(id+"F7.imprint","IMPRINT",FACE,{"disambiguationData":[TD([[makeQuery(id+"F7.imprint","IMPRINT",EDGE,{"derivedFrom":sQuery(id+"F7.wireOp",EDGE,"E36.5.2.0")}),1.0]])]});
            var Q9;
            Q9=makeQuery(id+"F7.imprint","IMPRINT",FACE,{"disambiguationData":[TD([[makeQuery(id+"F7.imprint","IMPRINT",EDGE,{"derivedFrom":sQuery(id+"F7.wireOp",EDGE,"E36.8.3.0")}),1.0]])]});
            var Q10;
            Q10=makeQuery(id+"F7.imprint","IMPRINT",FACE,{"disambiguationData":[TD([[makeQuery(id+"F7.imprint","IMPRINT",EDGE,{"derivedFrom":sQuery(id+"F7.wireOp",EDGE,"E36.1.2.0")}),1.0]])]});
            var Q11;
            Q11=makeQuery(id+"F7.imprint","IMPRINT",FACE,{"disambiguationData":[TD([[makeQuery(id+"F7.imprint","IMPRINT",EDGE,{"derivedFrom":sQuery(id+"F7.wireOp",EDGE,"E36.4.3.0")}),1.0]])]});
            var Q12;
            Q12=makeQuery(id+"F7.imprint","IMPRINT",FACE,{"disambiguationData":[TD([[makeQuery(id+"F7.imprint","IMPRINT",EDGE,{"derivedFrom":sQuery(id+"F7.wireOp",EDGE,"E36.1.1.0")}),1.0]])]});
            var Q13;
            Q13=makeQuery(id+"F7.imprint","IMPRINT",FACE,{"disambiguationData":[TD([[makeQuery(id+"F7.imprint","IMPRINT",EDGE,{"derivedFrom":sQuery(id+"F7.wireOp",EDGE,"E36.4.2.0")}),1.0]])]});
            var Q14;
            Q14=makeQuery(id+"F7.imprint","IMPRINT",FACE,{"disambiguationData":[TD([[makeQuery(id+"F7.imprint","IMPRINT",EDGE,{"derivedFrom":sQuery(id+"F7.wireOp",EDGE,"E36.8.0.0")}),1.0]])]});
            var Q15;
            Q15=makeQuery(id+"F7.imprint","IMPRINT",FACE,{"disambiguationData":[TD([[makeQuery(id+"F7.imprint","IMPRINT",EDGE,{"derivedFrom":sQuery(id+"F7.wireOp",EDGE,"E36.4.1.0")}),1.0]])]});
            var Q16;
            Q16=makeQuery(id+"F7.imprint","IMPRINT",FACE,{"disambiguationData":[TD([[makeQuery(id+"F7.imprint","IMPRINT",EDGE,{"derivedFrom":sQuery(id+"F7.wireOp",EDGE,"E36.0.4.0")}),1.0]])]});
            var Q17;
            Q17=makeQuery(id+"F7.imprint","IMPRINT",FACE,{"disambiguationData":[TD([[makeQuery(id+"F7.imprint","IMPRINT",EDGE,{"derivedFrom":sQuery(id+"F7.wireOp",EDGE,"E36.7.1.0")}),1.0]])]});
            var Q18;
            Q18=makeQuery(id+"F7.imprint","IMPRINT",FACE,{"disambiguationData":[TD([[makeQuery(id+"F7.imprint","IMPRINT",EDGE,{"derivedFrom":sQuery(id+"F7.wireOp",EDGE,"E36.2.0.0")}),1.0]])]});
            var Q19;
            Q19=makeQuery(id+"F7.imprint","IMPRINT",FACE,{"disambiguationData":[TD([[makeQuery(id+"F7.imprint","IMPRINT",EDGE,{"derivedFrom":sQuery(id+"F7.wireOp",EDGE,"E36.5.1.0")}),1.0]])]});
            var Q20;
            Q20=makeQuery(id+"F7.imprint","IMPRINT",FACE,{"disambiguationData":[TD([[makeQuery(id+"F7.imprint","IMPRINT",EDGE,{"derivedFrom":sQuery(id+"F7.wireOp",EDGE,"E36.8.2.0")}),1.0]])]});
            var Q21;
            Q21=makeQuery(id+"F7.imprint","IMPRINT",FACE,{"disambiguationData":[TD([[makeQuery(id+"F7.imprint","IMPRINT",EDGE,{"derivedFrom":sQuery(id+"F7.wireOp",EDGE,"E36.7.0.0")}),1.0]])]});
            var Q22;
            Q22=makeQuery(id+"F7.imprint","IMPRINT",FACE,{"disambiguationData":[TD([[makeQuery(id+"F7.imprint","IMPRINT",EDGE,{"derivedFrom":sQuery(id+"F7.wireOp",EDGE,"E36.0.3.0")}),1.0]])]});
            var Q23;
            Q23=makeQuery(id+"F7.imprint","IMPRINT",FACE,{"disambiguationData":[TD([[makeQuery(id+"F7.imprint","IMPRINT",EDGE,{"derivedFrom":sQuery(id+"F7.wireOp",EDGE,"E36.3.4.0")}),1.0]])]});
            var Q24;
            Q24=makeQuery(id+"F7.imprint","IMPRINT",FACE,{"disambiguationData":[TD([[makeQuery(id+"F7.imprint","IMPRINT",EDGE,{"derivedFrom":sQuery(id+"F7.wireOp",EDGE,"E33")}),1.0]])]});
            var Q25;
            Q25=makeQuery(id+"F7.imprint","IMPRINT",FACE,{"disambiguationData":[TD([[makeQuery(id+"F7.imprint","IMPRINT",EDGE,{"derivedFrom":sQuery(id+"F7.wireOp",EDGE,"E36.6.4.0")}),1.0]])]});
            var Q26;
            Q26=makeQuery(id+"F7.imprint","IMPRINT",FACE,{"disambiguationData":[TD([[makeQuery(id+"F7.imprint","IMPRINT",EDGE,{"derivedFrom":sQuery(id+"F7.wireOp",EDGE,"E36.3.2.0")}),1.0]])]});
            var Q27;
            Q27=makeQuery(id+"F7.imprint","IMPRINT",FACE,{"disambiguationData":[TD([[makeQuery(id+"F7.imprint","IMPRINT",EDGE,{"derivedFrom":sQuery(id+"F7.wireOp",EDGE,"E36.0.1.0")}),1.0]])]});
            var Q28;
            Q28=makeQuery(id+"F7.imprint","IMPRINT",FACE,{"disambiguationData":[TD([[makeQuery(id+"F7.imprint","IMPRINT",EDGE,{"derivedFrom":sQuery(id+"F7.wireOp",EDGE,"E36.6.3.0")}),1.0]])]});
            var Q29;
            Q29=makeQuery(id+"F7.imprint","IMPRINT",FACE,{"disambiguationData":[TD([[makeQuery(id+"F7.imprint","IMPRINT",EDGE,{"derivedFrom":sQuery(id+"F7.wireOp",EDGE,"E36.7.4.0")}),1.0]])]});
            var Q30;
            Q30=makeQuery(id+"F7.imprint","IMPRINT",FACE,{"disambiguationData":[TD([[makeQuery(id+"F7.imprint","IMPRINT",EDGE,{"derivedFrom":sQuery(id+"F7.wireOp",EDGE,"E36.1.4.0")}),1.0]])]});
            var Q31;
            Q31=makeQuery(id+"F7.imprint","IMPRINT",FACE,{"disambiguationData":[TD([[makeQuery(id+"F7.imprint","IMPRINT",EDGE,{"derivedFrom":sQuery(id+"F7.wireOp",EDGE,"E36.5.0.0")}),1.0]])]});
            var Q32;
            Q32=makeQuery(id+"F7.imprint","IMPRINT",FACE,{"disambiguationData":[TD([[makeQuery(id+"F7.imprint","IMPRINT",EDGE,{"derivedFrom":sQuery(id+"F7.wireOp",EDGE,"E36.3.1.0")}),1.0]])]});
            var Q33;
            Q33=makeQuery(id+"F7.imprint","IMPRINT",FACE,{"disambiguationData":[TD([[makeQuery(id+"F7.imprint","IMPRINT",EDGE,{"derivedFrom":sQuery(id+"F7.wireOp",EDGE,"E36.6.2.0")}),1.0]])]});
            var Q34;
            Q34=makeQuery(id+"F7.imprint","IMPRINT",FACE,{"disambiguationData":[TD([[makeQuery(id+"F7.imprint","IMPRINT",EDGE,{"derivedFrom":sQuery(id+"F7.wireOp",EDGE,"E36.8.1.0")}),1.0]])]});
            var Q35;
            Q35=makeQuery(id+"F7.imprint","IMPRINT",FACE,{"disambiguationData":[TD([[makeQuery(id+"F7.imprint","IMPRINT",EDGE,{"derivedFrom":sQuery(id+"F7.wireOp",EDGE,"E36.7.3.0")}),1.0]])]});
            var Q36;
            Q36=makeQuery(id+"F7.imprint","IMPRINT",FACE,{"disambiguationData":[TD([[makeQuery(id+"F7.imprint","IMPRINT",EDGE,{"derivedFrom":sQuery(id+"F7.wireOp",EDGE,"E36.1.3.0")}),1.0]])]});
            var Q37;
            Q37=makeQuery(id+"F7.imprint","IMPRINT",FACE,{"disambiguationData":[TD([[makeQuery(id+"F7.imprint","IMPRINT",EDGE,{"derivedFrom":sQuery(id+"F7.wireOp",EDGE,"E36.4.4.0")}),1.0]])]});
            var Q38;
            Q38=makeQuery(id+"F7.imprint","IMPRINT",FACE,{"disambiguationData":[TD([[makeQuery(id+"F7.imprint","IMPRINT",EDGE,{"derivedFrom":sQuery(id+"F7.wireOp",EDGE,"E36.7.2.0")}),1.0]])]});
            var Q39;
            Q39=makeQuery(id+"F7.imprint","IMPRINT",FACE,{"disambiguationData":[TD([[makeQuery(id+"F7.imprint","IMPRINT",EDGE,{"derivedFrom":sQuery(id+"F7.wireOp",EDGE,"E36.1.0.0")}),1.0]])]});
            var Q40;
            Q40=makeQuery(id+"F7.imprint","IMPRINT",FACE,{"disambiguationData":[TD([[makeQuery(id+"F7.imprint","IMPRINT",EDGE,{"derivedFrom":sQuery(id+"F7.wireOp",EDGE,"E36.4.0.0")}),1.0]])]});
            var Q41;
            Q41=makeQuery(id+"F7.imprint","IMPRINT",FACE,{"disambiguationData":[TD([[makeQuery(id+"F7.imprint","IMPRINT",EDGE,{"derivedFrom":sQuery(id+"F7.wireOp",EDGE,"E36.2.3.0")}),1.0]])]});
            var Q42;
            Q42=makeQuery(id+"F7.imprint","IMPRINT",FACE,{"disambiguationData":[TD([[makeQuery(id+"F7.imprint","IMPRINT",EDGE,{"derivedFrom":sQuery(id+"F7.wireOp",EDGE,"E36.5.4.0")}),1.0]])]});
            var Q43;
            Q43=makeQuery(id+"F7.imprint","IMPRINT",FACE,{"disambiguationData":[TD([[makeQuery(id+"F7.imprint","IMPRINT",EDGE,{"derivedFrom":sQuery(id+"F7.wireOp",EDGE,"E36.0.2.0")}),1.0]])]});
            var Q44;
            Q44=makeQuery(id+"F7.imprint","IMPRINT",FACE,{"disambiguationData":[TD([[makeQuery(id+"F7.imprint","IMPRINT",EDGE,{"derivedFrom":sQuery(id+"F7.wireOp",EDGE,"E36.3.3.0")}),1.0]])]});
            extrude(context, id + "F10", {"entities" : qUnion([Q0, Q1, Q2, Q3, Q4, Q5, Q6, Q7, Q8, Q9, Q10, Q11, Q12, Q13, Q14, Q15, Q16, Q17, Q18, Q19, Q20, Q21, Q22, Q23, Q24, Q25, Q26, Q27, Q28, Q29, Q30, Q31, Q32, Q33, Q34, Q35, Q36, Q37, Q38, Q39, Q40, Q41, Q42, Q43, Q44]), "operationType" : NewBodyOperationType.ADD, "depth" : 10 * mm});
        }
        {
            var Q0;
            Q0=qCreatedBy(makeId("Top.planeOp"),FACE);
            cPlane(context, id + "F11", {"entities" : qUnion([Q0]), "cplaneType" : CPlaneType.OFFSET, "offset" : 20 * mm, "oppositeDirection" : true, "width" : 150 * mm, "height" : 150 * mm});
        }
        {
            var Q0;
            Q0=qCreatedBy(id+"F11.planeOp",FACE);
            var sketch = newSketch(context, id + "F12", { "sketchPlane" : qUnion([Q0])});
            skCircle(sketch, "E37.0", {"center": v(-57.86, -1.79) * mm, "radius": 23.81 * mm});
            skCircle(sketch, "E38.0", {"center": v(141.25, -1.79) * mm, "radius": 23.81 * mm});
            skSolve(sketch);
        }
        {
            var Q0;
            Q0=makeQuery(id+"F12.imprint","IMPRINT",FACE,{"disambiguationData":[TD([[makeQuery(id+"F12.imprint","IMPRINT",EDGE,{"derivedFrom":sQuery(id+"F12.wireOp",EDGE,"E37.0")}),1.0]])]});
            var Q1;
            Q1=makeQuery(id+"F12.imprint","IMPRINT",FACE,{"disambiguationData":[TD([[makeQuery(id+"F12.imprint","IMPRINT",EDGE,{"derivedFrom":sQuery(id+"F12.wireOp",EDGE,"E38.0")}),1.0]])]});
            extrude(context, id + "F13", {"entities" : qUnion([Q0, Q1]), "oppositeDirection" : true, "depth" : 1.6 * mm});
        }
        {
            var Q0;
            Q0=makeQuery(id+"F8.opExtrude","CAP_FACE",FACE,{"disambiguationData":[OSD([sQuery(id+"F7.wireOp",EDGE,"E21.0"),sQuery(id+"F7.wireOp",EDGE,"E22.0"),sQuery(id+"F7.wireOp",EDGE,"E23.0"),sQuery(id+"F7.wireOp",EDGE,"E24.0"),sQuery(id+"F7.wireOp",EDGE,"E29"),sQuery(id+"F7.wireOp",EDGE,"E30"),sQuery(id+"F7.wireOp",EDGE,"E31"),sQuery(id+"F7.wireOp",EDGE,"E32")])],"isStart":true});
            var sketch = newSketch(context, id + "F14", { "sketchPlane" : qUnion([Q0])});
            skCircle(sketch, "E39.0", {"center": v(-128.36, 19.22) * mm, "radius": 1.5 * mm});
            skCircle(sketch, "E40.0", {"center": v(-133.96, 23.03) * mm, "radius": 1.75 * mm});
            skCircle(sketch, "E41.0", {"center": v(-95.86, 23.03) * mm, "radius": 1.75 * mm});
            skCircle(sketch, "E42.0", {"center": v(-133.96, 2.71) * mm, "radius": 1.75 * mm});
            skCircle(sketch, "E43.0", {"center": v(-95.86, 2.71) * mm, "radius": 1.75 * mm});
            skCircle(sketch, "E44.0", {"center": v(-133.96, -6.29) * mm, "radius": 1.75 * mm});
            skCircle(sketch, "E45.0", {"center": v(-101.54, 5.81) * mm, "radius": 1.5 * mm});
            skCircle(sketch, "E46.0", {"center": v(-95.86, -6.29) * mm, "radius": 1.75 * mm});
            skCircle(sketch, "E47.0.0", {"center": v(-128.36, -10.1) * mm, "radius": 1.5 * mm});
            skCircle(sketch, "E48.0.0", {"center": v(-101.54, -23.5) * mm, "radius": 1.5 * mm});
            skCircle(sketch, "E49.0", {"center": v(-95.86, -26.6) * mm, "radius": 1.75 * mm});
            skCircle(sketch, "E50.0", {"center": v(-133.96, -26.6) * mm, "radius": 1.75 * mm});
            skLineSegment(sketch, "E51.bottom", {"start": v(-136.96, 26.03) * mm, "end": v(-92.86, 26.03) * mm});
            skLineSegment(sketch, "E51.top", {"start": v(-136.96, -0.29) * mm, "end": v(-92.86, -0.29) * mm});
            skLineSegment(sketch, "E51.left", {"start": v(-136.96, 26.03) * mm, "end": v(-136.96, -0.29) * mm});
            skLineSegment(sketch, "E51.right", {"start": v(-92.86, 26.03) * mm, "end": v(-92.86, -0.29) * mm});
            skLineSegment(sketch, "E52.bottom", {"start": v(-136.96, -3.29) * mm, "end": v(-92.86, -3.29) * mm});
            skLineSegment(sketch, "E52.top", {"start": v(-136.96, -29.6) * mm, "end": v(-92.86, -29.6) * mm});
            skLineSegment(sketch, "E52.left", {"start": v(-136.96, -3.29) * mm, "end": v(-136.96, -29.6) * mm});
            skLineSegment(sketch, "E52.right", {"start": v(-92.86, -3.29) * mm, "end": v(-92.86, -29.6) * mm});
            skLineSegment(sketch, "E53.bottom", {"start": v(-130.86, 21.72) * mm, "end": v(-99.04, 21.72) * mm});
            skLineSegment(sketch, "E53.top", {"start": v(-130.86, 3.31) * mm, "end": v(-99.04, 3.31) * mm});
            skLineSegment(sketch, "E53.left", {"start": v(-130.86, 21.72) * mm, "end": v(-130.86, 3.31) * mm});
            skLineSegment(sketch, "E53.right", {"start": v(-99.04, 21.72) * mm, "end": v(-99.04, 3.31) * mm});
            skLineSegment(sketch, "E54.bottom", {"start": v(-130.86, -7.6) * mm, "end": v(-99.04, -7.6) * mm});
            skLineSegment(sketch, "E54.top", {"start": v(-130.86, -26) * mm, "end": v(-99.04, -26) * mm});
            skLineSegment(sketch, "E54.left", {"start": v(-130.86, -7.6) * mm, "end": v(-130.86, -26) * mm});
            skLineSegment(sketch, "E54.right", {"start": v(-99.04, -7.6) * mm, "end": v(-99.04, -26) * mm});
            skSolve(sketch);
        }
        {
            var Q0;
            Q0=makeQuery(id+"F14.imprint","IMPRINT",FACE,{"disambiguationData":[TD([[makeQuery(id+"F14.imprint","IMPRINT",EDGE,{"derivedFrom":sQuery(id+"F14.wireOp",EDGE,"E40.0")}),-1.0]])]});
            var Q1;
            Q1=makeQuery(id+"F14.imprint","IMPRINT",FACE,{"disambiguationData":[TD([[makeQuery(id+"F14.imprint","IMPRINT",EDGE,{"derivedFrom":sQuery(id+"F14.wireOp",EDGE,"E44.0")}),-1.0]])]});
            var Q2;
            Q2=qCreatedBy(makeId("Top.planeOp"),FACE);
            extrude(context, id + "F15", {"entities" : qUnion([Q0, Q1]), "endBound" : BoundingType.UP_TO_SURFACE, "endBoundEntityFace" : qUnion([Q2]), "depth" : 25 * mm});
        }
        {
            var Q0;
            Q0=makeQuery(id+"F13.opExtrude","CAP_FACE",FACE,{"disambiguationData":[OSD([sQuery(id+"F12.wireOp",EDGE,"E37.0")])],"isStart":false});
            var sketch = newSketch(context, id + "F16", { "sketchPlane" : qUnion([Q0])});
            skCircle(sketch, "E55.0", {"center": v(-57.86, 1.79) * mm, "radius": 23.81 * mm, "construction": true});
            skCircle(sketch, "E56.0", {"center": v(141.25, 1.79) * mm, "radius": 23.81 * mm, "construction": true});
            skCircle(sketch, "E57", {"center": v(-57.86, 1.79) * mm, "radius": 22.81 * mm});
            skCircle(sketch, "E58", {"center": v(-57.86, 1.79) * mm, "radius": 24.81 * mm});
            skCircle(sketch, "E59", {"center": v(141.25, 1.79) * mm, "radius": 22.81 * mm});
            skCircle(sketch, "E60", {"center": v(141.25, 1.79) * mm, "radius": 24.81 * mm});
            skLineSegment(sketch, "E61", {"start": v(-57.86, -26.02) * mm, "end": v(-57.86, 29.6) * mm, "construction": true});
            skCircle(sketch, "E62", {"center": v(-57.86, 29.6) * mm, "radius": 1.75 * mm});
            skArc(sketch, "E63", {"start": v(-56.1, 29.55) * mm, "mid": v(-57.86, 29.6) * mm, "end": v(-59.6, 29.55) * mm, "construction": true});
            skArc(sketch, "E64", {"start": v(-59.6, 29.55) * mm, "mid": v(-60.6, 29.47) * mm, "end": v(-61.6, 29.35) * mm, "construction": true});
            skArc(sketch, "E65", {"start": v(-61.6, 29.35) * mm, "mid": v(-85.67, 1.79) * mm, "end": v(-61.6, -25.77) * mm});
            skArc(sketch, "E66", {"start": v(-54.11, 29.35) * mm, "mid": v(-55.1, 29.47) * mm, "end": v(-56.1, 29.55) * mm, "construction": true});
            skArc(sketch, "E67", {"start": v(-61.6, 29.35) * mm, "mid": v(-57.86, 25.85) * mm, "end": v(-54.11, 29.35) * mm, "construction": true});
            skArc(sketch, "E68", {"start": v(-54.11, 29.35) * mm, "mid": v(-57.86, 33.35) * mm, "end": v(-61.6, 29.35) * mm});
            skCircle(sketch, "E69", {"center": v(-57.86, -26.02) * mm, "radius": 1.75 * mm});
            skArc(sketch, "E70", {"start": v(-61.6, -25.77) * mm, "mid": v(-60.6, -25.89) * mm, "end": v(-59.6, -25.97) * mm, "construction": true});
            skArc(sketch, "E71", {"start": v(-54.11, -25.77) * mm, "mid": v(-30.04, 1.79) * mm, "end": v(-54.11, 29.35) * mm});
            skArc(sketch, "E72", {"start": v(-56.1, -25.97) * mm, "mid": v(-55.1, -25.89) * mm, "end": v(-54.11, -25.77) * mm, "construction": true});
            skArc(sketch, "E73", {"start": v(-59.6, -25.97) * mm, "mid": v(-57.86, -26.02) * mm, "end": v(-56.1, -25.97) * mm, "construction": true});
            skArc(sketch, "E74", {"start": v(-61.6, -25.77) * mm, "mid": v(-57.86, -29.77) * mm, "end": v(-54.11, -25.77) * mm});
            skArc(sketch, "E75", {"start": v(-54.11, -25.77) * mm, "mid": v(-57.86, -22.27) * mm, "end": v(-61.6, -25.77) * mm, "construction": true});
            skLineSegment(sketch, "E76", {"start": v(141.25, -26.02) * mm, "end": v(141.25, 29.6) * mm, "construction": true});
            skCircle(sketch, "E77", {"center": v(141.25, 29.6) * mm, "radius": 1.75 * mm});
            skCircle(sketch, "E78", {"center": v(141.25, -26.02) * mm, "radius": 1.75 * mm});
            skArc(sketch, "E79", {"start": v(137.5, 29.35) * mm, "mid": v(141.25, 25.85) * mm, "end": v(144.99, 29.35) * mm, "construction": true});
            skArc(sketch, "E80", {"start": v(144.99, 29.35) * mm, "mid": v(141.25, 33.35) * mm, "end": v(137.5, 29.35) * mm});
            skArc(sketch, "E81", {"start": v(137.5, 29.35) * mm, "mid": v(113.43, 1.79) * mm, "end": v(137.5, -25.77) * mm});
            skArc(sketch, "E82", {"start": v(144.99, 29.35) * mm, "mid": v(141.25, 29.6) * mm, "end": v(137.5, 29.35) * mm, "construction": true});
            skArc(sketch, "E83", {"start": v(137.5, -25.77) * mm, "mid": v(141.25, -26.02) * mm, "end": v(144.99, -25.77) * mm, "construction": true});
            skArc(sketch, "E84", {"start": v(144.99, -25.77) * mm, "mid": v(169.06, 1.79) * mm, "end": v(144.99, 29.35) * mm});
            skArc(sketch, "E85", {"start": v(144.99, -25.77) * mm, "mid": v(141.25, -22.27) * mm, "end": v(137.5, -25.77) * mm, "construction": true});
            skArc(sketch, "E86", {"start": v(137.5, -25.77) * mm, "mid": v(141.25, -29.77) * mm, "end": v(144.99, -25.77) * mm});
            skSolve(sketch);
        }
        {
            var Q0;
            Q0=makeQuery(id+"F16.imprint","IMPRINT",FACE,{"disambiguationData":[TD([[makeQuery(id+"F16.imprint","IMPRINT",EDGE,{"derivedFrom":sQuery(id+"F16.wireOp",EDGE,"E58")}),1.0]])]});
            var Q1;
            Q1=makeQuery(id+"F16.imprint","IMPRINT",FACE,{"disambiguationData":[TD([[makeQuery(id+"F16.imprint","IMPRINT",EDGE,{"derivedFrom":sQuery(id+"F16.wireOp",EDGE,"E57")}),-1.0]])]});
            var Q2;
            Q2=makeQuery(id+"F16.imprint","IMPRINT",FACE,{"disambiguationData":[TD([[makeQuery(id+"F16.imprint","IMPRINT",EDGE,{"derivedFrom":sQuery(id+"F16.wireOp",EDGE,"E58")}),-1.0]])]});
            var Q3;
            Q3=makeQuery(id+"F16.imprint","IMPRINT",FACE,{"disambiguationData":[TD([[makeQuery(id+"F16.imprint","IMPRINT",EDGE,{"derivedFrom":sQuery(id+"F16.wireOp",EDGE,"E60")}),-1.0]])]});
            var Q4;
            Q4=makeQuery(id+"F16.imprint","IMPRINT",FACE,{"disambiguationData":[TD([[makeQuery(id+"F16.imprint","IMPRINT",EDGE,{"derivedFrom":sQuery(id+"F16.wireOp",EDGE,"E59")}),-1.0]])]});
            extrude(context, id + "F17", {"entities" : qUnion([Q0, Q1, Q2, Q3, Q4]), "depth" : 2 * mm});
        }
        {
            var Q0;
            Q0=makeQuery(id+"F16.imprint","IMPRINT",FACE,{"disambiguationData":[TD([[makeQuery(id+"F16.imprint","IMPRINT",EDGE,{"derivedFrom":sQuery(id+"F16.wireOp",EDGE,"E58")}),-1.0]])]});
            var Q1;
            Q1=qCreatedBy(makeId("Top.planeOp"),FACE);
            extrude(context, id + "F18", {"entities" : qUnion([Q0]), "operationType" : NewBodyOperationType.ADD, "endBound" : BoundingType.UP_TO_SURFACE, "oppositeDirection" : true, "endBoundEntityFace" : qUnion([Q1]), "depth" : 25 * mm});
        }
        {
            var Q0;
            Q0=makeQuery(id+"F16.imprint","IMPRINT",FACE,{"disambiguationData":[TD([[makeQuery(id+"F16.imprint","IMPRINT",EDGE,{"derivedFrom":sQuery(id+"F16.wireOp",EDGE,"E60")}),-1.0]])]});
            var Q1;
            Q1=qCreatedBy(makeId("Top.planeOp"),FACE);
            extrude(context, id + "F19", {"entities" : qUnion([Q0]), "operationType" : NewBodyOperationType.ADD, "endBound" : BoundingType.UP_TO_SURFACE, "oppositeDirection" : true, "endBoundEntityFace" : qUnion([Q1]), "depth" : 25 * mm});
        }
        {
            var Q0;
            Q0=makeQuery(id+"F15.opExtrude","CAP_FACE",FACE,{"disambiguationData":[OSD([sQuery(id+"F14.wireOp",EDGE,"E44.0"),sQuery(id+"F14.wireOp",EDGE,"E46.0"),sQuery(id+"F14.wireOp",EDGE,"E49.0"),sQuery(id+"F14.wireOp",EDGE,"E50.0"),sQuery(id+"F14.wireOp",EDGE,"E52.bottom"),sQuery(id+"F14.wireOp",EDGE,"E52.top"),sQuery(id+"F14.wireOp",EDGE,"E52.left"),sQuery(id+"F14.wireOp",EDGE,"E52.right"),sQuery(id+"F14.wireOp",EDGE,"E54.bottom"),sQuery(id+"F14.wireOp",EDGE,"E54.top"),sQuery(id+"F14.wireOp",EDGE,"E54.left"),sQuery(id+"F14.wireOp",EDGE,"E54.right")])],"isStart":true});
            var sketch = newSketch(context, id + "F20", { "sketchPlane" : qUnion([Q0])});
            skLineSegment(sketch, "E87.0", {"start": v(-136.96, -26.03) * mm, "end": v(-130.86, -26.03) * mm, "construction": true});
            skLineSegment(sketch, "E88.0", {"start": v(-92.86, -26.03) * mm, "end": v(-92.86, -20.28) * mm, "construction": true});
            skLineSegment(sketch, "E89.0", {"start": v(-136.96, 0.29) * mm, "end": v(-130.86, 0.29) * mm, "construction": true});
            skLineSegment(sketch, "E90.0", {"start": v(-92.86, 3.29) * mm, "end": v(-92.86, 9.04) * mm, "construction": true});
            skLineSegment(sketch, "E91.0", {"start": v(-136.96, 3.29) * mm, "end": v(-130.86, 3.29) * mm, "construction": true});
            skLineSegment(sketch, "E91.1", {"start": v(-130.86, 7.6) * mm, "end": v(-99.04, 7.6) * mm, "construction": true});
            skLineSegment(sketch, "E91.2", {"start": v(-99.04, 7.6) * mm, "end": v(-99.04, 26) * mm, "construction": true});
            skLineSegment(sketch, "E91.3", {"start": v(-130.86, 26) * mm, "end": v(-99.04, 26) * mm, "construction": true});
            skLineSegment(sketch, "E91.4", {"start": v(-130.86, 7.6) * mm, "end": v(-130.86, 26) * mm, "construction": true});
            skLineSegment(sketch, "E91.5", {"start": v(-136.96, 3.29) * mm, "end": v(-136.96, 9.04) * mm, "construction": true});
            skLineSegment(sketch, "E91.6", {"start": v(-136.96, 29.6) * mm, "end": v(-99.04, 29.6) * mm});
            skLineSegment(sketch, "E92.0", {"start": v(-99.04, -21.72) * mm, "end": v(-99.04, -3.31) * mm, "construction": true});
            skLineSegment(sketch, "E92.1", {"start": v(-130.86, -21.72) * mm, "end": v(-99.04, -21.72) * mm});
            skLineSegment(sketch, "E92.2", {"start": v(-130.86, -3.31) * mm, "end": v(-99.04, -3.31) * mm});
            skLineSegment(sketch, "E92.3", {"start": v(-130.86, -21.72) * mm, "end": v(-130.86, -3.31) * mm, "construction": true});
            skLineSegment(sketch, "E93", {"start": v(-99.04, 3.29) * mm, "end": v(-99.04, 9.04) * mm});
            skLineSegment(sketch, "E94", {"start": v(-130.86, 3.29) * mm, "end": v(-130.86, 9.04) * mm});
            skLineSegment(sketch, "E95", {"start": v(-92.86, 23.86) * mm, "end": v(-99.04, 23.86) * mm});
            skLineSegment(sketch, "E96", {"start": v(-92.86, 9.04) * mm, "end": v(-99.04, 9.04) * mm});
            skLineSegment(sketch, "E97", {"start": v(-92.86, 9.04) * mm, "end": v(-92.86, 23.86) * mm});
            skLineSegment(sketch, "E98", {"start": v(-92.86, 23.86) * mm, "end": v(-92.86, 29.6) * mm, "construction": true});
            skLineSegment(sketch, "E99", {"start": v(-136.96, 23.86) * mm, "end": v(-136.96, 29.6) * mm, "construction": true});
            skLineSegment(sketch, "E100", {"start": v(-136.96, 9.04) * mm, "end": v(-136.96, 23.86) * mm});
            skLineSegment(sketch, "E101", {"start": v(-99.04, 3.29) * mm, "end": v(-92.86, 3.29) * mm, "construction": true});
            skLineSegment(sketch, "E102", {"start": v(-130.86, 3.29) * mm, "end": v(-99.04, 3.29) * mm});
            skLineSegment(sketch, "E103", {"start": v(-130.86, 29.6) * mm, "end": v(-130.86, 29.6) * mm});
            skLineSegment(sketch, "E104", {"start": v(-99.04, 29.6) * mm, "end": v(-92.86, 29.6) * mm, "construction": true});
            skLineSegment(sketch, "E105", {"start": v(-99.04, 9.04) * mm, "end": v(-99.04, 29.6) * mm});
            skLineSegment(sketch, "E106", {"start": v(-130.86, 9.04) * mm, "end": v(-130.86, 29.6) * mm});
            skLineSegment(sketch, "E107", {"start": v(-130.86, 23.86) * mm, "end": v(-136.96, 23.86) * mm});
            skLineSegment(sketch, "E108", {"start": v(-99.04, 23.86) * mm, "end": v(-130.86, 23.86) * mm, "construction": true});
            skLineSegment(sketch, "E109", {"start": v(-130.86, 9.04) * mm, "end": v(-136.96, 9.04) * mm});
            skLineSegment(sketch, "E110", {"start": v(-99.04, 9.04) * mm, "end": v(-130.86, 9.04) * mm, "construction": true});
            skLineSegment(sketch, "E111", {"start": v(-92.86, -5.46) * mm, "end": v(-99.04, -5.46) * mm});
            skLineSegment(sketch, "E112", {"start": v(-92.86, -20.28) * mm, "end": v(-99.04, -20.28) * mm});
            skLineSegment(sketch, "E113", {"start": v(-99.04, -26.03) * mm, "end": v(-99.04, 0.29) * mm});
            skLineSegment(sketch, "E114", {"start": v(-130.86, -26.03) * mm, "end": v(-130.86, 0.29) * mm});
            skLineSegment(sketch, "E115", {"start": v(-99.04, -26.03) * mm, "end": v(-92.86, -26.03) * mm, "construction": true});
            skLineSegment(sketch, "E116", {"start": v(-130.86, -26.03) * mm, "end": v(-99.04, -26.03) * mm});
            skLineSegment(sketch, "E117", {"start": v(-130.86, 0.29) * mm, "end": v(-130.86, 0.29) * mm});
            skLineSegment(sketch, "E118", {"start": v(-130.86, 0.29) * mm, "end": v(-99.04, 0.29) * mm});
            skLineSegment(sketch, "E119", {"start": v(-99.04, 0.29) * mm, "end": v(-92.86, 0.29) * mm, "construction": true});
            skLineSegment(sketch, "E120", {"start": v(-99.04, -20.28) * mm, "end": v(-130.86, -20.28) * mm, "construction": true});
            skLineSegment(sketch, "E121", {"start": v(-99.04, -5.46) * mm, "end": v(-130.86, -5.46) * mm, "construction": true});
            skLineSegment(sketch, "E122", {"start": v(-130.86, -5.46) * mm, "end": v(-136.96, -5.46) * mm});
            skLineSegment(sketch, "E123", {"start": v(-130.86, -20.28) * mm, "end": v(-136.96, -20.28) * mm});
            skLineSegment(sketch, "E124", {"start": v(-92.86, -20.28) * mm, "end": v(-92.86, -5.46) * mm});
            skLineSegment(sketch, "E125", {"start": v(-92.86, -5.46) * mm, "end": v(-92.86, 0.29) * mm, "construction": true});
            skLineSegment(sketch, "E126.0", {"start": v(-136.96, -26.03) * mm, "end": v(-136.96, -20.28) * mm});
            skLineSegment(sketch, "E127", {"start": v(-136.96, -20.28) * mm, "end": v(-136.96, -5.46) * mm});
            skLineSegment(sketch, "E128", {"start": v(-136.96, -5.46) * mm, "end": v(-136.96, 0.29) * mm});
            skSolve(sketch);
        }
        {
            var Q0;
            {var subQ0=sQuery(id+"F20.wireOp",EDGE,"E111");Q0=makeQuery(id+"F20.imprint","IMPRINT",FACE,{"disambiguationData":[TD([[makeQuery(id+"F20.imprint","IMPRINT",EDGE,{"derivedFrom":subQ0}),1.0]])]});}
            var Q1;
            {var subQ0=sQuery(id+"F20.wireOp",EDGE,"E92.2");Q1=makeQuery(id+"F20.imprint","IMPRINT",FACE,{"disambiguationData":[TD([[makeQuery(id+"F20.imprint","IMPRINT",EDGE,{"derivedFrom":subQ0}),1.0]])]});}
            var Q2;
            {var subQ0=sQuery(id+"F20.wireOp",EDGE,"E92.1");Q2=makeQuery(id+"F20.imprint","IMPRINT",FACE,{"disambiguationData":[TD([[makeQuery(id+"F20.imprint","IMPRINT",EDGE,{"derivedFrom":subQ0}),-1.0]])]});}
            var Q3;
            {var subQ0=sQuery(id+"F20.wireOp",EDGE,"E122");Q3=makeQuery(id+"F20.imprint","IMPRINT",FACE,{"disambiguationData":[TD([[makeQuery(id+"F20.imprint","IMPRINT",EDGE,{"derivedFrom":subQ0}),1.0]])]});}
            extrude(context, id + "F21", {"entities" : qUnion([Q0, Q1, Q2, Q3]), "operationType" : NewBodyOperationType.REMOVE, "oppositeDirection" : true, "depth" : 2 * mm});
        }
        {
            var Q0;
            {var subQ0=sQuery(id+"F20.wireOp",EDGE,"E95");Q0=makeQuery(id+"F20.imprint","IMPRINT",FACE,{"disambiguationData":[TD([[makeQuery(id+"F20.imprint","IMPRINT",EDGE,{"derivedFrom":subQ0}),1.0]])]});}
            var Q1;
            {var subQ5=makeQuery(id+"F15.opExtrude","CAP_EDGE",EDGE,{"disambiguationData":[OSD([sQuery(id+"F14.wireOp",EDGE,"E54.top")])],"isStart":true});Q1=makeQuery(id+"F20.imprint","IMPRINT",FACE,{"disambiguationData":[TD([[makeQuery(id+"F20.imprint","IMPRINT",EDGE,{"derivedFrom":subQ5}),1.0]])]});}
            var Q2;
            Q2=makeQuery(id+"F20.imprint","IMPRINT",FACE,{"disambiguationData":[TD([[makeQuery(id+"F20.imprint","IMPRINT",EDGE,{"derivedFrom":sQuery(id+"F20.wireOp",EDGE,"E100")}),-1.0]])]});
            var Q3;
            {var subQ2=sQuery(id+"F20.wireOp",EDGE,"E102");Q3=makeQuery(id+"F20.imprint","IMPRINT",FACE,{"disambiguationData":[TD([[makeQuery(id+"F20.imprint","IMPRINT",EDGE,{"derivedFrom":subQ2}),1.0]])]});}
            extrude(context, id + "F22", {"entities" : qUnion([Q0, Q1, Q2, Q3]), "operationType" : NewBodyOperationType.REMOVE, "oppositeDirection" : true, "depth" : 2 * mm});
        }
        {
            var Q0;
            {var subQ0=sQuery(id+"F2.wireOp",EDGE,"E14");var subQ1=sQuery(id+"F2.wireOp",EDGE,"E13");var subQ2=sQuery(id+"F2.wireOp",EDGE,"E12");var subQ3=sQuery(id+"F2.wireOp",EDGE,"E11");var subQ4=sQuery(id+"F2.wireOp",EDGE,"E10");var subQ5=sQuery(id+"F2.wireOp",EDGE,"E9");var subQ6=sQuery(id+"F2.wireOp",EDGE,"E8.3");var subQ7=sQuery(id+"F2.wireOp",EDGE,"E8.2");var subQ8=sQuery(id+"F2.wireOp",EDGE,"E8.1");var subQ9=sQuery(id+"F2.wireOp",EDGE,"E8.0");Q0=makeQuery(id+"F4.boolean.opBoolean","MERGE",FACE,{"derivedFrom":[makeQuery(id+"F3.opExtrude","CAP_FACE",FACE,{"disambiguationData":[OSD([subQ9,subQ8,subQ7,subQ6,subQ5,subQ4,subQ3,subQ2,subQ1,subQ0,sQuery(id+"F2.wireOp",EDGE,"E15"),sQuery(id+"F2.wireOp",EDGE,"E16.0.1.0"),sQuery(id+"F2.wireOp",EDGE,"E16.0.2.0"),sQuery(id+"F2.wireOp",EDGE,"E16.0.3.0"),sQuery(id+"F2.wireOp",EDGE,"E16.0.4.0"),sQuery(id+"F2.wireOp",EDGE,"E16.1.0.0"),sQuery(id+"F2.wireOp",EDGE,"E16.1.1.0"),sQuery(id+"F2.wireOp",EDGE,"E16.1.2.0"),sQuery(id+"F2.wireOp",EDGE,"E16.1.3.0"),sQuery(id+"F2.wireOp",EDGE,"E16.1.4.0"),sQuery(id+"F2.wireOp",EDGE,"E16.2.0.0"),sQuery(id+"F2.wireOp",EDGE,"E16.2.1.0"),sQuery(id+"F2.wireOp",EDGE,"E16.2.2.0"),sQuery(id+"F2.wireOp",EDGE,"E16.2.3.0"),sQuery(id+"F2.wireOp",EDGE,"E16.2.4.0"),sQuery(id+"F2.wireOp",EDGE,"E16.3.0.0"),sQuery(id+"F2.wireOp",EDGE,"E16.3.1.0"),sQuery(id+"F2.wireOp",EDGE,"E16.3.2.0"),sQuery(id+"F2.wireOp",EDGE,"E16.3.3.0"),sQuery(id+"F2.wireOp",EDGE,"E16.3.4.0"),sQuery(id+"F2.wireOp",EDGE,"E16.4.0.0"),sQuery(id+"F2.wireOp",EDGE,"E16.4.1.0"),sQuery(id+"F2.wireOp",EDGE,"E16.4.2.0"),sQuery(id+"F2.wireOp",EDGE,"E16.4.3.0"),sQuery(id+"F2.wireOp",EDGE,"E16.4.4.0"),sQuery(id+"F2.wireOp",EDGE,"E16.5.0.0"),sQuery(id+"F2.wireOp",EDGE,"E16.5.1.0"),sQuery(id+"F2.wireOp",EDGE,"E16.5.2.0"),sQuery(id+"F2.wireOp",EDGE,"E16.5.3.0"),sQuery(id+"F2.wireOp",EDGE,"E16.5.4.0"),sQuery(id+"F2.wireOp",EDGE,"E16.6.0.0"),sQuery(id+"F2.wireOp",EDGE,"E16.6.1.0"),sQuery(id+"F2.wireOp",EDGE,"E16.6.2.0"),sQuery(id+"F2.wireOp",EDGE,"E16.6.3.0"),sQuery(id+"F2.wireOp",EDGE,"E16.6.4.0"),sQuery(id+"F2.wireOp",EDGE,"E16.7.0.0"),sQuery(id+"F2.wireOp",EDGE,"E16.7.1.0"),sQuery(id+"F2.wireOp",EDGE,"E16.7.2.0"),sQuery(id+"F2.wireOp",EDGE,"E16.7.3.0"),sQuery(id+"F2.wireOp",EDGE,"E16.7.4.0"),sQuery(id+"F2.wireOp",EDGE,"E16.8.0.0"),sQuery(id+"F2.wireOp",EDGE,"E16.8.1.0"),sQuery(id+"F2.wireOp",EDGE,"E16.8.2.0"),sQuery(id+"F2.wireOp",EDGE,"E16.8.3.0"),sQuery(id+"F2.wireOp",EDGE,"E16.8.4.0"),sQuery(id+"F2.wireOp",EDGE,"E16.9.0.0"),sQuery(id+"F2.wireOp",EDGE,"E16.9.1.0"),sQuery(id+"F2.wireOp",EDGE,"E16.9.2.0"),sQuery(id+"F2.wireOp",EDGE,"E16.9.3.0"),sQuery(id+"F2.wireOp",EDGE,"E16.9.4.0"),sQuery(id+"F2.wireOp",EDGE,"E16.10.0.0"),sQuery(id+"F2.wireOp",EDGE,"E16.10.1.0"),sQuery(id+"F2.wireOp",EDGE,"E16.10.2.0"),sQuery(id+"F2.wireOp",EDGE,"E16.10.3.0"),sQuery(id+"F2.wireOp",EDGE,"E16.10.4.0"),sQuery(id+"F2.wireOp",EDGE,"E16.11.0.0"),sQuery(id+"F2.wireOp",EDGE,"E16.11.1.0"),sQuery(id+"F2.wireOp",EDGE,"E16.11.2.0"),sQuery(id+"F2.wireOp",EDGE,"E16.11.3.0"),sQuery(id+"F2.wireOp",EDGE,"E16.11.4.0"),sQuery(id+"F2.wireOp",EDGE,"E16.12.0.0"),sQuery(id+"F2.wireOp",EDGE,"E16.12.1.0"),sQuery(id+"F2.wireOp",EDGE,"E16.12.2.0"),sQuery(id+"F2.wireOp",EDGE,"E16.12.3.0"),sQuery(id+"F2.wireOp",EDGE,"E16.12.4.0"),sQuery(id+"F2.wireOp",EDGE,"E16.13.0.0"),sQuery(id+"F2.wireOp",EDGE,"E16.13.1.0"),sQuery(id+"F2.wireOp",EDGE,"E16.13.2.0"),sQuery(id+"F2.wireOp",EDGE,"E16.13.3.0"),sQuery(id+"F2.wireOp",EDGE,"E16.13.4.0"),sQuery(id+"F2.wireOp",EDGE,"E16.14.0.0"),sQuery(id+"F2.wireOp",EDGE,"E16.14.1.0"),sQuery(id+"F2.wireOp",EDGE,"E16.14.2.0"),sQuery(id+"F2.wireOp",EDGE,"E16.14.3.0"),sQuery(id+"F2.wireOp",EDGE,"E16.14.4.0"),sQuery(id+"F2.wireOp",EDGE,"E16.15.0.0"),sQuery(id+"F2.wireOp",EDGE,"E16.15.1.0"),sQuery(id+"F2.wireOp",EDGE,"E16.15.2.0"),sQuery(id+"F2.wireOp",EDGE,"E16.15.3.0"),sQuery(id+"F2.wireOp",EDGE,"E16.15.4.0"),sQuery(id+"F2.wireOp",EDGE,"E16.16.0.0"),sQuery(id+"F2.wireOp",EDGE,"E16.16.1.0"),sQuery(id+"F2.wireOp",EDGE,"E16.16.2.0"),sQuery(id+"F2.wireOp",EDGE,"E16.16.3.0"),sQuery(id+"F2.wireOp",EDGE,"E16.16.4.0"),sQuery(id+"F2.wireOp",EDGE,"E16.17.0.0"),sQuery(id+"F2.wireOp",EDGE,"E16.17.1.0"),sQuery(id+"F2.wireOp",EDGE,"E16.17.2.0"),sQuery(id+"F2.wireOp",EDGE,"E16.17.3.0"),sQuery(id+"F2.wireOp",EDGE,"E16.17.4.0"),sQuery(id+"F2.wireOp",EDGE,"E16.18.0.0"),sQuery(id+"F2.wireOp",EDGE,"E16.18.1.0"),sQuery(id+"F2.wireOp",EDGE,"E16.18.2.0"),sQuery(id+"F2.wireOp",EDGE,"E16.18.3.0"),sQuery(id+"F2.wireOp",EDGE,"E16.18.4.0"),sQuery(id+"F2.wireOp",EDGE,"E16.19.0.0"),sQuery(id+"F2.wireOp",EDGE,"E16.19.1.0"),sQuery(id+"F2.wireOp",EDGE,"E16.19.2.0"),sQuery(id+"F2.wireOp",EDGE,"E16.19.3.0"),sQuery(id+"F2.wireOp",EDGE,"E16.19.4.0"),sQuery(id+"F2.wireOp",EDGE,"E16.20.0.0"),sQuery(id+"F2.wireOp",EDGE,"E16.20.1.0"),sQuery(id+"F2.wireOp",EDGE,"E16.20.2.0"),sQuery(id+"F2.wireOp",EDGE,"E16.20.3.0"),sQuery(id+"F2.wireOp",EDGE,"E16.20.4.0"),sQuery(id+"F2.wireOp",EDGE,"E16.21.0.0"),sQuery(id+"F2.wireOp",EDGE,"E16.21.1.0"),sQuery(id+"F2.wireOp",EDGE,"E16.21.2.0"),sQuery(id+"F2.wireOp",EDGE,"E16.21.3.0"),sQuery(id+"F2.wireOp",EDGE,"E16.21.4.0"),sQuery(id+"F2.wireOp",EDGE,"E16.22.0.0"),sQuery(id+"F2.wireOp",EDGE,"E16.22.1.0"),sQuery(id+"F2.wireOp",EDGE,"E16.22.2.0"),sQuery(id+"F2.wireOp",EDGE,"E16.22.3.0"),sQuery(id+"F2.wireOp",EDGE,"E16.22.4.0"),sQuery(id+"F2.wireOp",EDGE,"E16.23.0.0"),sQuery(id+"F2.wireOp",EDGE,"E16.23.1.0"),sQuery(id+"F2.wireOp",EDGE,"E16.23.2.0"),sQuery(id+"F2.wireOp",EDGE,"E16.23.3.0"),sQuery(id+"F2.wireOp",EDGE,"E16.23.4.0"),sQuery(id+"F2.wireOp",EDGE,"E16.24.0.0"),sQuery(id+"F2.wireOp",EDGE,"E16.24.1.0"),sQuery(id+"F2.wireOp",EDGE,"E16.24.2.0"),sQuery(id+"F2.wireOp",EDGE,"E16.24.3.0"),sQuery(id+"F2.wireOp",EDGE,"E16.24.4.0"),sQuery(id+"F2.wireOp",EDGE,"E16.25.0.0"),sQuery(id+"F2.wireOp",EDGE,"E16.25.1.0"),sQuery(id+"F2.wireOp",EDGE,"E16.25.2.0"),sQuery(id+"F2.wireOp",EDGE,"E16.25.3.0"),sQuery(id+"F2.wireOp",EDGE,"E16.25.4.0"),sQuery(id+"F2.wireOp",EDGE,"E16.26.0.0"),sQuery(id+"F2.wireOp",EDGE,"E16.26.1.0"),sQuery(id+"F2.wireOp",EDGE,"E16.26.2.0"),sQuery(id+"F2.wireOp",EDGE,"E16.26.3.0"),sQuery(id+"F2.wireOp",EDGE,"E16.26.4.0")])],"isStart":true}),makeQuery(id+"F4.opExtrude","CAP_FACE",FACE,{"disambiguationData":[OSD([subQ9,subQ8,subQ7,subQ6,subQ5,subQ4,subQ3,subQ2,subQ1,subQ0])],"isStart":true})]});}
            var sketch = newSketch(context, id + "F23", { "sketchPlane" : qUnion([Q0])});
            skCircle(sketch, "E129.0", {"center": v(5.75, 9.48) * mm, "radius": 1.75 * mm});
            skCircle(sketch, "E130.0", {"center": v(54.5, 9.48) * mm, "radius": 1.75 * mm});
            skCircle(sketch, "E131.0", {"center": v(103.25, 9.48) * mm, "radius": 1.75 * mm});
            skCircle(sketch, "E132.0", {"center": v(5.75, -14.52) * mm, "radius": 1.75 * mm});
            skCircle(sketch, "E133.0", {"center": v(54.5, -14.52) * mm, "radius": 1.75 * mm});
            skCircle(sketch, "E134.0", {"center": v(103.25, -14.52) * mm, "radius": 1.75 * mm});
            skCircle(sketch, "E135.0", {"center": v(10.3, 4.91) * mm, "radius": 1.5 * mm});
            skCircle(sketch, "E136.0", {"center": v(97.46, -8.5) * mm, "radius": 1.5 * mm});
            skLineSegment(sketch, "E137.bottom", {"start": v(2.75, 12.48) * mm, "end": v(106.25, 12.48) * mm});
            skLineSegment(sketch, "E137.top", {"start": v(2.75, -17.52) * mm, "end": v(106.25, -17.52) * mm});
            skLineSegment(sketch, "E137.left", {"start": v(2.75, 12.48) * mm, "end": v(2.75, -17.52) * mm});
            skLineSegment(sketch, "E137.right", {"start": v(106.25, 12.48) * mm, "end": v(106.25, -17.52) * mm});
            skLineSegment(sketch, "E138.bottom", {"start": v(7.8, 7.41) * mm, "end": v(99.96, 7.41) * mm});
            skLineSegment(sketch, "E138.top", {"start": v(7.8, -11) * mm, "end": v(99.96, -11) * mm});
            skLineSegment(sketch, "E138.left", {"start": v(7.8, 7.41) * mm, "end": v(7.8, -11) * mm});
            skLineSegment(sketch, "E138.right", {"start": v(99.96, 7.41) * mm, "end": v(99.96, -11) * mm});
            skSolve(sketch);
        }
        {
            var Q0;
            Q0=makeQuery(id+"F23.imprint","IMPRINT",FACE,{"disambiguationData":[TD([[makeQuery(id+"F23.imprint","IMPRINT",EDGE,{"derivedFrom":sQuery(id+"F23.wireOp",EDGE,"E129.0")}),-1.0]])]});
            var Q1;
            Q1=qCreatedBy(makeId("Top.planeOp"),FACE);
            extrude(context, id + "F24", {"entities" : qUnion([Q0]), "endBound" : BoundingType.UP_TO_SURFACE, "endBoundEntityFace" : qUnion([Q1]), "depth" : 25 * mm});
        }
        {
            var Q0;
            Q0=makeQuery(id+"F24.opExtrude","CAP_FACE",FACE,{"disambiguationData":[OSD([sQuery(id+"F23.wireOp",EDGE,"E129.0"),sQuery(id+"F23.wireOp",EDGE,"E130.0"),sQuery(id+"F23.wireOp",EDGE,"E131.0"),sQuery(id+"F23.wireOp",EDGE,"E132.0"),sQuery(id+"F23.wireOp",EDGE,"E133.0"),sQuery(id+"F23.wireOp",EDGE,"E134.0"),sQuery(id+"F23.wireOp",EDGE,"E137.bottom"),sQuery(id+"F23.wireOp",EDGE,"E137.top"),sQuery(id+"F23.wireOp",EDGE,"E137.left"),sQuery(id+"F23.wireOp",EDGE,"E137.right"),sQuery(id+"F23.wireOp",EDGE,"E138.bottom"),sQuery(id+"F23.wireOp",EDGE,"E138.top"),sQuery(id+"F23.wireOp",EDGE,"E138.left"),sQuery(id+"F23.wireOp",EDGE,"E138.right")])],"isStart":true});
            var sketch = newSketch(context, id + "F25", { "sketchPlane" : qUnion([Q0])});
            skLineSegment(sketch, "E139.0", {"start": v(7.8, -7.41) * mm, "end": v(7.8, 11) * mm});
            skCircle(sketch, "E140.0", {"center": v(54.5, -9.48) * mm, "radius": 1.75 * mm});
            skCircle(sketch, "E141.0", {"center": v(54.5, 14.52) * mm, "radius": 1.75 * mm});
            skLineSegment(sketch, "E142.0", {"start": v(99.96, -7.41) * mm, "end": v(99.96, 11) * mm});
            skLineSegment(sketch, "E143.0", {"start": v(106.25, -12.48) * mm, "end": v(106.25, 17.52) * mm});
            skLineSegment(sketch, "E144.0", {"start": v(2.75, 17.52) * mm, "end": v(106.25, 17.52) * mm});
            skLineSegment(sketch, "E145.0", {"start": v(7.8, 11) * mm, "end": v(99.96, 11) * mm});
            skLineSegment(sketch, "E146.0", {"start": v(7.8, -7.41) * mm, "end": v(99.96, -7.41) * mm});
            skLineSegment(sketch, "E147.0", {"start": v(2.75, -12.48) * mm, "end": v(106.25, -12.48) * mm});
            skLineSegment(sketch, "E148", {"start": v(8.5, 17.52) * mm, "end": v(8.5, -12.48) * mm});
            skLineSegment(sketch, "E149", {"start": v(51.75, 17.52) * mm, "end": v(51.75, -12.48) * mm});
            skLineSegment(sketch, "E150", {"start": v(57.25, 17.52) * mm, "end": v(57.25, -12.48) * mm});
            skLineSegment(sketch, "E151", {"start": v(100.5, 17.52) * mm, "end": v(100.5, -12.48) * mm});
            skLineSegment(sketch, "E152.0", {"start": v(2.75, -12.48) * mm, "end": v(2.75, 17.52) * mm});
            skLineSegment(sketch, "E153", {"start": v(2.75, 11.77) * mm, "end": v(106.25, 11.77) * mm});
            skLineSegment(sketch, "E154", {"start": v(2.75, -6.73) * mm, "end": v(106.25, -6.73) * mm});
            skSolve(sketch);
        }
        {
            var Q0;
            {var subQ1=sQuery(id+"F25.wireOp",EDGE,"E145.0");var subQ9=sQuery(id+"F25.wireOp",EDGE,"E139.0");var subQ10=makeQuery(id+"F25.imprint","INTERSECT",VERTEX,{"derivedFrom":[subQ9,subQ1]});Q0=makeQuery(id+"F25.imprint","IMPRINT",FACE,{"disambiguationData":[TD([[makeQuery(id+"F25.imprint","IMPRINT",EDGE,{"disambiguationData":[TD([[subQ10,1.0]])],"derivedFrom":subQ9}),1.0]])]});}
            var Q1;
            {var subQ0=sQuery(id+"F25.wireOp",EDGE,"E148");var subQ1=sQuery(id+"F25.wireOp",EDGE,"E144.0");var subQ2=makeQuery(id+"F25.imprint","INTERSECT",VERTEX,{"derivedFrom":[subQ1,subQ0]});Q1=makeQuery(id+"F25.imprint","IMPRINT",FACE,{"disambiguationData":[TD([[makeQuery(id+"F25.imprint","IMPRINT",EDGE,{"disambiguationData":[TD([[subQ2,-1.0]])],"derivedFrom":subQ1}),-1.0]])]});}
            var Q2;
            {var subQ0=sQuery(id+"F25.wireOp",EDGE,"E148");var subQ1=sQuery(id+"F25.wireOp",EDGE,"E146.0");var subQ2=makeQuery(id+"F25.imprint","INTERSECT",VERTEX,{"derivedFrom":[subQ1,subQ0]});Q2=makeQuery(id+"F25.imprint","IMPRINT",FACE,{"disambiguationData":[TD([[makeQuery(id+"F25.imprint","IMPRINT",EDGE,{"disambiguationData":[TD([[subQ2,-1.0]])],"derivedFrom":subQ1}),-1.0]])]});}
            var Q3;
            {var subQ0=sQuery(id+"F25.wireOp",EDGE,"E148");var subQ1=sQuery(id+"F25.wireOp",EDGE,"E145.0");var subQ2=makeQuery(id+"F25.imprint","INTERSECT",VERTEX,{"derivedFrom":[subQ1,subQ0]});Q3=makeQuery(id+"F25.imprint","IMPRINT",FACE,{"disambiguationData":[TD([[makeQuery(id+"F25.imprint","IMPRINT",EDGE,{"disambiguationData":[TD([[subQ2,-1.0]])],"derivedFrom":subQ1}),1.0]])]});}
            var Q4;
            {var subQ0=sQuery(id+"F25.wireOp",EDGE,"E150");var subQ1=sQuery(id+"F25.wireOp",EDGE,"E144.0");var subQ2=makeQuery(id+"F25.imprint","INTERSECT",VERTEX,{"derivedFrom":[subQ1,subQ0]});Q4=makeQuery(id+"F25.imprint","IMPRINT",FACE,{"disambiguationData":[TD([[makeQuery(id+"F25.imprint","IMPRINT",EDGE,{"disambiguationData":[TD([[subQ2,-1.0]])],"derivedFrom":subQ1}),-1.0]])]});}
            var Q5;
            {var subQ1=sQuery(id+"F25.wireOp",EDGE,"E145.0");var subQ5=sQuery(id+"F25.wireOp",EDGE,"E142.0");var subQ6=makeQuery(id+"F25.imprint","INTERSECT",VERTEX,{"derivedFrom":[subQ5,subQ1]});Q5=makeQuery(id+"F25.imprint","IMPRINT",FACE,{"disambiguationData":[TD([[makeQuery(id+"F25.imprint","IMPRINT",EDGE,{"disambiguationData":[TD([[subQ6,1.0]])],"derivedFrom":subQ5}),-1.0]])]});}
            var Q6;
            {var subQ0=sQuery(id+"F25.wireOp",EDGE,"E153");var subQ1=sQuery(id+"F25.wireOp",EDGE,"E143.0");var subQ2=makeQuery(id+"F25.imprint","INTERSECT",VERTEX,{"derivedFrom":[subQ1,subQ0]});Q6=makeQuery(id+"F25.imprint","IMPRINT",FACE,{"disambiguationData":[TD([[makeQuery(id+"F25.imprint","IMPRINT",EDGE,{"disambiguationData":[TD([[subQ2,1.0]])],"derivedFrom":subQ1}),1.0]])]});}
            var Q7;
            {var subQ3=sQuery(id+"F25.wireOp",EDGE,"E146.0");var subQ7=sQuery(id+"F25.wireOp",EDGE,"E142.0");var subQ8=makeQuery(id+"F25.imprint","INTERSECT",VERTEX,{"derivedFrom":[subQ7,subQ3]});Q7=makeQuery(id+"F25.imprint","IMPRINT",FACE,{"disambiguationData":[TD([[makeQuery(id+"F25.imprint","IMPRINT",EDGE,{"disambiguationData":[TD([[subQ8,-1.0]])],"derivedFrom":subQ7}),-1.0]])]});}
            extrude(context, id + "F26", {"entities" : qUnion([Q0, Q1, Q2, Q3, Q4, Q5, Q6, Q7]), "operationType" : NewBodyOperationType.REMOVE, "oppositeDirection" : true, "depth" : 2 * mm});
        }
        {
            var Q0;
            Q0=qCreatedBy(makeId("Top.planeOp"),FACE);
            var sketch = newSketch(context, id + "F27", { "sketchPlane" : qUnion([Q0])});
            skCircle(sketch, "E155.0", {"center": v(-57.86, 26.02) * mm, "radius": 1.75 * mm});
            skCircle(sketch, "E156.0", {"center": v(-57.86, -29.6) * mm, "radius": 1.75 * mm});
            skLineSegment(sketch, "E157.0", {"start": v(-130.86, 21.72) * mm, "end": v(-130.86, 3.31) * mm, "construction": true});
            skLineSegment(sketch, "E157.1", {"start": v(-130.86, 21.72) * mm, "end": v(-99.04, 21.72) * mm, "construction": true});
            skLineSegment(sketch, "E157.2", {"start": v(-99.04, 21.72) * mm, "end": v(-99.04, 3.31) * mm, "construction": true});
            skLineSegment(sketch, "E157.3", {"start": v(-130.86, 3.31) * mm, "end": v(-99.04, 3.31) * mm, "construction": true});
            skCircle(sketch, "E157.4", {"center": v(-95.86, 2.71) * mm, "radius": 1.75 * mm});
            skCircle(sketch, "E157.5", {"center": v(-95.86, 23.03) * mm, "radius": 1.75 * mm});
            skCircle(sketch, "E157.6", {"center": v(-133.96, 23.03) * mm, "radius": 1.75 * mm});
            skCircle(sketch, "E157.7", {"center": v(-133.96, 2.71) * mm, "radius": 1.75 * mm});
            skCircle(sketch, "E158.0", {"center": v(-133.96, -6.29) * mm, "radius": 1.75 * mm});
            skCircle(sketch, "E158.1", {"center": v(-133.96, -26.6) * mm, "radius": 1.75 * mm});
            skLineSegment(sketch, "E158.2", {"start": v(-130.86, -7.6) * mm, "end": v(-130.86, -26) * mm, "construction": true});
            skLineSegment(sketch, "E158.3", {"start": v(-130.86, -7.6) * mm, "end": v(-99.04, -7.6) * mm, "construction": true});
            skLineSegment(sketch, "E158.4", {"start": v(-99.04, -7.6) * mm, "end": v(-99.04, -26) * mm, "construction": true});
            skLineSegment(sketch, "E158.5", {"start": v(-130.86, -26) * mm, "end": v(-99.04, -26) * mm, "construction": true});
            skCircle(sketch, "E158.6", {"center": v(-95.86, -26.6) * mm, "radius": 1.75 * mm});
            skCircle(sketch, "E158.7", {"center": v(-95.86, -6.29) * mm, "radius": 1.75 * mm});
            skCircle(sketch, "E159.0", {"center": v(5.75, 9.48) * mm, "radius": 1.75 * mm});
            skCircle(sketch, "E159.1", {"center": v(5.75, -14.52) * mm, "radius": 1.75 * mm});
            skLineSegment(sketch, "E159.2", {"start": v(7.8, -11) * mm, "end": v(99.96, -11) * mm, "construction": true});
            skLineSegment(sketch, "E159.3", {"start": v(7.8, 7.41) * mm, "end": v(7.8, -11) * mm, "construction": true});
            skLineSegment(sketch, "E159.4", {"start": v(7.8, 7.41) * mm, "end": v(99.96, 7.41) * mm, "construction": true});
            skLineSegment(sketch, "E159.5", {"start": v(99.96, 7.41) * mm, "end": v(99.96, -11) * mm, "construction": true});
            skCircle(sketch, "E159.6", {"center": v(54.5, -14.52) * mm, "radius": 1.75 * mm});
            skCircle(sketch, "E159.7", {"center": v(54.5, 9.48) * mm, "radius": 1.75 * mm});
            skCircle(sketch, "E159.8", {"center": v(103.25, 9.48) * mm, "radius": 1.75 * mm});
            skCircle(sketch, "E159.9", {"center": v(103.25, -14.52) * mm, "radius": 1.75 * mm});
            skCircle(sketch, "E160.1", {"center": v(141.25, -29.6) * mm, "radius": 1.75 * mm});
            skCircle(sketch, "E160.2", {"center": v(141.25, 26.02) * mm, "radius": 1.75 * mm});
            skLineSegment(sketch, "E161.bottom", {"start": v(-150.86, 41.47) * mm, "end": v(184.8, 41.47) * mm});
            skLineSegment(sketch, "E161.top", {"start": v(-150.86, -45.76) * mm, "end": v(184.8, -45.76) * mm});
            skLineSegment(sketch, "E161.left", {"start": v(-150.86, 41.47) * mm, "end": v(-150.86, -45.76) * mm});
            skLineSegment(sketch, "E161.right", {"start": v(184.8, 41.47) * mm, "end": v(184.8, -45.76) * mm});
            skLineSegment(sketch, "E162.0", {"start": v(-130.6, -7.85) * mm, "end": v(-130.6, -25.76) * mm});
            skLineSegment(sketch, "E162.1", {"start": v(-130.6, -7.85) * mm, "end": v(-99.29, -7.85) * mm});
            skLineSegment(sketch, "E162.2", {"start": v(-99.29, -7.85) * mm, "end": v(-99.29, -25.76) * mm});
            skLineSegment(sketch, "E162.3", {"start": v(-130.6, -25.76) * mm, "end": v(-99.29, -25.76) * mm});
            skLineSegment(sketch, "E163.0", {"start": v(-130.6, 21.47) * mm, "end": v(-99.29, 21.47) * mm});
            skLineSegment(sketch, "E163.1", {"start": v(-130.6, 21.47) * mm, "end": v(-130.6, 3.56) * mm});
            skLineSegment(sketch, "E163.2", {"start": v(-130.6, 3.56) * mm, "end": v(-99.29, 3.56) * mm});
            skLineSegment(sketch, "E163.3", {"start": v(-99.29, 21.47) * mm, "end": v(-99.29, 3.56) * mm});
            skLineSegment(sketch, "E164.0", {"start": v(8.06, 7.16) * mm, "end": v(99.7, 7.16) * mm});
            skLineSegment(sketch, "E164.1", {"start": v(8.06, 7.16) * mm, "end": v(8.06, -10.74) * mm});
            skLineSegment(sketch, "E164.2", {"start": v(8.06, -10.74) * mm, "end": v(99.7, -10.74) * mm});
            skLineSegment(sketch, "E164.3", {"start": v(99.7, 7.16) * mm, "end": v(99.7, -10.74) * mm});
            skCircle(sketch, "E165.0", {"center": v(141.25, -1.79) * mm, "radius": 23.81 * mm, "construction": true});
            skCircle(sketch, "E166.0", {"center": v(141.25, -1.79) * mm, "radius": 23.56 * mm});
            skCircle(sketch, "E167.0", {"center": v(-57.86, -1.79) * mm, "radius": 23.81 * mm, "construction": true});
            skCircle(sketch, "E168.0", {"center": v(-57.86, -1.79) * mm, "radius": 23.56 * mm});
            skSolve(sketch);
        }
        {
            var Q0;
            Q0=makeQuery(id+"F27.imprint","IMPRINT",FACE,{"disambiguationData":[TD([[makeQuery(id+"F27.imprint","IMPRINT",EDGE,{"derivedFrom":sQuery(id+"F27.wireOp",EDGE,"E155.0")}),-1.0]])]});
            extrude(context, id + "F28", {"entities" : qUnion([Q0]), "depth" : 4 * mm});
        }
        {
            var Q0;
            Q0=makeQuery(id+"F28.opExtrude","CAP_FACE",FACE,{"disambiguationData":[OSD([sQuery(id+"F27.wireOp",EDGE,"E155.0"),sQuery(id+"F27.wireOp",EDGE,"E156.0"),sQuery(id+"F27.wireOp",EDGE,"E157.4"),sQuery(id+"F27.wireOp",EDGE,"E157.5"),sQuery(id+"F27.wireOp",EDGE,"E157.6"),sQuery(id+"F27.wireOp",EDGE,"E157.7"),sQuery(id+"F27.wireOp",EDGE,"E158.0"),sQuery(id+"F27.wireOp",EDGE,"E158.1"),sQuery(id+"F27.wireOp",EDGE,"E158.6"),sQuery(id+"F27.wireOp",EDGE,"E158.7"),sQuery(id+"F27.wireOp",EDGE,"E159.0"),sQuery(id+"F27.wireOp",EDGE,"E159.1"),sQuery(id+"F27.wireOp",EDGE,"E159.6"),sQuery(id+"F27.wireOp",EDGE,"E159.7"),sQuery(id+"F27.wireOp",EDGE,"E159.8"),sQuery(id+"F27.wireOp",EDGE,"E159.9"),sQuery(id+"F27.wireOp",EDGE,"E160.1"),sQuery(id+"F27.wireOp",EDGE,"E160.2"),sQuery(id+"F27.wireOp",EDGE,"E161.bottom"),sQuery(id+"F27.wireOp",EDGE,"E161.top"),sQuery(id+"F27.wireOp",EDGE,"E161.left"),sQuery(id+"F27.wireOp",EDGE,"E161.right"),sQuery(id+"F27.wireOp",EDGE,"E162.0"),sQuery(id+"F27.wireOp",EDGE,"E162.1"),sQuery(id+"F27.wireOp",EDGE,"E162.2"),sQuery(id+"F27.wireOp",EDGE,"E162.3"),sQuery(id+"F27.wireOp",EDGE,"E163.0"),sQuery(id+"F27.wireOp",EDGE,"E163.1"),sQuery(id+"F27.wireOp",EDGE,"E163.2"),sQuery(id+"F27.wireOp",EDGE,"E163.3"),sQuery(id+"F27.wireOp",EDGE,"E164.0"),sQuery(id+"F27.wireOp",EDGE,"E164.1"),sQuery(id+"F27.wireOp",EDGE,"E164.2"),sQuery(id+"F27.wireOp",EDGE,"E164.3"),sQuery(id+"F27.wireOp",EDGE,"E166.0"),sQuery(id+"F27.wireOp",EDGE,"E168.0")])],"isStart":false});
            var sketch = newSketch(context, id + "F29", { "sketchPlane" : qUnion([Q0])});
            skLineSegment(sketch, "E169.0", {"start": v(-150.86, -45.76) * mm, "end": v(184.8, -45.76) * mm});
            skLineSegment(sketch, "E169.1", {"start": v(-150.86, 41.47) * mm, "end": v(-150.86, -45.76) * mm});
            skLineSegment(sketch, "E169.2", {"start": v(-150.86, 41.47) * mm, "end": v(184.8, 41.47) * mm});
            skCircle(sketch, "E169.3", {"center": v(-57.86, -1.79) * mm, "radius": 23.56 * mm});
            skLineSegment(sketch, "E169.4", {"start": v(-130.6, 3.56) * mm, "end": v(-99.29, 3.56) * mm});
            skLineSegment(sketch, "E169.5", {"start": v(-99.29, 21.47) * mm, "end": v(-99.29, 3.56) * mm});
            skLineSegment(sketch, "E169.6", {"start": v(-130.6, 21.47) * mm, "end": v(-99.29, 21.47) * mm});
            skLineSegment(sketch, "E169.7", {"start": v(-130.6, 21.47) * mm, "end": v(-130.6, 3.56) * mm});
            skLineSegment(sketch, "E169.8", {"start": v(-130.6, -7.85) * mm, "end": v(-130.6, -25.76) * mm});
            skLineSegment(sketch, "E169.9", {"start": v(-130.6, -7.85) * mm, "end": v(-99.29, -7.85) * mm});
            skLineSegment(sketch, "E169.10", {"start": v(-99.29, -7.85) * mm, "end": v(-99.29, -25.76) * mm});
            skLineSegment(sketch, "E169.11", {"start": v(-130.6, -25.76) * mm, "end": v(-99.29, -25.76) * mm});
            skCircle(sketch, "E169.12", {"center": v(-95.86, -26.6) * mm, "radius": 1.75 * mm});
            skCircle(sketch, "E169.13", {"center": v(-95.86, -6.29) * mm, "radius": 1.75 * mm});
            skCircle(sketch, "E169.14", {"center": v(-95.86, 2.71) * mm, "radius": 1.75 * mm});
            skCircle(sketch, "E169.15", {"center": v(-95.86, 23.03) * mm, "radius": 1.75 * mm});
            skCircle(sketch, "E169.16", {"center": v(-133.96, 23.03) * mm, "radius": 1.75 * mm});
            skCircle(sketch, "E169.17", {"center": v(-133.96, 2.71) * mm, "radius": 1.75 * mm});
            skCircle(sketch, "E169.18", {"center": v(-133.96, -6.29) * mm, "radius": 1.75 * mm});
            skCircle(sketch, "E169.19", {"center": v(-133.96, -26.6) * mm, "radius": 1.75 * mm});
            skCircle(sketch, "E169.20", {"center": v(-57.86, 26.02) * mm, "radius": 1.75 * mm});
            skCircle(sketch, "E169.21", {"center": v(-57.86, -29.6) * mm, "radius": 1.75 * mm});
            skCircle(sketch, "E170.0", {"center": v(5.75, 9.48) * mm, "radius": 1.75 * mm});
            skLineSegment(sketch, "E170.1", {"start": v(8.06, 7.16) * mm, "end": v(8.06, -10.74) * mm});
            skLineSegment(sketch, "E170.2", {"start": v(8.06, 7.16) * mm, "end": v(99.7, 7.16) * mm});
            skLineSegment(sketch, "E170.3", {"start": v(99.7, 7.16) * mm, "end": v(99.7, -10.74) * mm});
            skLineSegment(sketch, "E170.4", {"start": v(8.06, -10.74) * mm, "end": v(99.7, -10.74) * mm});
            skCircle(sketch, "E170.5", {"center": v(5.75, -14.52) * mm, "radius": 1.75 * mm});
            skCircle(sketch, "E170.6", {"center": v(54.5, -14.52) * mm, "radius": 1.75 * mm});
            skCircle(sketch, "E170.7", {"center": v(103.25, -14.52) * mm, "radius": 1.75 * mm});
            skCircle(sketch, "E170.8", {"center": v(103.25, 9.48) * mm, "radius": 1.75 * mm});
            skCircle(sketch, "E170.9", {"center": v(54.5, 9.48) * mm, "radius": 1.75 * mm});
            skCircle(sketch, "E171.0", {"center": v(141.25, -1.79) * mm, "radius": 23.56 * mm});
            skCircle(sketch, "E171.1", {"center": v(141.25, 26.02) * mm, "radius": 1.75 * mm});
            skCircle(sketch, "E171.2", {"center": v(141.25, -29.6) * mm, "radius": 1.75 * mm});
            skLineSegment(sketch, "E172.0", {"start": v(184.8, 41.47) * mm, "end": v(184.8, -45.76) * mm});
            skSolve(sketch);
        }
        {
            var Q0;
            Q0=makeQuery(id+"F28.opExtrude","SWEPT_FACE",FACE,{"disambiguationData":[OSD([sQuery(id+"F27.wireOp",EDGE,"E161.right")])]});
            cPlane(context, id + "F30", {"entities" : qUnion([Q0]), "cplaneType" : CPlaneType.OFFSET, "offset" : 10 * mm, "oppositeDirection" : true, "width" : 150 * mm, "height" : 150 * mm});
        }
        {
            var Q0;
            Q0=qCreatedBy(id+"F30.planeOp",FACE);
            var sketch = newSketch(context, id + "F31", { "sketchPlane" : qUnion([Q0])});
            skLineSegment(sketch, "E173.0", {"start": v(41.47, 4) * mm, "end": v(-45.76, 4) * mm});
            skLineSegment(sketch, "E174.0.0", {"start": v(-45.76, 0) * mm, "end": v(41.47, 0) * mm});
            skLineSegment(sketch, "E174.0.1", {"start": v(41.47, 0) * mm, "end": v(41.47, 4) * mm});
            skLineSegment(sketch, "E174.0.3", {"start": v(-45.76, 4) * mm, "end": v(-45.76, 0) * mm});
            skLineSegment(sketch, "E175.0", {"start": v(41.47, 0) * mm, "end": v(-45.76, 0) * mm});
            skLineSegment(sketch, "E176", {"start": v(-52.4, 3.5) * mm, "end": v(-27.4, -39.8) * mm});
            skLineSegment(sketch, "E177", {"start": v(-22, 4) * mm, "end": v(-22, 5) * mm});
            skLineSegment(sketch, "E178", {"start": v(-25, 8) * mm, "end": v(-49.8, 8) * mm});
            skPoint(sketch, "E179.visualSharp", {"position": v(-22, 8) * mm});
            skArc(sketch, "E179.filletArc", {"start": v(-22, 5) * mm, "mid": v(-22.87, 7.12) * mm, "end": v(-25, 8) * mm});
            skPoint(sketch, "E180.visualSharp", {"position": v(-55, 8) * mm});
            skArc(sketch, "E180.filletArc", {"start": v(-49.8, 8) * mm, "mid": v(-52.4, 6.5) * mm, "end": v(-52.4, 3.5) * mm});
            skLineSegment(sketch, "E181", {"start": v(-22, 0) * mm, "end": v(-22, -1) * mm});
            skLineSegment(sketch, "E182", {"start": v(-25, -4) * mm, "end": v(-38.25, -4) * mm});
            skLineSegment(sketch, "E183", {"start": v(-40.85, -8.5) * mm, "end": v(-24.95, -36.05) * mm});
            skLineSegment(sketch, "E184", {"start": v(-25.66, -38.77) * mm, "end": v(-27.4, -39.8) * mm});
            skPoint(sketch, "E185.visualSharp", {"position": v(-22, -4) * mm});
            skArc(sketch, "E185.filletArc", {"start": v(-25, -4) * mm, "mid": v(-22.87, -3.12) * mm, "end": v(-22, -1) * mm});
            skPoint(sketch, "E186.visualSharp", {"position": v(-43.45, -4) * mm});
            skArc(sketch, "E186.filletArc", {"start": v(-38.25, -4) * mm, "mid": v(-40.85, -5.5) * mm, "end": v(-40.85, -8.5) * mm});
            skPoint(sketch, "E187.visualSharp", {"position": v(-23.96, -37.76) * mm});
            skArc(sketch, "E187.filletArc", {"start": v(-25.66, -38.77) * mm, "mid": v(-24.74, -37.55) * mm, "end": v(-24.95, -36.05) * mm});
            skSolve(sketch);
        }
        {
            var Q0;
            {var subQ2=sQuery(id+"F31.wireOp",EDGE,"E174.0.3");Q0=makeQuery(id+"F31.imprint","IMPRINT",FACE,{"disambiguationData":[TD([[makeQuery(id+"F31.imprint","IMPRINT",EDGE,{"derivedFrom":subQ2}),-1.0]])]});}
            extrude(context, id + "F32", {"entities" : qUnion([Q0]), "endBound" : BoundingType.SYMMETRIC, "depth" : 4.2 * mm});
        }
    });
